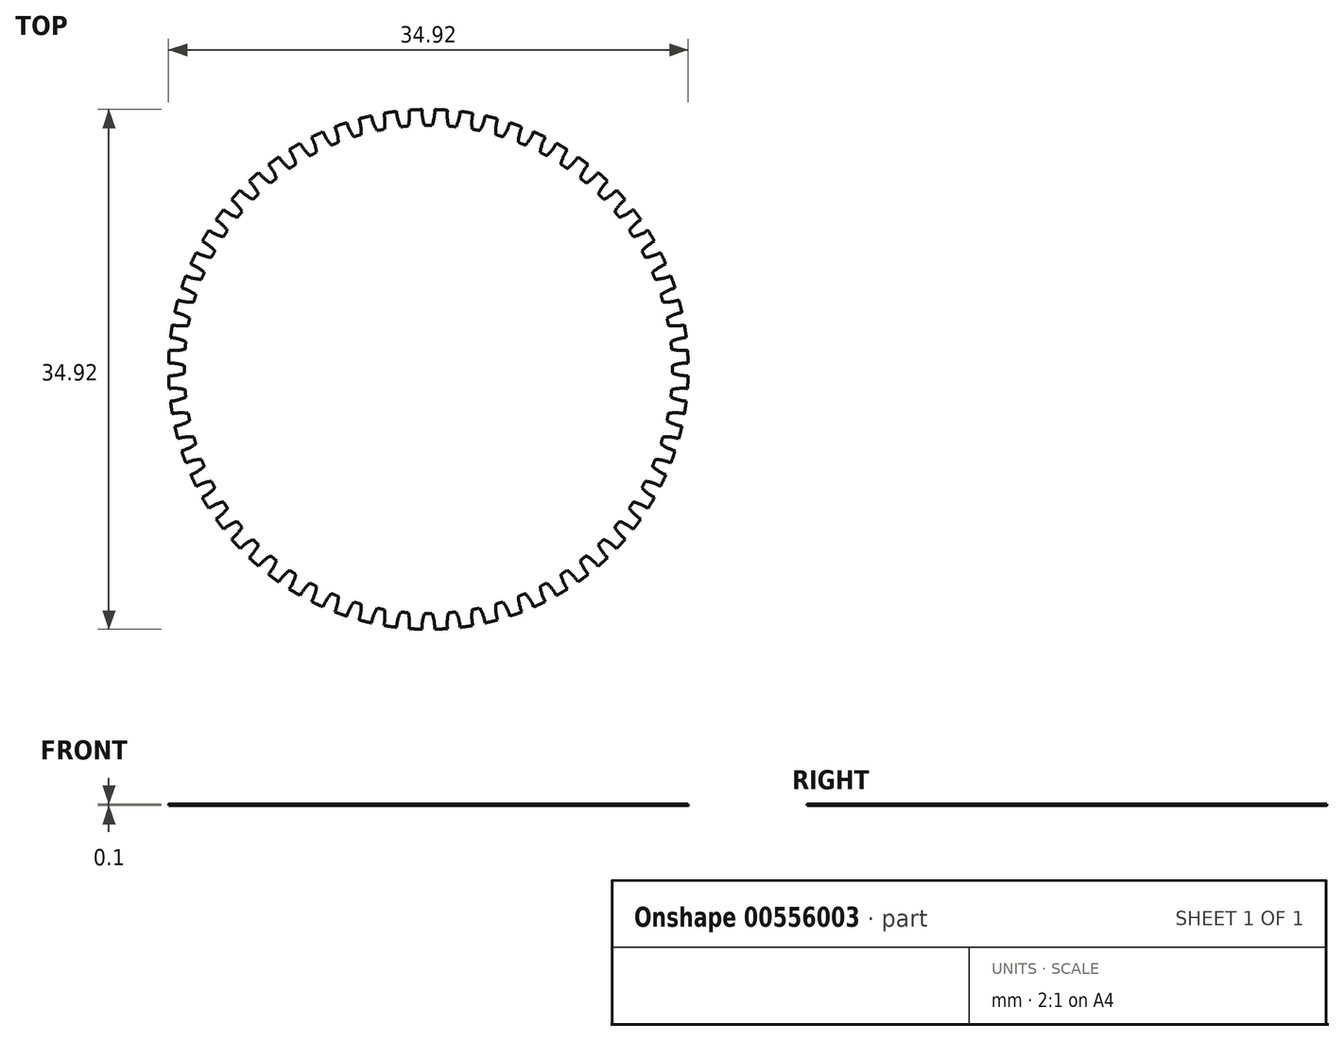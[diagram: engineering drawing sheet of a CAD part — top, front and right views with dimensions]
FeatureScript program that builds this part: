
annotation { "Feature Type Name" : "Feature", "Feature Type Description" : "" }
export const myFeature = defineFeature(function(context is Context, id is Id, definition is map)
    precondition{}
    {
        {
            var Q0;
            Q0=qCreatedBy(makeId("Top.planeOp"),FACE);
            var sketch = newSketch(context, id + "F0", { "sketchPlane" : qUnion([Q0])});
            skPoint(sketch, "E0", {"position": v(0.27, 22.75) * mm});
            skPoint(sketch, "E1", {"position": v(0.39, 22.22) * mm});
            skPoint(sketch, "E2", {"position": v(0.4, 21.7) * mm});
            skPoint(sketch, "E3", {"position": v(0.43, 17.46) * mm});
            skPoint(sketch, "E4", {"position": v(0.39, 16.93) * mm});
            skPoint(sketch, "E5", {"position": v(0.25, 16.4) * mm});
            skArc(sketch, "E6", {"start": v(0, 16.4) * mm, "mid": v(0.13, 16.4) * mm, "end": v(0.25, 16.4) * mm});
            skArc(sketch, "E7", {"start": v(0.43, 17.46) * mm, "mid": v(0.64, 17.46) * mm, "end": v(0.86, 17.45) * mm});
            skArc(sketch, "E8", {"start": v(0, 22.75) * mm, "mid": v(0.13, 22.75) * mm, "end": v(0.27, 22.75) * mm});
            skArc(sketch, "E9", {"start": v(0.4, 21.7) * mm, "mid": v(0.6, 21.69) * mm, "end": v(0.81, 21.68) * mm});
            skArc(sketch, "E10", {"start": v(0.4, 21.7) * mm, "mid": v(0.39, 22.23) * mm, "end": v(0.27, 22.75) * mm});
            skArc(sketch, "E11", {"start": v(0.25, 16.4) * mm, "mid": v(0.39, 16.92) * mm, "end": v(0.43, 17.46) * mm});
            skArc(sketch, "E12.MirrorCS", {"start": v(0, 22.75) * mm, "mid": v(-0.13, 22.75) * mm, "end": v(-0.27, 22.75) * mm});
            skArc(sketch, "E13.MirrorCS", {"start": v(0, 16.4) * mm, "mid": v(-0.13, 16.4) * mm, "end": v(-0.25, 16.4) * mm});
            skArc(sketch, "E14.MirrorCS", {"start": v(-0.43, 17.46) * mm, "mid": v(-0.64, 17.46) * mm, "end": v(-0.86, 17.45) * mm});
            skArc(sketch, "E15.MirrorCS", {"start": v(-0.4, 21.7) * mm, "mid": v(-0.6, 21.69) * mm, "end": v(-0.81, 21.68) * mm});
            skArc(sketch, "E16.MirrorCS", {"start": v(-0.4, 21.7) * mm, "mid": v(-0.39, 22.23) * mm, "end": v(-0.27, 22.75) * mm});
            skArc(sketch, "E17.MirrorCS", {"start": v(-0.25, 16.4) * mm, "mid": v(-0.39, 16.92) * mm, "end": v(-0.43, 17.46) * mm});
            skPoint(sketch, "E18.MirrorP", {"position": v(-0.39, 22.22) * mm});
            skPoint(sketch, "E19.MirrorP", {"position": v(-0.43, 17.46) * mm});
            skPoint(sketch, "E20.MirrorP", {"position": v(-0.39, 16.93) * mm});
            skPoint(sketch, "E21.MirrorP", {"position": v(-0.4, 21.7) * mm});
            skPoint(sketch, "E22.MirrorP", {"position": v(-0.27, 22.75) * mm});
            skPoint(sketch, "E23.MirrorP", {"position": v(-0.25, 16.4) * mm});
            skPoint(sketch, "E24.1.0", {"position": v(-1.44, 22.7) * mm});
            skPoint(sketch, "E24.1.1", {"position": v(-1.97, 22.67) * mm});
            skPoint(sketch, "E24.1.2", {"position": v(-1.27, 22.19) * mm});
            skPoint(sketch, "E24.1.3", {"position": v(-2.05, 22.13) * mm});
            skPoint(sketch, "E24.1.4", {"position": v(-1.22, 21.66) * mm});
            skPoint(sketch, "E24.1.5", {"position": v(-2.03, 21.6) * mm});
            skArc(sketch, "E24.1.6", {"start": v(-1.22, 21.66) * mm, "mid": v(-1.01, 21.67) * mm, "end": v(-0.81, 21.68) * mm});
            skArc(sketch, "E24.1.7", {"start": v(-2.03, 21.6) * mm, "mid": v(-2.05, 22.14) * mm, "end": v(-1.97, 22.67) * mm});
            skArc(sketch, "E24.1.8", {"start": v(-1.22, 21.66) * mm, "mid": v(-1.27, 22.2) * mm, "end": v(-1.44, 22.7) * mm});
            skArc(sketch, "E24.1.9", {"start": v(-2.03, 21.6) * mm, "mid": v(-2.23, 21.58) * mm, "end": v(-2.43, 21.56) * mm});
            skArc(sketch, "E24.1.10", {"start": v(-1.7, 22.7) * mm, "mid": v(-1.57, 22.7) * mm, "end": v(-1.44, 22.7) * mm});
            skArc(sketch, "E24.1.11", {"start": v(-1.7, 22.7) * mm, "mid": v(-1.83, 22.68) * mm, "end": v(-1.97, 22.67) * mm});
            skPoint(sketch, "E24.2.0", {"position": v(-3.13, 22.54) * mm});
            skPoint(sketch, "E24.2.1", {"position": v(-3.65, 22.46) * mm});
            skPoint(sketch, "E24.2.2", {"position": v(-2.93, 22.03) * mm});
            skPoint(sketch, "E24.2.3", {"position": v(-3.7, 21.92) * mm});
            skPoint(sketch, "E24.2.4", {"position": v(-2.83, 21.51) * mm});
            skPoint(sketch, "E24.2.5", {"position": v(-3.63, 21.39) * mm});
            skArc(sketch, "E24.2.6", {"start": v(-2.83, 21.51) * mm, "mid": v(-2.63, 21.54) * mm, "end": v(-2.43, 21.56) * mm});
            skArc(sketch, "E24.2.7", {"start": v(-3.63, 21.39) * mm, "mid": v(-3.7, 21.92) * mm, "end": v(-3.65, 22.46) * mm});
            skArc(sketch, "E24.2.8", {"start": v(-2.83, 21.51) * mm, "mid": v(-2.93, 22.04) * mm, "end": v(-3.13, 22.54) * mm});
            skArc(sketch, "E24.2.9", {"start": v(-3.63, 21.39) * mm, "mid": v(-3.83, 21.35) * mm, "end": v(-4.03, 21.32) * mm});
            skArc(sketch, "E24.2.10", {"start": v(-3.4, 22.5) * mm, "mid": v(-3.26, 22.52) * mm, "end": v(-3.13, 22.54) * mm});
            skArc(sketch, "E24.2.11", {"start": v(-3.4, 22.5) * mm, "mid": v(-3.52, 22.48) * mm, "end": v(-3.65, 22.46) * mm});
            skPoint(sketch, "E24.3.0", {"position": v(-4.8, 22.24) * mm});
            skPoint(sketch, "E24.3.1", {"position": v(-5.32, 22.12) * mm});
            skPoint(sketch, "E24.3.2", {"position": v(-4.56, 21.75) * mm});
            skPoint(sketch, "E24.3.3", {"position": v(-5.32, 21.58) * mm});
            skPoint(sketch, "E24.3.4", {"position": v(-4.43, 21.24) * mm});
            skPoint(sketch, "E24.3.5", {"position": v(-5.22, 21.06) * mm});
            skArc(sketch, "E24.3.6", {"start": v(-4.43, 21.24) * mm, "mid": v(-4.23, 21.28) * mm, "end": v(-4.03, 21.32) * mm});
            skArc(sketch, "E24.3.7", {"start": v(-5.22, 21.06) * mm, "mid": v(-5.33, 21.59) * mm, "end": v(-5.32, 22.12) * mm});
            skArc(sketch, "E24.3.8", {"start": v(-4.43, 21.24) * mm, "mid": v(-4.57, 21.76) * mm, "end": v(-4.8, 22.24) * mm});
            skArc(sketch, "E24.3.9", {"start": v(-5.22, 21.06) * mm, "mid": v(-5.42, 21) * mm, "end": v(-5.62, 20.96) * mm});
            skArc(sketch, "E24.3.10", {"start": v(-5.06, 22.18) * mm, "mid": v(-4.93, 22.21) * mm, "end": v(-4.8, 22.24) * mm});
            skArc(sketch, "E24.3.11", {"start": v(-5.06, 22.18) * mm, "mid": v(-5.2, 22.15) * mm, "end": v(-5.32, 22.12) * mm});
            skPoint(sketch, "E24.4.0", {"position": v(-6.45, 21.82) * mm});
            skPoint(sketch, "E24.4.1", {"position": v(-6.96, 21.66) * mm});
            skPoint(sketch, "E24.4.2", {"position": v(-6.18, 21.35) * mm});
            skPoint(sketch, "E24.4.3", {"position": v(-6.92, 21.12) * mm});
            skPoint(sketch, "E24.4.4", {"position": v(-6, 20.85) * mm});
            skPoint(sketch, "E24.4.5", {"position": v(-6.78, 20.6) * mm});
            skArc(sketch, "E24.4.6", {"start": v(-6, 20.85) * mm, "mid": v(-5.81, 20.9) * mm, "end": v(-5.62, 20.96) * mm});
            skArc(sketch, "E24.4.7", {"start": v(-6.78, 20.6) * mm, "mid": v(-6.92, 21.13) * mm, "end": v(-6.96, 21.66) * mm});
            skArc(sketch, "E24.4.8", {"start": v(-6, 20.85) * mm, "mid": v(-6.18, 21.36) * mm, "end": v(-6.45, 21.82) * mm});
            skArc(sketch, "E24.4.9", {"start": v(-6.78, 20.6) * mm, "mid": v(-6.97, 20.54) * mm, "end": v(-7.17, 20.48) * mm});
            skArc(sketch, "E24.4.10", {"start": v(-6.7, 21.74) * mm, "mid": v(-6.58, 21.78) * mm, "end": v(-6.45, 21.82) * mm});
            skArc(sketch, "E24.4.11", {"start": v(-6.7, 21.74) * mm, "mid": v(-6.83, 21.7) * mm, "end": v(-6.96, 21.66) * mm});
            skPoint(sketch, "E24.5.0", {"position": v(-8.06, 21.28) * mm});
            skPoint(sketch, "E24.5.1", {"position": v(-8.56, 21.08) * mm});
            skPoint(sketch, "E24.5.2", {"position": v(-7.76, 20.83) * mm});
            skPoint(sketch, "E24.5.3", {"position": v(-8.48, 20.54) * mm});
            skPoint(sketch, "E24.5.4", {"position": v(-7.55, 20.34) * mm});
            skPoint(sketch, "E24.5.5", {"position": v(-8.3, 20.04) * mm});
            skArc(sketch, "E24.5.6", {"start": v(-7.55, 20.34) * mm, "mid": v(-7.36, 20.41) * mm, "end": v(-7.17, 20.48) * mm});
            skArc(sketch, "E24.5.7", {"start": v(-8.3, 20.04) * mm, "mid": v(-8.48, 20.55) * mm, "end": v(-8.56, 21.08) * mm});
            skArc(sketch, "E24.5.8", {"start": v(-7.55, 20.34) * mm, "mid": v(-7.76, 20.83) * mm, "end": v(-8.06, 21.28) * mm});
            skArc(sketch, "E24.5.9", {"start": v(-8.3, 20.04) * mm, "mid": v(-8.49, 19.97) * mm, "end": v(-8.68, 19.89) * mm});
            skArc(sketch, "E24.5.10", {"start": v(-8.31, 21.18) * mm, "mid": v(-8.19, 21.23) * mm, "end": v(-8.06, 21.28) * mm});
            skArc(sketch, "E24.5.11", {"start": v(-8.31, 21.18) * mm, "mid": v(-8.44, 21.13) * mm, "end": v(-8.56, 21.08) * mm});
            skPoint(sketch, "E24.6.0", {"position": v(-9.63, 20.61) * mm});
            skPoint(sketch, "E24.6.1", {"position": v(-10.11, 20.38) * mm});
            skPoint(sketch, "E24.6.2", {"position": v(-9.3, 20.2) * mm});
            skPoint(sketch, "E24.6.3", {"position": v(-10, 19.85) * mm});
            skPoint(sketch, "E24.6.4", {"position": v(-9.05, 19.72) * mm});
            skPoint(sketch, "E24.6.5", {"position": v(-9.78, 19.37) * mm});
            skArc(sketch, "E24.6.6", {"start": v(-9.05, 19.72) * mm, "mid": v(-8.86, 19.8) * mm, "end": v(-8.68, 19.89) * mm});
            skArc(sketch, "E24.6.7", {"start": v(-9.78, 19.37) * mm, "mid": v(-10, 19.86) * mm, "end": v(-10.11, 20.38) * mm});
            skArc(sketch, "E24.6.8", {"start": v(-9.05, 19.72) * mm, "mid": v(-9.3, 20.2) * mm, "end": v(-9.63, 20.61) * mm});
            skArc(sketch, "E24.6.9", {"start": v(-9.78, 19.37) * mm, "mid": v(-9.96, 19.28) * mm, "end": v(-10.14, 19.18) * mm});
            skArc(sketch, "E24.6.10", {"start": v(-9.87, 20.5) * mm, "mid": v(-9.75, 20.56) * mm, "end": v(-9.63, 20.61) * mm});
            skArc(sketch, "E24.6.11", {"start": v(-9.87, 20.5) * mm, "mid": v(-10, 20.44) * mm, "end": v(-10.11, 20.38) * mm});
            skPoint(sketch, "E24.7.0", {"position": v(-11.15, 19.84) * mm});
            skPoint(sketch, "E24.7.1", {"position": v(-11.6, 19.57) * mm});
            skPoint(sketch, "E24.7.2", {"position": v(-10.77, 19.44) * mm});
            skPoint(sketch, "E24.7.3", {"position": v(-11.45, 19.05) * mm});
            skPoint(sketch, "E24.7.4", {"position": v(-10.5, 18.99) * mm});
            skPoint(sketch, "E24.7.5", {"position": v(-11.2, 18.58) * mm});
            skArc(sketch, "E24.7.6", {"start": v(-10.5, 18.99) * mm, "mid": v(-10.32, 19.09) * mm, "end": v(-10.14, 19.18) * mm});
            skArc(sketch, "E24.7.7", {"start": v(-11.2, 18.58) * mm, "mid": v(-11.45, 19.06) * mm, "end": v(-11.6, 19.57) * mm});
            skArc(sketch, "E24.7.8", {"start": v(-10.5, 18.99) * mm, "mid": v(-10.78, 19.45) * mm, "end": v(-11.15, 19.84) * mm});
            skArc(sketch, "E24.7.9", {"start": v(-11.2, 18.58) * mm, "mid": v(-11.37, 18.48) * mm, "end": v(-11.54, 18.37) * mm});
            skArc(sketch, "E24.7.10", {"start": v(-11.38, 19.7) * mm, "mid": v(-11.26, 19.77) * mm, "end": v(-11.15, 19.84) * mm});
            skArc(sketch, "E24.7.11", {"start": v(-11.38, 19.7) * mm, "mid": v(-11.5, 19.64) * mm, "end": v(-11.6, 19.57) * mm});
            skPoint(sketch, "E24.8.0", {"position": v(-12.6, 18.95) * mm});
            skPoint(sketch, "E24.8.1", {"position": v(-13.04, 18.65) * mm});
            skPoint(sketch, "E24.8.2", {"position": v(-12.2, 18.58) * mm});
            skPoint(sketch, "E24.8.3", {"position": v(-12.84, 18.14) * mm});
            skPoint(sketch, "E24.8.4", {"position": v(-11.88, 18.15) * mm});
            skPoint(sketch, "E24.8.5", {"position": v(-12.55, 17.7) * mm});
            skArc(sketch, "E24.8.6", {"start": v(-11.88, 18.15) * mm, "mid": v(-11.71, 18.26) * mm, "end": v(-11.54, 18.37) * mm});
            skArc(sketch, "E24.8.7", {"start": v(-12.55, 17.7) * mm, "mid": v(-12.84, 18.15) * mm, "end": v(-13.04, 18.65) * mm});
            skArc(sketch, "E24.8.8", {"start": v(-11.88, 18.15) * mm, "mid": v(-12.2, 18.59) * mm, "end": v(-12.6, 18.95) * mm});
            skArc(sketch, "E24.8.9", {"start": v(-12.55, 17.7) * mm, "mid": v(-12.72, 17.58) * mm, "end": v(-12.88, 17.46) * mm});
            skArc(sketch, "E24.8.10", {"start": v(-12.82, 18.8) * mm, "mid": v(-12.7, 18.87) * mm, "end": v(-12.6, 18.95) * mm});
            skArc(sketch, "E24.8.11", {"start": v(-12.82, 18.8) * mm, "mid": v(-12.93, 18.73) * mm, "end": v(-13.04, 18.65) * mm});
            skPoint(sketch, "E24.9.0", {"position": v(-13.98, 17.95) * mm});
            skPoint(sketch, "E24.9.1", {"position": v(-14.4, 17.62) * mm});
            skPoint(sketch, "E24.9.2", {"position": v(-13.55, 17.62) * mm});
            skPoint(sketch, "E24.9.3", {"position": v(-14.16, 17.13) * mm});
            skPoint(sketch, "E24.9.4", {"position": v(-13.2, 17.21) * mm});
            skPoint(sketch, "E24.9.5", {"position": v(-13.84, 16.7) * mm});
            skArc(sketch, "E24.9.6", {"start": v(-13.2, 17.21) * mm, "mid": v(-13.05, 17.34) * mm, "end": v(-12.88, 17.46) * mm});
            skArc(sketch, "E24.9.7", {"start": v(-13.84, 16.7) * mm, "mid": v(-14.16, 17.14) * mm, "end": v(-14.4, 17.62) * mm});
            skArc(sketch, "E24.9.8", {"start": v(-13.2, 17.21) * mm, "mid": v(-13.56, 17.62) * mm, "end": v(-13.98, 17.95) * mm});
            skArc(sketch, "E24.9.9", {"start": v(-13.84, 16.7) * mm, "mid": v(-14, 16.58) * mm, "end": v(-14.15, 16.44) * mm});
            skArc(sketch, "E24.9.10", {"start": v(-14.19, 17.79) * mm, "mid": v(-14.08, 17.87) * mm, "end": v(-13.98, 17.95) * mm});
            skArc(sketch, "E24.9.11", {"start": v(-14.19, 17.79) * mm, "mid": v(-14.3, 17.7) * mm, "end": v(-14.4, 17.62) * mm});
            skPoint(sketch, "E24.10.0", {"position": v(-15.28, 16.86) * mm});
            skPoint(sketch, "E24.10.1", {"position": v(-15.67, 16.5) * mm});
            skPoint(sketch, "E24.10.2", {"position": v(-14.83, 16.55) * mm});
            skPoint(sketch, "E24.10.3", {"position": v(-15.4, 16.02) * mm});
            skPoint(sketch, "E24.10.4", {"position": v(-14.46, 16.18) * mm});
            skPoint(sketch, "E24.10.5", {"position": v(-15.05, 15.63) * mm});
            skArc(sketch, "E24.10.6", {"start": v(-14.46, 16.18) * mm, "mid": v(-14.3, 16.31) * mm, "end": v(-14.15, 16.44) * mm});
            skArc(sketch, "E24.10.7", {"start": v(-15.05, 15.63) * mm, "mid": v(-15.4, 16.03) * mm, "end": v(-15.67, 16.5) * mm});
            skArc(sketch, "E24.10.8", {"start": v(-14.46, 16.18) * mm, "mid": v(-14.83, 16.56) * mm, "end": v(-15.28, 16.86) * mm});
            skArc(sketch, "E24.10.9", {"start": v(-15.05, 15.63) * mm, "mid": v(-15.2, 15.48) * mm, "end": v(-15.34, 15.34) * mm});
            skArc(sketch, "E24.10.10", {"start": v(-15.48, 16.68) * mm, "mid": v(-15.38, 16.77) * mm, "end": v(-15.28, 16.86) * mm});
            skArc(sketch, "E24.10.11", {"start": v(-15.48, 16.68) * mm, "mid": v(-15.57, 16.59) * mm, "end": v(-15.67, 16.5) * mm});
            skPoint(sketch, "E24.11.0", {"position": v(-16.5, 15.67) * mm});
            skPoint(sketch, "E24.11.1", {"position": v(-16.86, 15.28) * mm});
            skPoint(sketch, "E24.11.2", {"position": v(-16.02, 15.4) * mm});
            skPoint(sketch, "E24.11.3", {"position": v(-16.55, 14.83) * mm});
            skPoint(sketch, "E24.11.4", {"position": v(-15.63, 15.05) * mm});
            skPoint(sketch, "E24.11.5", {"position": v(-16.18, 14.46) * mm});
            skArc(sketch, "E24.11.6", {"start": v(-15.63, 15.05) * mm, "mid": v(-15.48, 15.2) * mm, "end": v(-15.34, 15.34) * mm});
            skArc(sketch, "E24.11.7", {"start": v(-16.18, 14.46) * mm, "mid": v(-16.56, 14.83) * mm, "end": v(-16.86, 15.28) * mm});
            skArc(sketch, "E24.11.8", {"start": v(-15.63, 15.05) * mm, "mid": v(-16.03, 15.4) * mm, "end": v(-16.5, 15.67) * mm});
            skArc(sketch, "E24.11.9", {"start": v(-16.18, 14.46) * mm, "mid": v(-16.31, 14.3) * mm, "end": v(-16.44, 14.15) * mm});
            skArc(sketch, "E24.11.10", {"start": v(-16.68, 15.48) * mm, "mid": v(-16.59, 15.57) * mm, "end": v(-16.5, 15.67) * mm});
            skArc(sketch, "E24.11.11", {"start": v(-16.68, 15.48) * mm, "mid": v(-16.77, 15.38) * mm, "end": v(-16.86, 15.28) * mm});
            skPoint(sketch, "E24.12.0", {"position": v(-17.62, 14.4) * mm});
            skPoint(sketch, "E24.12.1", {"position": v(-17.95, 13.98) * mm});
            skPoint(sketch, "E24.12.2", {"position": v(-17.13, 14.16) * mm});
            skPoint(sketch, "E24.12.3", {"position": v(-17.62, 13.55) * mm});
            skPoint(sketch, "E24.12.4", {"position": v(-16.7, 13.84) * mm});
            skPoint(sketch, "E24.12.5", {"position": v(-17.21, 13.2) * mm});
            skArc(sketch, "E24.12.6", {"start": v(-16.7, 13.84) * mm, "mid": v(-16.58, 14) * mm, "end": v(-16.44, 14.15) * mm});
            skArc(sketch, "E24.12.7", {"start": v(-17.21, 13.2) * mm, "mid": v(-17.62, 13.56) * mm, "end": v(-17.95, 13.98) * mm});
            skArc(sketch, "E24.12.8", {"start": v(-16.7, 13.84) * mm, "mid": v(-17.14, 14.16) * mm, "end": v(-17.62, 14.4) * mm});
            skArc(sketch, "E24.12.9", {"start": v(-17.21, 13.2) * mm, "mid": v(-17.34, 13.05) * mm, "end": v(-17.46, 12.88) * mm});
            skArc(sketch, "E24.12.10", {"start": v(-17.79, 14.19) * mm, "mid": v(-17.7, 14.3) * mm, "end": v(-17.62, 14.4) * mm});
            skArc(sketch, "E24.12.11", {"start": v(-17.79, 14.19) * mm, "mid": v(-17.87, 14.08) * mm, "end": v(-17.95, 13.98) * mm});
            skPoint(sketch, "E24.13.0", {"position": v(-18.65, 13.04) * mm});
            skPoint(sketch, "E24.13.1", {"position": v(-18.95, 12.6) * mm});
            skPoint(sketch, "E24.13.2", {"position": v(-18.14, 12.84) * mm});
            skPoint(sketch, "E24.13.3", {"position": v(-18.58, 12.2) * mm});
            skPoint(sketch, "E24.13.4", {"position": v(-17.7, 12.55) * mm});
            skPoint(sketch, "E24.13.5", {"position": v(-18.15, 11.88) * mm});
            skArc(sketch, "E24.13.6", {"start": v(-17.7, 12.55) * mm, "mid": v(-17.58, 12.72) * mm, "end": v(-17.46, 12.88) * mm});
            skArc(sketch, "E24.13.7", {"start": v(-18.15, 11.88) * mm, "mid": v(-18.59, 12.2) * mm, "end": v(-18.95, 12.6) * mm});
            skArc(sketch, "E24.13.8", {"start": v(-17.7, 12.55) * mm, "mid": v(-18.15, 12.84) * mm, "end": v(-18.65, 13.04) * mm});
            skArc(sketch, "E24.13.9", {"start": v(-18.15, 11.88) * mm, "mid": v(-18.26, 11.71) * mm, "end": v(-18.37, 11.54) * mm});
            skArc(sketch, "E24.13.10", {"start": v(-18.8, 12.82) * mm, "mid": v(-18.73, 12.93) * mm, "end": v(-18.65, 13.04) * mm});
            skArc(sketch, "E24.13.11", {"start": v(-18.8, 12.82) * mm, "mid": v(-18.87, 12.7) * mm, "end": v(-18.95, 12.6) * mm});
            skPoint(sketch, "E24.14.0", {"position": v(-19.57, 11.6) * mm});
            skPoint(sketch, "E24.14.1", {"position": v(-19.84, 11.15) * mm});
            skPoint(sketch, "E24.14.2", {"position": v(-19.05, 11.45) * mm});
            skPoint(sketch, "E24.14.3", {"position": v(-19.44, 10.77) * mm});
            skPoint(sketch, "E24.14.4", {"position": v(-18.58, 11.2) * mm});
            skPoint(sketch, "E24.14.5", {"position": v(-18.99, 10.5) * mm});
            skArc(sketch, "E24.14.6", {"start": v(-18.58, 11.2) * mm, "mid": v(-18.48, 11.37) * mm, "end": v(-18.37, 11.54) * mm});
            skArc(sketch, "E24.14.7", {"start": v(-18.99, 10.5) * mm, "mid": v(-19.45, 10.78) * mm, "end": v(-19.84, 11.15) * mm});
            skArc(sketch, "E24.14.8", {"start": v(-18.58, 11.2) * mm, "mid": v(-19.06, 11.45) * mm, "end": v(-19.57, 11.6) * mm});
            skArc(sketch, "E24.14.9", {"start": v(-18.99, 10.5) * mm, "mid": v(-19.09, 10.32) * mm, "end": v(-19.18, 10.14) * mm});
            skArc(sketch, "E24.14.10", {"start": v(-19.7, 11.38) * mm, "mid": v(-19.64, 11.5) * mm, "end": v(-19.57, 11.6) * mm});
            skArc(sketch, "E24.14.11", {"start": v(-19.7, 11.38) * mm, "mid": v(-19.77, 11.26) * mm, "end": v(-19.84, 11.15) * mm});
            skPoint(sketch, "E24.15.0", {"position": v(-20.38, 10.11) * mm});
            skPoint(sketch, "E24.15.1", {"position": v(-20.61, 9.63) * mm});
            skPoint(sketch, "E24.15.2", {"position": v(-19.85, 10) * mm});
            skPoint(sketch, "E24.15.3", {"position": v(-20.2, 9.3) * mm});
            skPoint(sketch, "E24.15.4", {"position": v(-19.37, 9.78) * mm});
            skPoint(sketch, "E24.15.5", {"position": v(-19.72, 9.05) * mm});
            skArc(sketch, "E24.15.6", {"start": v(-19.37, 9.78) * mm, "mid": v(-19.28, 9.96) * mm, "end": v(-19.18, 10.14) * mm});
            skArc(sketch, "E24.15.7", {"start": v(-19.72, 9.05) * mm, "mid": v(-20.2, 9.3) * mm, "end": v(-20.61, 9.63) * mm});
            skArc(sketch, "E24.15.8", {"start": v(-19.37, 9.78) * mm, "mid": v(-19.86, 10) * mm, "end": v(-20.38, 10.11) * mm});
            skArc(sketch, "E24.15.9", {"start": v(-19.72, 9.05) * mm, "mid": v(-19.8, 8.86) * mm, "end": v(-19.89, 8.68) * mm});
            skArc(sketch, "E24.15.10", {"start": v(-20.5, 9.87) * mm, "mid": v(-20.44, 10) * mm, "end": v(-20.38, 10.11) * mm});
            skArc(sketch, "E24.15.11", {"start": v(-20.5, 9.87) * mm, "mid": v(-20.56, 9.75) * mm, "end": v(-20.61, 9.63) * mm});
            skPoint(sketch, "E24.16.0", {"position": v(-21.08, 8.56) * mm});
            skPoint(sketch, "E24.16.1", {"position": v(-21.28, 8.06) * mm});
            skPoint(sketch, "E24.16.2", {"position": v(-20.54, 8.48) * mm});
            skPoint(sketch, "E24.16.3", {"position": v(-20.83, 7.76) * mm});
            skPoint(sketch, "E24.16.4", {"position": v(-20.04, 8.3) * mm});
            skPoint(sketch, "E24.16.5", {"position": v(-20.34, 7.55) * mm});
            skArc(sketch, "E24.16.6", {"start": v(-20.04, 8.3) * mm, "mid": v(-19.97, 8.49) * mm, "end": v(-19.89, 8.68) * mm});
            skArc(sketch, "E24.16.7", {"start": v(-20.34, 7.55) * mm, "mid": v(-20.83, 7.76) * mm, "end": v(-21.28, 8.06) * mm});
            skArc(sketch, "E24.16.8", {"start": v(-20.04, 8.3) * mm, "mid": v(-20.55, 8.48) * mm, "end": v(-21.08, 8.56) * mm});
            skArc(sketch, "E24.16.9", {"start": v(-20.34, 7.55) * mm, "mid": v(-20.41, 7.36) * mm, "end": v(-20.48, 7.17) * mm});
            skArc(sketch, "E24.16.10", {"start": v(-21.18, 8.31) * mm, "mid": v(-21.13, 8.44) * mm, "end": v(-21.08, 8.56) * mm});
            skArc(sketch, "E24.16.11", {"start": v(-21.18, 8.31) * mm, "mid": v(-21.23, 8.19) * mm, "end": v(-21.28, 8.06) * mm});
            skPoint(sketch, "E24.17.0", {"position": v(-21.66, 6.96) * mm});
            skPoint(sketch, "E24.17.1", {"position": v(-21.82, 6.45) * mm});
            skPoint(sketch, "E24.17.2", {"position": v(-21.12, 6.92) * mm});
            skPoint(sketch, "E24.17.3", {"position": v(-21.35, 6.18) * mm});
            skPoint(sketch, "E24.17.4", {"position": v(-20.6, 6.78) * mm});
            skPoint(sketch, "E24.17.5", {"position": v(-20.85, 6) * mm});
            skArc(sketch, "E24.17.6", {"start": v(-20.6, 6.78) * mm, "mid": v(-20.54, 6.97) * mm, "end": v(-20.48, 7.17) * mm});
            skArc(sketch, "E24.17.7", {"start": v(-20.85, 6) * mm, "mid": v(-21.36, 6.18) * mm, "end": v(-21.82, 6.45) * mm});
            skArc(sketch, "E24.17.8", {"start": v(-20.6, 6.78) * mm, "mid": v(-21.13, 6.92) * mm, "end": v(-21.66, 6.96) * mm});
            skArc(sketch, "E24.17.9", {"start": v(-20.85, 6) * mm, "mid": v(-20.9, 5.81) * mm, "end": v(-20.96, 5.62) * mm});
            skArc(sketch, "E24.17.10", {"start": v(-21.74, 6.7) * mm, "mid": v(-21.7, 6.83) * mm, "end": v(-21.66, 6.96) * mm});
            skArc(sketch, "E24.17.11", {"start": v(-21.74, 6.7) * mm, "mid": v(-21.78, 6.58) * mm, "end": v(-21.82, 6.45) * mm});
            skPoint(sketch, "E24.18.0", {"position": v(-22.12, 5.32) * mm});
            skPoint(sketch, "E24.18.1", {"position": v(-22.24, 4.8) * mm});
            skPoint(sketch, "E24.18.2", {"position": v(-21.58, 5.32) * mm});
            skPoint(sketch, "E24.18.3", {"position": v(-21.75, 4.56) * mm});
            skPoint(sketch, "E24.18.4", {"position": v(-21.06, 5.22) * mm});
            skPoint(sketch, "E24.18.5", {"position": v(-21.24, 4.43) * mm});
            skArc(sketch, "E24.18.6", {"start": v(-21.06, 5.22) * mm, "mid": v(-21, 5.42) * mm, "end": v(-20.96, 5.62) * mm});
            skArc(sketch, "E24.18.7", {"start": v(-21.24, 4.43) * mm, "mid": v(-21.76, 4.57) * mm, "end": v(-22.24, 4.8) * mm});
            skArc(sketch, "E24.18.8", {"start": v(-21.06, 5.22) * mm, "mid": v(-21.59, 5.33) * mm, "end": v(-22.12, 5.32) * mm});
            skArc(sketch, "E24.18.9", {"start": v(-21.24, 4.43) * mm, "mid": v(-21.28, 4.23) * mm, "end": v(-21.32, 4.03) * mm});
            skArc(sketch, "E24.18.10", {"start": v(-22.18, 5.06) * mm, "mid": v(-22.15, 5.2) * mm, "end": v(-22.12, 5.32) * mm});
            skArc(sketch, "E24.18.11", {"start": v(-22.18, 5.06) * mm, "mid": v(-22.21, 4.93) * mm, "end": v(-22.24, 4.8) * mm});
            skPoint(sketch, "E24.19.0", {"position": v(-22.46, 3.65) * mm});
            skPoint(sketch, "E24.19.1", {"position": v(-22.54, 3.13) * mm});
            skPoint(sketch, "E24.19.2", {"position": v(-21.92, 3.7) * mm});
            skPoint(sketch, "E24.19.3", {"position": v(-22.03, 2.93) * mm});
            skPoint(sketch, "E24.19.4", {"position": v(-21.39, 3.63) * mm});
            skPoint(sketch, "E24.19.5", {"position": v(-21.51, 2.83) * mm});
            skArc(sketch, "E24.19.6", {"start": v(-21.39, 3.63) * mm, "mid": v(-21.35, 3.83) * mm, "end": v(-21.32, 4.03) * mm});
            skArc(sketch, "E24.19.7", {"start": v(-21.51, 2.83) * mm, "mid": v(-22.04, 2.93) * mm, "end": v(-22.54, 3.13) * mm});
            skArc(sketch, "E24.19.8", {"start": v(-21.39, 3.63) * mm, "mid": v(-21.92, 3.7) * mm, "end": v(-22.46, 3.65) * mm});
            skArc(sketch, "E24.19.9", {"start": v(-21.51, 2.83) * mm, "mid": v(-21.54, 2.63) * mm, "end": v(-21.56, 2.43) * mm});
            skArc(sketch, "E24.19.10", {"start": v(-22.5, 3.4) * mm, "mid": v(-22.48, 3.52) * mm, "end": v(-22.46, 3.65) * mm});
            skArc(sketch, "E24.19.11", {"start": v(-22.5, 3.4) * mm, "mid": v(-22.52, 3.26) * mm, "end": v(-22.54, 3.13) * mm});
            skPoint(sketch, "E24.20.0", {"position": v(-22.67, 1.97) * mm});
            skPoint(sketch, "E24.20.1", {"position": v(-22.7, 1.44) * mm});
            skPoint(sketch, "E24.20.2", {"position": v(-22.13, 2.05) * mm});
            skPoint(sketch, "E24.20.3", {"position": v(-22.19, 1.27) * mm});
            skPoint(sketch, "E24.20.4", {"position": v(-21.6, 2.03) * mm});
            skPoint(sketch, "E24.20.5", {"position": v(-21.66, 1.22) * mm});
            skArc(sketch, "E24.20.6", {"start": v(-21.6, 2.03) * mm, "mid": v(-21.58, 2.23) * mm, "end": v(-21.56, 2.43) * mm});
            skArc(sketch, "E24.20.7", {"start": v(-21.66, 1.22) * mm, "mid": v(-22.2, 1.27) * mm, "end": v(-22.7, 1.44) * mm});
            skArc(sketch, "E24.20.8", {"start": v(-21.6, 2.03) * mm, "mid": v(-22.14, 2.05) * mm, "end": v(-22.67, 1.97) * mm});
            skArc(sketch, "E24.20.9", {"start": v(-21.66, 1.22) * mm, "mid": v(-21.67, 1.01) * mm, "end": v(-21.68, 0.81) * mm});
            skArc(sketch, "E24.20.10", {"start": v(-22.7, 1.7) * mm, "mid": v(-22.68, 1.83) * mm, "end": v(-22.67, 1.97) * mm});
            skArc(sketch, "E24.20.11", {"start": v(-22.7, 1.7) * mm, "mid": v(-22.7, 1.57) * mm, "end": v(-22.7, 1.44) * mm});
            skPoint(sketch, "E24.21.0", {"position": v(-22.75, 0.27) * mm});
            skPoint(sketch, "E24.21.1", {"position": v(-22.75, -0.27) * mm});
            skPoint(sketch, "E24.21.2", {"position": v(-22.22, 0.39) * mm});
            skPoint(sketch, "E24.21.3", {"position": v(-22.22, -0.39) * mm});
            skPoint(sketch, "E24.21.4", {"position": v(-21.7, 0.4) * mm});
            skPoint(sketch, "E24.21.5", {"position": v(-21.7, -0.4) * mm});
            skArc(sketch, "E24.21.6", {"start": v(-21.7, 0.4) * mm, "mid": v(-21.69, 0.6) * mm, "end": v(-21.68, 0.81) * mm});
            skArc(sketch, "E24.21.7", {"start": v(-21.7, -0.4) * mm, "mid": v(-22.23, -0.39) * mm, "end": v(-22.75, -0.27) * mm});
            skArc(sketch, "E24.21.8", {"start": v(-21.7, 0.4) * mm, "mid": v(-22.23, 0.39) * mm, "end": v(-22.75, 0.27) * mm});
            skArc(sketch, "E24.21.9", {"start": v(-21.7, -0.4) * mm, "mid": v(-21.69, -0.6) * mm, "end": v(-21.68, -0.81) * mm});
            skArc(sketch, "E24.21.10", {"start": v(-22.75, 0) * mm, "mid": v(-22.75, 0.13) * mm, "end": v(-22.75, 0.27) * mm});
            skArc(sketch, "E24.21.11", {"start": v(-22.75, 0) * mm, "mid": v(-22.75, -0.13) * mm, "end": v(-22.75, -0.27) * mm});
            skPoint(sketch, "E24.22.0", {"position": v(-22.7, -1.44) * mm});
            skPoint(sketch, "E24.22.1", {"position": v(-22.67, -1.97) * mm});
            skPoint(sketch, "E24.22.2", {"position": v(-22.19, -1.27) * mm});
            skPoint(sketch, "E24.22.3", {"position": v(-22.13, -2.05) * mm});
            skPoint(sketch, "E24.22.4", {"position": v(-21.66, -1.22) * mm});
            skPoint(sketch, "E24.22.5", {"position": v(-21.6, -2.03) * mm});
            skArc(sketch, "E24.22.6", {"start": v(-21.66, -1.22) * mm, "mid": v(-21.67, -1.01) * mm, "end": v(-21.68, -0.81) * mm});
            skArc(sketch, "E24.22.7", {"start": v(-21.6, -2.03) * mm, "mid": v(-22.14, -2.05) * mm, "end": v(-22.67, -1.97) * mm});
            skArc(sketch, "E24.22.8", {"start": v(-21.66, -1.22) * mm, "mid": v(-22.2, -1.27) * mm, "end": v(-22.7, -1.44) * mm});
            skArc(sketch, "E24.22.9", {"start": v(-21.6, -2.03) * mm, "mid": v(-21.58, -2.23) * mm, "end": v(-21.56, -2.43) * mm});
            skArc(sketch, "E24.22.10", {"start": v(-22.7, -1.7) * mm, "mid": v(-22.7, -1.57) * mm, "end": v(-22.7, -1.44) * mm});
            skArc(sketch, "E24.22.11", {"start": v(-22.7, -1.7) * mm, "mid": v(-22.68, -1.83) * mm, "end": v(-22.67, -1.97) * mm});
            skPoint(sketch, "E24.23.0", {"position": v(-22.54, -3.13) * mm});
            skPoint(sketch, "E24.23.1", {"position": v(-22.46, -3.65) * mm});
            skPoint(sketch, "E24.23.2", {"position": v(-22.03, -2.93) * mm});
            skPoint(sketch, "E24.23.3", {"position": v(-21.92, -3.7) * mm});
            skPoint(sketch, "E24.23.4", {"position": v(-21.51, -2.83) * mm});
            skPoint(sketch, "E24.23.5", {"position": v(-21.39, -3.63) * mm});
            skArc(sketch, "E24.23.6", {"start": v(-21.51, -2.83) * mm, "mid": v(-21.54, -2.63) * mm, "end": v(-21.56, -2.43) * mm});
            skArc(sketch, "E24.23.7", {"start": v(-21.39, -3.63) * mm, "mid": v(-21.92, -3.7) * mm, "end": v(-22.46, -3.65) * mm});
            skArc(sketch, "E24.23.8", {"start": v(-21.51, -2.83) * mm, "mid": v(-22.04, -2.93) * mm, "end": v(-22.54, -3.13) * mm});
            skArc(sketch, "E24.23.9", {"start": v(-21.39, -3.63) * mm, "mid": v(-21.35, -3.83) * mm, "end": v(-21.32, -4.03) * mm});
            skArc(sketch, "E24.23.10", {"start": v(-22.5, -3.4) * mm, "mid": v(-22.52, -3.26) * mm, "end": v(-22.54, -3.13) * mm});
            skArc(sketch, "E24.23.11", {"start": v(-22.5, -3.4) * mm, "mid": v(-22.48, -3.52) * mm, "end": v(-22.46, -3.65) * mm});
            skPoint(sketch, "E24.24.0", {"position": v(-22.24, -4.8) * mm});
            skPoint(sketch, "E24.24.1", {"position": v(-22.12, -5.32) * mm});
            skPoint(sketch, "E24.24.2", {"position": v(-21.75, -4.56) * mm});
            skPoint(sketch, "E24.24.3", {"position": v(-21.58, -5.32) * mm});
            skPoint(sketch, "E24.24.4", {"position": v(-21.24, -4.43) * mm});
            skPoint(sketch, "E24.24.5", {"position": v(-21.06, -5.22) * mm});
            skArc(sketch, "E24.24.6", {"start": v(-21.24, -4.43) * mm, "mid": v(-21.28, -4.23) * mm, "end": v(-21.32, -4.03) * mm});
            skArc(sketch, "E24.24.7", {"start": v(-21.06, -5.22) * mm, "mid": v(-21.59, -5.33) * mm, "end": v(-22.12, -5.32) * mm});
            skArc(sketch, "E24.24.8", {"start": v(-21.24, -4.43) * mm, "mid": v(-21.76, -4.57) * mm, "end": v(-22.24, -4.8) * mm});
            skArc(sketch, "E24.24.9", {"start": v(-21.06, -5.22) * mm, "mid": v(-21, -5.42) * mm, "end": v(-20.96, -5.62) * mm});
            skArc(sketch, "E24.24.10", {"start": v(-22.18, -5.06) * mm, "mid": v(-22.21, -4.93) * mm, "end": v(-22.24, -4.8) * mm});
            skArc(sketch, "E24.24.11", {"start": v(-22.18, -5.06) * mm, "mid": v(-22.15, -5.2) * mm, "end": v(-22.12, -5.32) * mm});
            skPoint(sketch, "E24.25.0", {"position": v(-21.82, -6.45) * mm});
            skPoint(sketch, "E24.25.1", {"position": v(-21.66, -6.96) * mm});
            skPoint(sketch, "E24.25.2", {"position": v(-21.35, -6.18) * mm});
            skPoint(sketch, "E24.25.3", {"position": v(-21.12, -6.92) * mm});
            skPoint(sketch, "E24.25.4", {"position": v(-20.85, -6) * mm});
            skPoint(sketch, "E24.25.5", {"position": v(-20.6, -6.78) * mm});
            skArc(sketch, "E24.25.6", {"start": v(-20.85, -6) * mm, "mid": v(-20.9, -5.81) * mm, "end": v(-20.96, -5.62) * mm});
            skArc(sketch, "E24.25.7", {"start": v(-20.6, -6.78) * mm, "mid": v(-21.13, -6.92) * mm, "end": v(-21.66, -6.96) * mm});
            skArc(sketch, "E24.25.8", {"start": v(-20.85, -6) * mm, "mid": v(-21.36, -6.18) * mm, "end": v(-21.82, -6.45) * mm});
            skArc(sketch, "E24.25.9", {"start": v(-20.6, -6.78) * mm, "mid": v(-20.54, -6.97) * mm, "end": v(-20.48, -7.17) * mm});
            skArc(sketch, "E24.25.10", {"start": v(-21.74, -6.7) * mm, "mid": v(-21.78, -6.58) * mm, "end": v(-21.82, -6.45) * mm});
            skArc(sketch, "E24.25.11", {"start": v(-21.74, -6.7) * mm, "mid": v(-21.7, -6.83) * mm, "end": v(-21.66, -6.96) * mm});
            skPoint(sketch, "E24.26.0", {"position": v(-21.28, -8.06) * mm});
            skPoint(sketch, "E24.26.1", {"position": v(-21.08, -8.56) * mm});
            skPoint(sketch, "E24.26.2", {"position": v(-20.83, -7.76) * mm});
            skPoint(sketch, "E24.26.3", {"position": v(-20.54, -8.48) * mm});
            skPoint(sketch, "E24.26.4", {"position": v(-20.34, -7.55) * mm});
            skPoint(sketch, "E24.26.5", {"position": v(-20.04, -8.3) * mm});
            skArc(sketch, "E24.26.6", {"start": v(-20.34, -7.55) * mm, "mid": v(-20.41, -7.36) * mm, "end": v(-20.48, -7.17) * mm});
            skArc(sketch, "E24.26.7", {"start": v(-20.04, -8.3) * mm, "mid": v(-20.55, -8.48) * mm, "end": v(-21.08, -8.56) * mm});
            skArc(sketch, "E24.26.8", {"start": v(-20.34, -7.55) * mm, "mid": v(-20.83, -7.76) * mm, "end": v(-21.28, -8.06) * mm});
            skArc(sketch, "E24.26.9", {"start": v(-20.04, -8.3) * mm, "mid": v(-19.97, -8.49) * mm, "end": v(-19.89, -8.68) * mm});
            skArc(sketch, "E24.26.10", {"start": v(-21.18, -8.31) * mm, "mid": v(-21.23, -8.19) * mm, "end": v(-21.28, -8.06) * mm});
            skArc(sketch, "E24.26.11", {"start": v(-21.18, -8.31) * mm, "mid": v(-21.13, -8.44) * mm, "end": v(-21.08, -8.56) * mm});
            skPoint(sketch, "E24.27.0", {"position": v(-20.61, -9.63) * mm});
            skPoint(sketch, "E24.27.1", {"position": v(-20.38, -10.11) * mm});
            skPoint(sketch, "E24.27.2", {"position": v(-20.2, -9.3) * mm});
            skPoint(sketch, "E24.27.3", {"position": v(-19.85, -10) * mm});
            skPoint(sketch, "E24.27.4", {"position": v(-19.72, -9.05) * mm});
            skPoint(sketch, "E24.27.5", {"position": v(-19.37, -9.78) * mm});
            skArc(sketch, "E24.27.6", {"start": v(-19.72, -9.05) * mm, "mid": v(-19.8, -8.86) * mm, "end": v(-19.89, -8.68) * mm});
            skArc(sketch, "E24.27.7", {"start": v(-19.37, -9.78) * mm, "mid": v(-19.86, -10) * mm, "end": v(-20.38, -10.11) * mm});
            skArc(sketch, "E24.27.8", {"start": v(-19.72, -9.05) * mm, "mid": v(-20.2, -9.3) * mm, "end": v(-20.61, -9.63) * mm});
            skArc(sketch, "E24.27.9", {"start": v(-19.37, -9.78) * mm, "mid": v(-19.28, -9.96) * mm, "end": v(-19.18, -10.14) * mm});
            skArc(sketch, "E24.27.10", {"start": v(-20.5, -9.87) * mm, "mid": v(-20.56, -9.75) * mm, "end": v(-20.61, -9.63) * mm});
            skArc(sketch, "E24.27.11", {"start": v(-20.5, -9.87) * mm, "mid": v(-20.44, -10) * mm, "end": v(-20.38, -10.11) * mm});
            skPoint(sketch, "E24.28.0", {"position": v(-19.84, -11.15) * mm});
            skPoint(sketch, "E24.28.1", {"position": v(-19.57, -11.6) * mm});
            skPoint(sketch, "E24.28.2", {"position": v(-19.44, -10.77) * mm});
            skPoint(sketch, "E24.28.3", {"position": v(-19.05, -11.45) * mm});
            skPoint(sketch, "E24.28.4", {"position": v(-18.99, -10.5) * mm});
            skPoint(sketch, "E24.28.5", {"position": v(-18.58, -11.2) * mm});
            skArc(sketch, "E24.28.6", {"start": v(-18.99, -10.5) * mm, "mid": v(-19.09, -10.32) * mm, "end": v(-19.18, -10.14) * mm});
            skArc(sketch, "E24.28.7", {"start": v(-18.58, -11.2) * mm, "mid": v(-19.06, -11.45) * mm, "end": v(-19.57, -11.6) * mm});
            skArc(sketch, "E24.28.8", {"start": v(-18.99, -10.5) * mm, "mid": v(-19.45, -10.78) * mm, "end": v(-19.84, -11.15) * mm});
            skArc(sketch, "E24.28.9", {"start": v(-18.58, -11.2) * mm, "mid": v(-18.48, -11.37) * mm, "end": v(-18.37, -11.54) * mm});
            skArc(sketch, "E24.28.10", {"start": v(-19.7, -11.38) * mm, "mid": v(-19.77, -11.26) * mm, "end": v(-19.84, -11.15) * mm});
            skArc(sketch, "E24.28.11", {"start": v(-19.7, -11.38) * mm, "mid": v(-19.64, -11.5) * mm, "end": v(-19.57, -11.6) * mm});
            skPoint(sketch, "E24.29.0", {"position": v(-18.95, -12.6) * mm});
            skPoint(sketch, "E24.29.1", {"position": v(-18.65, -13.04) * mm});
            skPoint(sketch, "E24.29.2", {"position": v(-18.58, -12.2) * mm});
            skPoint(sketch, "E24.29.3", {"position": v(-18.14, -12.84) * mm});
            skPoint(sketch, "E24.29.4", {"position": v(-18.15, -11.88) * mm});
            skPoint(sketch, "E24.29.5", {"position": v(-17.7, -12.55) * mm});
            skArc(sketch, "E24.29.6", {"start": v(-18.15, -11.88) * mm, "mid": v(-18.26, -11.71) * mm, "end": v(-18.37, -11.54) * mm});
            skArc(sketch, "E24.29.7", {"start": v(-17.7, -12.55) * mm, "mid": v(-18.15, -12.84) * mm, "end": v(-18.65, -13.04) * mm});
            skArc(sketch, "E24.29.8", {"start": v(-18.15, -11.88) * mm, "mid": v(-18.59, -12.2) * mm, "end": v(-18.95, -12.6) * mm});
            skArc(sketch, "E24.29.9", {"start": v(-17.7, -12.55) * mm, "mid": v(-17.58, -12.72) * mm, "end": v(-17.46, -12.88) * mm});
            skArc(sketch, "E24.29.10", {"start": v(-18.8, -12.82) * mm, "mid": v(-18.87, -12.7) * mm, "end": v(-18.95, -12.6) * mm});
            skArc(sketch, "E24.29.11", {"start": v(-18.8, -12.82) * mm, "mid": v(-18.73, -12.93) * mm, "end": v(-18.65, -13.04) * mm});
            skPoint(sketch, "E24.30.0", {"position": v(-17.95, -13.98) * mm});
            skPoint(sketch, "E24.30.1", {"position": v(-17.62, -14.4) * mm});
            skPoint(sketch, "E24.30.2", {"position": v(-17.62, -13.55) * mm});
            skPoint(sketch, "E24.30.3", {"position": v(-17.13, -14.16) * mm});
            skPoint(sketch, "E24.30.4", {"position": v(-17.21, -13.2) * mm});
            skPoint(sketch, "E24.30.5", {"position": v(-16.7, -13.84) * mm});
            skArc(sketch, "E24.30.6", {"start": v(-17.21, -13.2) * mm, "mid": v(-17.34, -13.05) * mm, "end": v(-17.46, -12.88) * mm});
            skArc(sketch, "E24.30.7", {"start": v(-16.7, -13.84) * mm, "mid": v(-17.14, -14.16) * mm, "end": v(-17.62, -14.4) * mm});
            skArc(sketch, "E24.30.8", {"start": v(-17.21, -13.2) * mm, "mid": v(-17.62, -13.56) * mm, "end": v(-17.95, -13.98) * mm});
            skArc(sketch, "E24.30.9", {"start": v(-16.7, -13.84) * mm, "mid": v(-16.58, -14) * mm, "end": v(-16.44, -14.15) * mm});
            skArc(sketch, "E24.30.10", {"start": v(-17.79, -14.19) * mm, "mid": v(-17.87, -14.08) * mm, "end": v(-17.95, -13.98) * mm});
            skArc(sketch, "E24.30.11", {"start": v(-17.79, -14.19) * mm, "mid": v(-17.7, -14.3) * mm, "end": v(-17.62, -14.4) * mm});
            skPoint(sketch, "E24.31.0", {"position": v(-16.86, -15.28) * mm});
            skPoint(sketch, "E24.31.1", {"position": v(-16.5, -15.67) * mm});
            skPoint(sketch, "E24.31.2", {"position": v(-16.55, -14.83) * mm});
            skPoint(sketch, "E24.31.3", {"position": v(-16.02, -15.4) * mm});
            skPoint(sketch, "E24.31.4", {"position": v(-16.18, -14.46) * mm});
            skPoint(sketch, "E24.31.5", {"position": v(-15.63, -15.05) * mm});
            skArc(sketch, "E24.31.6", {"start": v(-16.18, -14.46) * mm, "mid": v(-16.31, -14.3) * mm, "end": v(-16.44, -14.15) * mm});
            skArc(sketch, "E24.31.7", {"start": v(-15.63, -15.05) * mm, "mid": v(-16.03, -15.4) * mm, "end": v(-16.5, -15.67) * mm});
            skArc(sketch, "E24.31.8", {"start": v(-16.18, -14.46) * mm, "mid": v(-16.56, -14.83) * mm, "end": v(-16.86, -15.28) * mm});
            skArc(sketch, "E24.31.9", {"start": v(-15.63, -15.05) * mm, "mid": v(-15.48, -15.2) * mm, "end": v(-15.34, -15.34) * mm});
            skArc(sketch, "E24.31.10", {"start": v(-16.68, -15.48) * mm, "mid": v(-16.77, -15.38) * mm, "end": v(-16.86, -15.28) * mm});
            skArc(sketch, "E24.31.11", {"start": v(-16.68, -15.48) * mm, "mid": v(-16.59, -15.57) * mm, "end": v(-16.5, -15.67) * mm});
            skPoint(sketch, "E24.32.0", {"position": v(-15.67, -16.5) * mm});
            skPoint(sketch, "E24.32.1", {"position": v(-15.28, -16.86) * mm});
            skPoint(sketch, "E24.32.2", {"position": v(-15.4, -16.02) * mm});
            skPoint(sketch, "E24.32.3", {"position": v(-14.83, -16.55) * mm});
            skPoint(sketch, "E24.32.4", {"position": v(-15.05, -15.63) * mm});
            skPoint(sketch, "E24.32.5", {"position": v(-14.46, -16.18) * mm});
            skArc(sketch, "E24.32.6", {"start": v(-15.05, -15.63) * mm, "mid": v(-15.2, -15.48) * mm, "end": v(-15.34, -15.34) * mm});
            skArc(sketch, "E24.32.7", {"start": v(-14.46, -16.18) * mm, "mid": v(-14.83, -16.56) * mm, "end": v(-15.28, -16.86) * mm});
            skArc(sketch, "E24.32.8", {"start": v(-15.05, -15.63) * mm, "mid": v(-15.4, -16.03) * mm, "end": v(-15.67, -16.5) * mm});
            skArc(sketch, "E24.32.9", {"start": v(-14.46, -16.18) * mm, "mid": v(-14.3, -16.31) * mm, "end": v(-14.15, -16.44) * mm});
            skArc(sketch, "E24.32.10", {"start": v(-15.48, -16.68) * mm, "mid": v(-15.57, -16.59) * mm, "end": v(-15.67, -16.5) * mm});
            skArc(sketch, "E24.32.11", {"start": v(-15.48, -16.68) * mm, "mid": v(-15.38, -16.77) * mm, "end": v(-15.28, -16.86) * mm});
            skPoint(sketch, "E24.33.0", {"position": v(-14.4, -17.62) * mm});
            skPoint(sketch, "E24.33.1", {"position": v(-13.98, -17.95) * mm});
            skPoint(sketch, "E24.33.2", {"position": v(-14.16, -17.13) * mm});
            skPoint(sketch, "E24.33.3", {"position": v(-13.55, -17.62) * mm});
            skPoint(sketch, "E24.33.4", {"position": v(-13.84, -16.7) * mm});
            skPoint(sketch, "E24.33.5", {"position": v(-13.2, -17.21) * mm});
            skArc(sketch, "E24.33.6", {"start": v(-13.84, -16.7) * mm, "mid": v(-14, -16.58) * mm, "end": v(-14.15, -16.44) * mm});
            skArc(sketch, "E24.33.7", {"start": v(-13.2, -17.21) * mm, "mid": v(-13.56, -17.62) * mm, "end": v(-13.98, -17.95) * mm});
            skArc(sketch, "E24.33.8", {"start": v(-13.84, -16.7) * mm, "mid": v(-14.16, -17.14) * mm, "end": v(-14.4, -17.62) * mm});
            skArc(sketch, "E24.33.9", {"start": v(-13.2, -17.21) * mm, "mid": v(-13.05, -17.34) * mm, "end": v(-12.88, -17.46) * mm});
            skArc(sketch, "E24.33.10", {"start": v(-14.19, -17.79) * mm, "mid": v(-14.3, -17.7) * mm, "end": v(-14.4, -17.62) * mm});
            skArc(sketch, "E24.33.11", {"start": v(-14.19, -17.79) * mm, "mid": v(-14.08, -17.87) * mm, "end": v(-13.98, -17.95) * mm});
            skPoint(sketch, "E24.34.0", {"position": v(-13.04, -18.65) * mm});
            skPoint(sketch, "E24.34.1", {"position": v(-12.6, -18.95) * mm});
            skPoint(sketch, "E24.34.2", {"position": v(-12.84, -18.14) * mm});
            skPoint(sketch, "E24.34.3", {"position": v(-12.2, -18.58) * mm});
            skPoint(sketch, "E24.34.4", {"position": v(-12.55, -17.7) * mm});
            skPoint(sketch, "E24.34.5", {"position": v(-11.88, -18.15) * mm});
            skArc(sketch, "E24.34.6", {"start": v(-12.55, -17.7) * mm, "mid": v(-12.72, -17.58) * mm, "end": v(-12.88, -17.46) * mm});
            skArc(sketch, "E24.34.7", {"start": v(-11.88, -18.15) * mm, "mid": v(-12.2, -18.59) * mm, "end": v(-12.6, -18.95) * mm});
            skArc(sketch, "E24.34.8", {"start": v(-12.55, -17.7) * mm, "mid": v(-12.84, -18.15) * mm, "end": v(-13.04, -18.65) * mm});
            skArc(sketch, "E24.34.9", {"start": v(-11.88, -18.15) * mm, "mid": v(-11.71, -18.26) * mm, "end": v(-11.54, -18.37) * mm});
            skArc(sketch, "E24.34.10", {"start": v(-12.82, -18.8) * mm, "mid": v(-12.93, -18.73) * mm, "end": v(-13.04, -18.65) * mm});
            skArc(sketch, "E24.34.11", {"start": v(-12.82, -18.8) * mm, "mid": v(-12.7, -18.87) * mm, "end": v(-12.6, -18.95) * mm});
            skPoint(sketch, "E24.35.0", {"position": v(-11.6, -19.57) * mm});
            skPoint(sketch, "E24.35.1", {"position": v(-11.15, -19.84) * mm});
            skPoint(sketch, "E24.35.2", {"position": v(-11.45, -19.05) * mm});
            skPoint(sketch, "E24.35.3", {"position": v(-10.77, -19.44) * mm});
            skPoint(sketch, "E24.35.4", {"position": v(-11.2, -18.58) * mm});
            skPoint(sketch, "E24.35.5", {"position": v(-10.5, -18.99) * mm});
            skArc(sketch, "E24.35.6", {"start": v(-11.2, -18.58) * mm, "mid": v(-11.37, -18.48) * mm, "end": v(-11.54, -18.37) * mm});
            skArc(sketch, "E24.35.7", {"start": v(-10.5, -18.99) * mm, "mid": v(-10.78, -19.45) * mm, "end": v(-11.15, -19.84) * mm});
            skArc(sketch, "E24.35.8", {"start": v(-11.2, -18.58) * mm, "mid": v(-11.45, -19.06) * mm, "end": v(-11.6, -19.57) * mm});
            skArc(sketch, "E24.35.9", {"start": v(-10.5, -18.99) * mm, "mid": v(-10.32, -19.09) * mm, "end": v(-10.14, -19.18) * mm});
            skArc(sketch, "E24.35.10", {"start": v(-11.38, -19.7) * mm, "mid": v(-11.5, -19.64) * mm, "end": v(-11.6, -19.57) * mm});
            skArc(sketch, "E24.35.11", {"start": v(-11.38, -19.7) * mm, "mid": v(-11.26, -19.77) * mm, "end": v(-11.15, -19.84) * mm});
            skPoint(sketch, "E24.36.0", {"position": v(-10.11, -20.38) * mm});
            skPoint(sketch, "E24.36.1", {"position": v(-9.63, -20.61) * mm});
            skPoint(sketch, "E24.36.2", {"position": v(-10, -19.85) * mm});
            skPoint(sketch, "E24.36.3", {"position": v(-9.3, -20.2) * mm});
            skPoint(sketch, "E24.36.4", {"position": v(-9.78, -19.37) * mm});
            skPoint(sketch, "E24.36.5", {"position": v(-9.05, -19.72) * mm});
            skArc(sketch, "E24.36.6", {"start": v(-9.78, -19.37) * mm, "mid": v(-9.96, -19.28) * mm, "end": v(-10.14, -19.18) * mm});
            skArc(sketch, "E24.36.7", {"start": v(-9.05, -19.72) * mm, "mid": v(-9.3, -20.2) * mm, "end": v(-9.63, -20.61) * mm});
            skArc(sketch, "E24.36.8", {"start": v(-9.78, -19.37) * mm, "mid": v(-10, -19.86) * mm, "end": v(-10.11, -20.38) * mm});
            skArc(sketch, "E24.36.9", {"start": v(-9.05, -19.72) * mm, "mid": v(-8.86, -19.8) * mm, "end": v(-8.68, -19.89) * mm});
            skArc(sketch, "E24.36.10", {"start": v(-9.87, -20.5) * mm, "mid": v(-10, -20.44) * mm, "end": v(-10.11, -20.38) * mm});
            skArc(sketch, "E24.36.11", {"start": v(-9.87, -20.5) * mm, "mid": v(-9.75, -20.56) * mm, "end": v(-9.63, -20.61) * mm});
            skPoint(sketch, "E24.37.0", {"position": v(-8.56, -21.08) * mm});
            skPoint(sketch, "E24.37.1", {"position": v(-8.06, -21.28) * mm});
            skPoint(sketch, "E24.37.2", {"position": v(-8.48, -20.54) * mm});
            skPoint(sketch, "E24.37.3", {"position": v(-7.76, -20.83) * mm});
            skPoint(sketch, "E24.37.4", {"position": v(-8.3, -20.04) * mm});
            skPoint(sketch, "E24.37.5", {"position": v(-7.55, -20.34) * mm});
            skArc(sketch, "E24.37.6", {"start": v(-8.3, -20.04) * mm, "mid": v(-8.49, -19.97) * mm, "end": v(-8.68, -19.89) * mm});
            skArc(sketch, "E24.37.7", {"start": v(-7.55, -20.34) * mm, "mid": v(-7.76, -20.83) * mm, "end": v(-8.06, -21.28) * mm});
            skArc(sketch, "E24.37.8", {"start": v(-8.3, -20.04) * mm, "mid": v(-8.48, -20.55) * mm, "end": v(-8.56, -21.08) * mm});
            skArc(sketch, "E24.37.9", {"start": v(-7.55, -20.34) * mm, "mid": v(-7.36, -20.41) * mm, "end": v(-7.17, -20.48) * mm});
            skArc(sketch, "E24.37.10", {"start": v(-8.31, -21.18) * mm, "mid": v(-8.44, -21.13) * mm, "end": v(-8.56, -21.08) * mm});
            skArc(sketch, "E24.37.11", {"start": v(-8.31, -21.18) * mm, "mid": v(-8.19, -21.23) * mm, "end": v(-8.06, -21.28) * mm});
            skPoint(sketch, "E24.38.0", {"position": v(-6.96, -21.66) * mm});
            skPoint(sketch, "E24.38.1", {"position": v(-6.45, -21.82) * mm});
            skPoint(sketch, "E24.38.2", {"position": v(-6.92, -21.12) * mm});
            skPoint(sketch, "E24.38.3", {"position": v(-6.18, -21.35) * mm});
            skPoint(sketch, "E24.38.4", {"position": v(-6.78, -20.6) * mm});
            skPoint(sketch, "E24.38.5", {"position": v(-6, -20.85) * mm});
            skArc(sketch, "E24.38.6", {"start": v(-6.78, -20.6) * mm, "mid": v(-6.97, -20.54) * mm, "end": v(-7.17, -20.48) * mm});
            skArc(sketch, "E24.38.7", {"start": v(-6, -20.85) * mm, "mid": v(-6.18, -21.36) * mm, "end": v(-6.45, -21.82) * mm});
            skArc(sketch, "E24.38.8", {"start": v(-6.78, -20.6) * mm, "mid": v(-6.92, -21.13) * mm, "end": v(-6.96, -21.66) * mm});
            skArc(sketch, "E24.38.9", {"start": v(-6, -20.85) * mm, "mid": v(-5.81, -20.9) * mm, "end": v(-5.62, -20.96) * mm});
            skArc(sketch, "E24.38.10", {"start": v(-6.7, -21.74) * mm, "mid": v(-6.83, -21.7) * mm, "end": v(-6.96, -21.66) * mm});
            skArc(sketch, "E24.38.11", {"start": v(-6.7, -21.74) * mm, "mid": v(-6.58, -21.78) * mm, "end": v(-6.45, -21.82) * mm});
            skPoint(sketch, "E24.39.0", {"position": v(-5.32, -22.12) * mm});
            skPoint(sketch, "E24.39.1", {"position": v(-4.8, -22.24) * mm});
            skPoint(sketch, "E24.39.2", {"position": v(-5.32, -21.58) * mm});
            skPoint(sketch, "E24.39.3", {"position": v(-4.56, -21.75) * mm});
            skPoint(sketch, "E24.39.4", {"position": v(-5.22, -21.06) * mm});
            skPoint(sketch, "E24.39.5", {"position": v(-4.43, -21.24) * mm});
            skArc(sketch, "E24.39.6", {"start": v(-5.22, -21.06) * mm, "mid": v(-5.42, -21) * mm, "end": v(-5.62, -20.96) * mm});
            skArc(sketch, "E24.39.7", {"start": v(-4.43, -21.24) * mm, "mid": v(-4.57, -21.76) * mm, "end": v(-4.8, -22.24) * mm});
            skArc(sketch, "E24.39.8", {"start": v(-5.22, -21.06) * mm, "mid": v(-5.33, -21.59) * mm, "end": v(-5.32, -22.12) * mm});
            skArc(sketch, "E24.39.9", {"start": v(-4.43, -21.24) * mm, "mid": v(-4.23, -21.28) * mm, "end": v(-4.03, -21.32) * mm});
            skArc(sketch, "E24.39.10", {"start": v(-5.06, -22.18) * mm, "mid": v(-5.2, -22.15) * mm, "end": v(-5.32, -22.12) * mm});
            skArc(sketch, "E24.39.11", {"start": v(-5.06, -22.18) * mm, "mid": v(-4.93, -22.21) * mm, "end": v(-4.8, -22.24) * mm});
            skPoint(sketch, "E24.40.0", {"position": v(-3.65, -22.46) * mm});
            skPoint(sketch, "E24.40.1", {"position": v(-3.13, -22.54) * mm});
            skPoint(sketch, "E24.40.2", {"position": v(-3.7, -21.92) * mm});
            skPoint(sketch, "E24.40.3", {"position": v(-2.93, -22.03) * mm});
            skPoint(sketch, "E24.40.4", {"position": v(-3.63, -21.39) * mm});
            skPoint(sketch, "E24.40.5", {"position": v(-2.83, -21.51) * mm});
            skArc(sketch, "E24.40.6", {"start": v(-3.63, -21.39) * mm, "mid": v(-3.83, -21.35) * mm, "end": v(-4.03, -21.32) * mm});
            skArc(sketch, "E24.40.7", {"start": v(-2.83, -21.51) * mm, "mid": v(-2.93, -22.04) * mm, "end": v(-3.13, -22.54) * mm});
            skArc(sketch, "E24.40.8", {"start": v(-3.63, -21.39) * mm, "mid": v(-3.7, -21.92) * mm, "end": v(-3.65, -22.46) * mm});
            skArc(sketch, "E24.40.9", {"start": v(-2.83, -21.51) * mm, "mid": v(-2.63, -21.54) * mm, "end": v(-2.43, -21.56) * mm});
            skArc(sketch, "E24.40.10", {"start": v(-3.4, -22.5) * mm, "mid": v(-3.52, -22.48) * mm, "end": v(-3.65, -22.46) * mm});
            skArc(sketch, "E24.40.11", {"start": v(-3.4, -22.5) * mm, "mid": v(-3.26, -22.52) * mm, "end": v(-3.13, -22.54) * mm});
            skPoint(sketch, "E24.41.0", {"position": v(-1.97, -22.67) * mm});
            skPoint(sketch, "E24.41.1", {"position": v(-1.44, -22.7) * mm});
            skPoint(sketch, "E24.41.2", {"position": v(-2.05, -22.13) * mm});
            skPoint(sketch, "E24.41.3", {"position": v(-1.27, -22.19) * mm});
            skPoint(sketch, "E24.41.4", {"position": v(-2.03, -21.6) * mm});
            skPoint(sketch, "E24.41.5", {"position": v(-1.22, -21.66) * mm});
            skArc(sketch, "E24.41.6", {"start": v(-2.03, -21.6) * mm, "mid": v(-2.23, -21.58) * mm, "end": v(-2.43, -21.56) * mm});
            skArc(sketch, "E24.41.7", {"start": v(-1.22, -21.66) * mm, "mid": v(-1.27, -22.2) * mm, "end": v(-1.44, -22.7) * mm});
            skArc(sketch, "E24.41.8", {"start": v(-2.03, -21.6) * mm, "mid": v(-2.05, -22.14) * mm, "end": v(-1.97, -22.67) * mm});
            skArc(sketch, "E24.41.9", {"start": v(-1.22, -21.66) * mm, "mid": v(-1.01, -21.67) * mm, "end": v(-0.81, -21.68) * mm});
            skArc(sketch, "E24.41.10", {"start": v(-1.7, -22.7) * mm, "mid": v(-1.83, -22.68) * mm, "end": v(-1.97, -22.67) * mm});
            skArc(sketch, "E24.41.11", {"start": v(-1.7, -22.7) * mm, "mid": v(-1.57, -22.7) * mm, "end": v(-1.44, -22.7) * mm});
            skPoint(sketch, "E24.42.0", {"position": v(-0.27, -22.75) * mm});
            skPoint(sketch, "E24.42.1", {"position": v(0.27, -22.75) * mm});
            skPoint(sketch, "E24.42.2", {"position": v(-0.39, -22.22) * mm});
            skPoint(sketch, "E24.42.3", {"position": v(0.39, -22.22) * mm});
            skPoint(sketch, "E24.42.4", {"position": v(-0.4, -21.7) * mm});
            skPoint(sketch, "E24.42.5", {"position": v(0.4, -21.7) * mm});
            skArc(sketch, "E24.42.6", {"start": v(-0.4, -21.7) * mm, "mid": v(-0.6, -21.69) * mm, "end": v(-0.81, -21.68) * mm});
            skArc(sketch, "E24.42.7", {"start": v(0.4, -21.7) * mm, "mid": v(0.39, -22.23) * mm, "end": v(0.27, -22.75) * mm});
            skArc(sketch, "E24.42.8", {"start": v(-0.4, -21.7) * mm, "mid": v(-0.39, -22.23) * mm, "end": v(-0.27, -22.75) * mm});
            skArc(sketch, "E24.42.9", {"start": v(0.4, -21.7) * mm, "mid": v(0.6, -21.69) * mm, "end": v(0.81, -21.68) * mm});
            skArc(sketch, "E24.42.10", {"start": v(0, -22.75) * mm, "mid": v(-0.13, -22.75) * mm, "end": v(-0.27, -22.75) * mm});
            skArc(sketch, "E24.42.11", {"start": v(0, -22.75) * mm, "mid": v(0.13, -22.75) * mm, "end": v(0.27, -22.75) * mm});
            skPoint(sketch, "E24.43.0", {"position": v(1.44, -22.7) * mm});
            skPoint(sketch, "E24.43.1", {"position": v(1.97, -22.67) * mm});
            skPoint(sketch, "E24.43.2", {"position": v(1.27, -22.19) * mm});
            skPoint(sketch, "E24.43.3", {"position": v(2.05, -22.13) * mm});
            skPoint(sketch, "E24.43.4", {"position": v(1.22, -21.66) * mm});
            skPoint(sketch, "E24.43.5", {"position": v(2.03, -21.6) * mm});
            skArc(sketch, "E24.43.6", {"start": v(1.22, -21.66) * mm, "mid": v(1.01, -21.67) * mm, "end": v(0.81, -21.68) * mm});
            skArc(sketch, "E24.43.7", {"start": v(2.03, -21.6) * mm, "mid": v(2.05, -22.14) * mm, "end": v(1.97, -22.67) * mm});
            skArc(sketch, "E24.43.8", {"start": v(1.22, -21.66) * mm, "mid": v(1.27, -22.2) * mm, "end": v(1.44, -22.7) * mm});
            skArc(sketch, "E24.43.9", {"start": v(2.03, -21.6) * mm, "mid": v(2.23, -21.58) * mm, "end": v(2.43, -21.56) * mm});
            skArc(sketch, "E24.43.10", {"start": v(1.7, -22.7) * mm, "mid": v(1.57, -22.7) * mm, "end": v(1.44, -22.7) * mm});
            skArc(sketch, "E24.43.11", {"start": v(1.7, -22.7) * mm, "mid": v(1.83, -22.68) * mm, "end": v(1.97, -22.67) * mm});
            skPoint(sketch, "E24.44.0", {"position": v(3.13, -22.54) * mm});
            skPoint(sketch, "E24.44.1", {"position": v(3.65, -22.46) * mm});
            skPoint(sketch, "E24.44.2", {"position": v(2.93, -22.03) * mm});
            skPoint(sketch, "E24.44.3", {"position": v(3.7, -21.92) * mm});
            skPoint(sketch, "E24.44.4", {"position": v(2.83, -21.51) * mm});
            skPoint(sketch, "E24.44.5", {"position": v(3.63, -21.39) * mm});
            skArc(sketch, "E24.44.6", {"start": v(2.83, -21.51) * mm, "mid": v(2.63, -21.54) * mm, "end": v(2.43, -21.56) * mm});
            skArc(sketch, "E24.44.7", {"start": v(3.63, -21.39) * mm, "mid": v(3.7, -21.92) * mm, "end": v(3.65, -22.46) * mm});
            skArc(sketch, "E24.44.8", {"start": v(2.83, -21.51) * mm, "mid": v(2.93, -22.04) * mm, "end": v(3.13, -22.54) * mm});
            skArc(sketch, "E24.44.9", {"start": v(3.63, -21.39) * mm, "mid": v(3.83, -21.35) * mm, "end": v(4.03, -21.32) * mm});
            skArc(sketch, "E24.44.10", {"start": v(3.4, -22.5) * mm, "mid": v(3.26, -22.52) * mm, "end": v(3.13, -22.54) * mm});
            skArc(sketch, "E24.44.11", {"start": v(3.4, -22.5) * mm, "mid": v(3.52, -22.48) * mm, "end": v(3.65, -22.46) * mm});
            skPoint(sketch, "E24.45.0", {"position": v(4.8, -22.24) * mm});
            skPoint(sketch, "E24.45.1", {"position": v(5.32, -22.12) * mm});
            skPoint(sketch, "E24.45.2", {"position": v(4.56, -21.75) * mm});
            skPoint(sketch, "E24.45.3", {"position": v(5.32, -21.58) * mm});
            skPoint(sketch, "E24.45.4", {"position": v(4.43, -21.24) * mm});
            skPoint(sketch, "E24.45.5", {"position": v(5.22, -21.06) * mm});
            skArc(sketch, "E24.45.6", {"start": v(4.43, -21.24) * mm, "mid": v(4.23, -21.28) * mm, "end": v(4.03, -21.32) * mm});
            skArc(sketch, "E24.45.7", {"start": v(5.22, -21.06) * mm, "mid": v(5.33, -21.59) * mm, "end": v(5.32, -22.12) * mm});
            skArc(sketch, "E24.45.8", {"start": v(4.43, -21.24) * mm, "mid": v(4.57, -21.76) * mm, "end": v(4.8, -22.24) * mm});
            skArc(sketch, "E24.45.9", {"start": v(5.22, -21.06) * mm, "mid": v(5.42, -21) * mm, "end": v(5.62, -20.96) * mm});
            skArc(sketch, "E24.45.10", {"start": v(5.06, -22.18) * mm, "mid": v(4.93, -22.21) * mm, "end": v(4.8, -22.24) * mm});
            skArc(sketch, "E24.45.11", {"start": v(5.06, -22.18) * mm, "mid": v(5.2, -22.15) * mm, "end": v(5.32, -22.12) * mm});
            skPoint(sketch, "E24.46.0", {"position": v(6.45, -21.82) * mm});
            skPoint(sketch, "E24.46.1", {"position": v(6.96, -21.66) * mm});
            skPoint(sketch, "E24.46.2", {"position": v(6.18, -21.35) * mm});
            skPoint(sketch, "E24.46.3", {"position": v(6.92, -21.12) * mm});
            skPoint(sketch, "E24.46.4", {"position": v(6, -20.85) * mm});
            skPoint(sketch, "E24.46.5", {"position": v(6.78, -20.6) * mm});
            skArc(sketch, "E24.46.6", {"start": v(6, -20.85) * mm, "mid": v(5.81, -20.9) * mm, "end": v(5.62, -20.96) * mm});
            skArc(sketch, "E24.46.7", {"start": v(6.78, -20.6) * mm, "mid": v(6.92, -21.13) * mm, "end": v(6.96, -21.66) * mm});
            skArc(sketch, "E24.46.8", {"start": v(6, -20.85) * mm, "mid": v(6.18, -21.36) * mm, "end": v(6.45, -21.82) * mm});
            skArc(sketch, "E24.46.9", {"start": v(6.78, -20.6) * mm, "mid": v(6.97, -20.54) * mm, "end": v(7.17, -20.48) * mm});
            skArc(sketch, "E24.46.10", {"start": v(6.7, -21.74) * mm, "mid": v(6.58, -21.78) * mm, "end": v(6.45, -21.82) * mm});
            skArc(sketch, "E24.46.11", {"start": v(6.7, -21.74) * mm, "mid": v(6.83, -21.7) * mm, "end": v(6.96, -21.66) * mm});
            skPoint(sketch, "E24.47.0", {"position": v(8.06, -21.28) * mm});
            skPoint(sketch, "E24.47.1", {"position": v(8.56, -21.08) * mm});
            skPoint(sketch, "E24.47.2", {"position": v(7.76, -20.83) * mm});
            skPoint(sketch, "E24.47.3", {"position": v(8.48, -20.54) * mm});
            skPoint(sketch, "E24.47.4", {"position": v(7.55, -20.34) * mm});
            skPoint(sketch, "E24.47.5", {"position": v(8.3, -20.04) * mm});
            skArc(sketch, "E24.47.6", {"start": v(7.55, -20.34) * mm, "mid": v(7.36, -20.41) * mm, "end": v(7.17, -20.48) * mm});
            skArc(sketch, "E24.47.7", {"start": v(8.3, -20.04) * mm, "mid": v(8.48, -20.55) * mm, "end": v(8.56, -21.08) * mm});
            skArc(sketch, "E24.47.8", {"start": v(7.55, -20.34) * mm, "mid": v(7.76, -20.83) * mm, "end": v(8.06, -21.28) * mm});
            skArc(sketch, "E24.47.9", {"start": v(8.3, -20.04) * mm, "mid": v(8.49, -19.97) * mm, "end": v(8.68, -19.89) * mm});
            skArc(sketch, "E24.47.10", {"start": v(8.31, -21.18) * mm, "mid": v(8.19, -21.23) * mm, "end": v(8.06, -21.28) * mm});
            skArc(sketch, "E24.47.11", {"start": v(8.31, -21.18) * mm, "mid": v(8.44, -21.13) * mm, "end": v(8.56, -21.08) * mm});
            skPoint(sketch, "E24.48.0", {"position": v(9.63, -20.61) * mm});
            skPoint(sketch, "E24.48.1", {"position": v(10.11, -20.38) * mm});
            skPoint(sketch, "E24.48.2", {"position": v(9.3, -20.2) * mm});
            skPoint(sketch, "E24.48.3", {"position": v(10, -19.85) * mm});
            skPoint(sketch, "E24.48.4", {"position": v(9.05, -19.72) * mm});
            skPoint(sketch, "E24.48.5", {"position": v(9.78, -19.37) * mm});
            skArc(sketch, "E24.48.6", {"start": v(9.05, -19.72) * mm, "mid": v(8.86, -19.8) * mm, "end": v(8.68, -19.89) * mm});
            skArc(sketch, "E24.48.7", {"start": v(9.78, -19.37) * mm, "mid": v(10, -19.86) * mm, "end": v(10.11, -20.38) * mm});
            skArc(sketch, "E24.48.8", {"start": v(9.05, -19.72) * mm, "mid": v(9.3, -20.2) * mm, "end": v(9.63, -20.61) * mm});
            skArc(sketch, "E24.48.9", {"start": v(9.78, -19.37) * mm, "mid": v(9.96, -19.28) * mm, "end": v(10.14, -19.18) * mm});
            skArc(sketch, "E24.48.10", {"start": v(9.87, -20.5) * mm, "mid": v(9.75, -20.56) * mm, "end": v(9.63, -20.61) * mm});
            skArc(sketch, "E24.48.11", {"start": v(9.87, -20.5) * mm, "mid": v(10, -20.44) * mm, "end": v(10.11, -20.38) * mm});
            skPoint(sketch, "E24.49.0", {"position": v(11.15, -19.84) * mm});
            skPoint(sketch, "E24.49.1", {"position": v(11.6, -19.57) * mm});
            skPoint(sketch, "E24.49.2", {"position": v(10.77, -19.44) * mm});
            skPoint(sketch, "E24.49.3", {"position": v(11.45, -19.05) * mm});
            skPoint(sketch, "E24.49.4", {"position": v(10.5, -18.99) * mm});
            skPoint(sketch, "E24.49.5", {"position": v(11.2, -18.58) * mm});
            skArc(sketch, "E24.49.6", {"start": v(10.5, -18.99) * mm, "mid": v(10.32, -19.09) * mm, "end": v(10.14, -19.18) * mm});
            skArc(sketch, "E24.49.7", {"start": v(11.2, -18.58) * mm, "mid": v(11.45, -19.06) * mm, "end": v(11.6, -19.57) * mm});
            skArc(sketch, "E24.49.8", {"start": v(10.5, -18.99) * mm, "mid": v(10.78, -19.45) * mm, "end": v(11.15, -19.84) * mm});
            skArc(sketch, "E24.49.9", {"start": v(11.2, -18.58) * mm, "mid": v(11.37, -18.48) * mm, "end": v(11.54, -18.37) * mm});
            skArc(sketch, "E24.49.10", {"start": v(11.38, -19.7) * mm, "mid": v(11.26, -19.77) * mm, "end": v(11.15, -19.84) * mm});
            skArc(sketch, "E24.49.11", {"start": v(11.38, -19.7) * mm, "mid": v(11.5, -19.64) * mm, "end": v(11.6, -19.57) * mm});
            skPoint(sketch, "E24.50.0", {"position": v(12.6, -18.95) * mm});
            skPoint(sketch, "E24.50.1", {"position": v(13.04, -18.65) * mm});
            skPoint(sketch, "E24.50.2", {"position": v(12.2, -18.58) * mm});
            skPoint(sketch, "E24.50.3", {"position": v(12.84, -18.14) * mm});
            skPoint(sketch, "E24.50.4", {"position": v(11.88, -18.15) * mm});
            skPoint(sketch, "E24.50.5", {"position": v(12.55, -17.7) * mm});
            skArc(sketch, "E24.50.6", {"start": v(11.88, -18.15) * mm, "mid": v(11.71, -18.26) * mm, "end": v(11.54, -18.37) * mm});
            skArc(sketch, "E24.50.7", {"start": v(12.55, -17.7) * mm, "mid": v(12.84, -18.15) * mm, "end": v(13.04, -18.65) * mm});
            skArc(sketch, "E24.50.8", {"start": v(11.88, -18.15) * mm, "mid": v(12.2, -18.59) * mm, "end": v(12.6, -18.95) * mm});
            skArc(sketch, "E24.50.9", {"start": v(12.55, -17.7) * mm, "mid": v(12.72, -17.58) * mm, "end": v(12.88, -17.46) * mm});
            skArc(sketch, "E24.50.10", {"start": v(12.82, -18.8) * mm, "mid": v(12.7, -18.87) * mm, "end": v(12.6, -18.95) * mm});
            skArc(sketch, "E24.50.11", {"start": v(12.82, -18.8) * mm, "mid": v(12.93, -18.73) * mm, "end": v(13.04, -18.65) * mm});
            skPoint(sketch, "E24.51.0", {"position": v(13.98, -17.95) * mm});
            skPoint(sketch, "E24.51.1", {"position": v(14.4, -17.62) * mm});
            skPoint(sketch, "E24.51.2", {"position": v(13.55, -17.62) * mm});
            skPoint(sketch, "E24.51.3", {"position": v(14.16, -17.13) * mm});
            skPoint(sketch, "E24.51.4", {"position": v(13.2, -17.21) * mm});
            skPoint(sketch, "E24.51.5", {"position": v(13.84, -16.7) * mm});
            skArc(sketch, "E24.51.6", {"start": v(13.2, -17.21) * mm, "mid": v(13.05, -17.34) * mm, "end": v(12.88, -17.46) * mm});
            skArc(sketch, "E24.51.7", {"start": v(13.84, -16.7) * mm, "mid": v(14.16, -17.14) * mm, "end": v(14.4, -17.62) * mm});
            skArc(sketch, "E24.51.8", {"start": v(13.2, -17.21) * mm, "mid": v(13.56, -17.62) * mm, "end": v(13.98, -17.95) * mm});
            skArc(sketch, "E24.51.9", {"start": v(13.84, -16.7) * mm, "mid": v(14, -16.58) * mm, "end": v(14.15, -16.44) * mm});
            skArc(sketch, "E24.51.10", {"start": v(14.19, -17.79) * mm, "mid": v(14.08, -17.87) * mm, "end": v(13.98, -17.95) * mm});
            skArc(sketch, "E24.51.11", {"start": v(14.19, -17.79) * mm, "mid": v(14.3, -17.7) * mm, "end": v(14.4, -17.62) * mm});
            skPoint(sketch, "E24.52.0", {"position": v(15.28, -16.86) * mm});
            skPoint(sketch, "E24.52.1", {"position": v(15.67, -16.5) * mm});
            skPoint(sketch, "E24.52.2", {"position": v(14.83, -16.55) * mm});
            skPoint(sketch, "E24.52.3", {"position": v(15.4, -16.02) * mm});
            skPoint(sketch, "E24.52.4", {"position": v(14.46, -16.18) * mm});
            skPoint(sketch, "E24.52.5", {"position": v(15.05, -15.63) * mm});
            skArc(sketch, "E24.52.6", {"start": v(14.46, -16.18) * mm, "mid": v(14.3, -16.31) * mm, "end": v(14.15, -16.44) * mm});
            skArc(sketch, "E24.52.7", {"start": v(15.05, -15.63) * mm, "mid": v(15.4, -16.03) * mm, "end": v(15.67, -16.5) * mm});
            skArc(sketch, "E24.52.8", {"start": v(14.46, -16.18) * mm, "mid": v(14.83, -16.56) * mm, "end": v(15.28, -16.86) * mm});
            skArc(sketch, "E24.52.9", {"start": v(15.05, -15.63) * mm, "mid": v(15.2, -15.48) * mm, "end": v(15.34, -15.34) * mm});
            skArc(sketch, "E24.52.10", {"start": v(15.48, -16.68) * mm, "mid": v(15.38, -16.77) * mm, "end": v(15.28, -16.86) * mm});
            skArc(sketch, "E24.52.11", {"start": v(15.48, -16.68) * mm, "mid": v(15.57, -16.59) * mm, "end": v(15.67, -16.5) * mm});
            skPoint(sketch, "E24.53.0", {"position": v(16.5, -15.67) * mm});
            skPoint(sketch, "E24.53.1", {"position": v(16.86, -15.28) * mm});
            skPoint(sketch, "E24.53.2", {"position": v(16.02, -15.4) * mm});
            skPoint(sketch, "E24.53.3", {"position": v(16.55, -14.83) * mm});
            skPoint(sketch, "E24.53.4", {"position": v(15.63, -15.05) * mm});
            skPoint(sketch, "E24.53.5", {"position": v(16.18, -14.46) * mm});
            skArc(sketch, "E24.53.6", {"start": v(15.63, -15.05) * mm, "mid": v(15.48, -15.2) * mm, "end": v(15.34, -15.34) * mm});
            skArc(sketch, "E24.53.7", {"start": v(16.18, -14.46) * mm, "mid": v(16.56, -14.83) * mm, "end": v(16.86, -15.28) * mm});
            skArc(sketch, "E24.53.8", {"start": v(15.63, -15.05) * mm, "mid": v(16.03, -15.4) * mm, "end": v(16.5, -15.67) * mm});
            skArc(sketch, "E24.53.9", {"start": v(16.18, -14.46) * mm, "mid": v(16.31, -14.3) * mm, "end": v(16.44, -14.15) * mm});
            skArc(sketch, "E24.53.10", {"start": v(16.68, -15.48) * mm, "mid": v(16.59, -15.57) * mm, "end": v(16.5, -15.67) * mm});
            skArc(sketch, "E24.53.11", {"start": v(16.68, -15.48) * mm, "mid": v(16.77, -15.38) * mm, "end": v(16.86, -15.28) * mm});
            skPoint(sketch, "E24.54.0", {"position": v(17.62, -14.4) * mm});
            skPoint(sketch, "E24.54.1", {"position": v(17.95, -13.98) * mm});
            skPoint(sketch, "E24.54.2", {"position": v(17.13, -14.16) * mm});
            skPoint(sketch, "E24.54.3", {"position": v(17.62, -13.55) * mm});
            skPoint(sketch, "E24.54.4", {"position": v(16.7, -13.84) * mm});
            skPoint(sketch, "E24.54.5", {"position": v(17.21, -13.2) * mm});
            skArc(sketch, "E24.54.6", {"start": v(16.7, -13.84) * mm, "mid": v(16.58, -14) * mm, "end": v(16.44, -14.15) * mm});
            skArc(sketch, "E24.54.7", {"start": v(17.21, -13.2) * mm, "mid": v(17.62, -13.56) * mm, "end": v(17.95, -13.98) * mm});
            skArc(sketch, "E24.54.8", {"start": v(16.7, -13.84) * mm, "mid": v(17.14, -14.16) * mm, "end": v(17.62, -14.4) * mm});
            skArc(sketch, "E24.54.9", {"start": v(17.21, -13.2) * mm, "mid": v(17.34, -13.05) * mm, "end": v(17.46, -12.88) * mm});
            skArc(sketch, "E24.54.10", {"start": v(17.79, -14.19) * mm, "mid": v(17.7, -14.3) * mm, "end": v(17.62, -14.4) * mm});
            skArc(sketch, "E24.54.11", {"start": v(17.79, -14.19) * mm, "mid": v(17.87, -14.08) * mm, "end": v(17.95, -13.98) * mm});
            skPoint(sketch, "E24.55.0", {"position": v(18.65, -13.04) * mm});
            skPoint(sketch, "E24.55.1", {"position": v(18.95, -12.6) * mm});
            skPoint(sketch, "E24.55.2", {"position": v(18.14, -12.84) * mm});
            skPoint(sketch, "E24.55.3", {"position": v(18.58, -12.2) * mm});
            skPoint(sketch, "E24.55.4", {"position": v(17.7, -12.55) * mm});
            skPoint(sketch, "E24.55.5", {"position": v(18.15, -11.88) * mm});
            skArc(sketch, "E24.55.6", {"start": v(17.7, -12.55) * mm, "mid": v(17.58, -12.72) * mm, "end": v(17.46, -12.88) * mm});
            skArc(sketch, "E24.55.7", {"start": v(18.15, -11.88) * mm, "mid": v(18.59, -12.2) * mm, "end": v(18.95, -12.6) * mm});
            skArc(sketch, "E24.55.8", {"start": v(17.7, -12.55) * mm, "mid": v(18.15, -12.84) * mm, "end": v(18.65, -13.04) * mm});
            skArc(sketch, "E24.55.9", {"start": v(18.15, -11.88) * mm, "mid": v(18.26, -11.71) * mm, "end": v(18.37, -11.54) * mm});
            skArc(sketch, "E24.55.10", {"start": v(18.8, -12.82) * mm, "mid": v(18.73, -12.93) * mm, "end": v(18.65, -13.04) * mm});
            skArc(sketch, "E24.55.11", {"start": v(18.8, -12.82) * mm, "mid": v(18.87, -12.7) * mm, "end": v(18.95, -12.6) * mm});
            skPoint(sketch, "E24.56.0", {"position": v(19.57, -11.6) * mm});
            skPoint(sketch, "E24.56.1", {"position": v(19.84, -11.15) * mm});
            skPoint(sketch, "E24.56.2", {"position": v(19.05, -11.45) * mm});
            skPoint(sketch, "E24.56.3", {"position": v(19.44, -10.77) * mm});
            skPoint(sketch, "E24.56.4", {"position": v(18.58, -11.2) * mm});
            skPoint(sketch, "E24.56.5", {"position": v(18.99, -10.5) * mm});
            skArc(sketch, "E24.56.6", {"start": v(18.58, -11.2) * mm, "mid": v(18.48, -11.37) * mm, "end": v(18.37, -11.54) * mm});
            skArc(sketch, "E24.56.7", {"start": v(18.99, -10.5) * mm, "mid": v(19.45, -10.78) * mm, "end": v(19.84, -11.15) * mm});
            skArc(sketch, "E24.56.8", {"start": v(18.58, -11.2) * mm, "mid": v(19.06, -11.45) * mm, "end": v(19.57, -11.6) * mm});
            skArc(sketch, "E24.56.9", {"start": v(18.99, -10.5) * mm, "mid": v(19.09, -10.32) * mm, "end": v(19.18, -10.14) * mm});
            skArc(sketch, "E24.56.10", {"start": v(19.7, -11.38) * mm, "mid": v(19.64, -11.5) * mm, "end": v(19.57, -11.6) * mm});
            skArc(sketch, "E24.56.11", {"start": v(19.7, -11.38) * mm, "mid": v(19.77, -11.26) * mm, "end": v(19.84, -11.15) * mm});
            skPoint(sketch, "E24.57.0", {"position": v(20.38, -10.11) * mm});
            skPoint(sketch, "E24.57.1", {"position": v(20.61, -9.63) * mm});
            skPoint(sketch, "E24.57.2", {"position": v(19.85, -10) * mm});
            skPoint(sketch, "E24.57.3", {"position": v(20.2, -9.3) * mm});
            skPoint(sketch, "E24.57.4", {"position": v(19.37, -9.78) * mm});
            skPoint(sketch, "E24.57.5", {"position": v(19.72, -9.05) * mm});
            skArc(sketch, "E24.57.6", {"start": v(19.37, -9.78) * mm, "mid": v(19.28, -9.96) * mm, "end": v(19.18, -10.14) * mm});
            skArc(sketch, "E24.57.7", {"start": v(19.72, -9.05) * mm, "mid": v(20.2, -9.3) * mm, "end": v(20.61, -9.63) * mm});
            skArc(sketch, "E24.57.8", {"start": v(19.37, -9.78) * mm, "mid": v(19.86, -10) * mm, "end": v(20.38, -10.11) * mm});
            skArc(sketch, "E24.57.9", {"start": v(19.72, -9.05) * mm, "mid": v(19.8, -8.86) * mm, "end": v(19.89, -8.68) * mm});
            skArc(sketch, "E24.57.10", {"start": v(20.5, -9.87) * mm, "mid": v(20.44, -10) * mm, "end": v(20.38, -10.11) * mm});
            skArc(sketch, "E24.57.11", {"start": v(20.5, -9.87) * mm, "mid": v(20.56, -9.75) * mm, "end": v(20.61, -9.63) * mm});
            skPoint(sketch, "E24.58.0", {"position": v(21.08, -8.56) * mm});
            skPoint(sketch, "E24.58.1", {"position": v(21.28, -8.06) * mm});
            skPoint(sketch, "E24.58.2", {"position": v(20.54, -8.48) * mm});
            skPoint(sketch, "E24.58.3", {"position": v(20.83, -7.76) * mm});
            skPoint(sketch, "E24.58.4", {"position": v(20.04, -8.3) * mm});
            skPoint(sketch, "E24.58.5", {"position": v(20.34, -7.55) * mm});
            skArc(sketch, "E24.58.6", {"start": v(20.04, -8.3) * mm, "mid": v(19.97, -8.49) * mm, "end": v(19.89, -8.68) * mm});
            skArc(sketch, "E24.58.7", {"start": v(20.34, -7.55) * mm, "mid": v(20.83, -7.76) * mm, "end": v(21.28, -8.06) * mm});
            skArc(sketch, "E24.58.8", {"start": v(20.04, -8.3) * mm, "mid": v(20.55, -8.48) * mm, "end": v(21.08, -8.56) * mm});
            skArc(sketch, "E24.58.9", {"start": v(20.34, -7.55) * mm, "mid": v(20.41, -7.36) * mm, "end": v(20.48, -7.17) * mm});
            skArc(sketch, "E24.58.10", {"start": v(21.18, -8.31) * mm, "mid": v(21.13, -8.44) * mm, "end": v(21.08, -8.56) * mm});
            skArc(sketch, "E24.58.11", {"start": v(21.18, -8.31) * mm, "mid": v(21.23, -8.19) * mm, "end": v(21.28, -8.06) * mm});
            skPoint(sketch, "E24.59.0", {"position": v(21.66, -6.96) * mm});
            skPoint(sketch, "E24.59.1", {"position": v(21.82, -6.45) * mm});
            skPoint(sketch, "E24.59.2", {"position": v(21.12, -6.92) * mm});
            skPoint(sketch, "E24.59.3", {"position": v(21.35, -6.18) * mm});
            skPoint(sketch, "E24.59.4", {"position": v(20.6, -6.78) * mm});
            skPoint(sketch, "E24.59.5", {"position": v(20.85, -6) * mm});
            skArc(sketch, "E24.59.6", {"start": v(20.6, -6.78) * mm, "mid": v(20.54, -6.97) * mm, "end": v(20.48, -7.17) * mm});
            skArc(sketch, "E24.59.7", {"start": v(20.85, -6) * mm, "mid": v(21.36, -6.18) * mm, "end": v(21.82, -6.45) * mm});
            skArc(sketch, "E24.59.8", {"start": v(20.6, -6.78) * mm, "mid": v(21.13, -6.92) * mm, "end": v(21.66, -6.96) * mm});
            skArc(sketch, "E24.59.9", {"start": v(20.85, -6) * mm, "mid": v(20.9, -5.81) * mm, "end": v(20.96, -5.62) * mm});
            skArc(sketch, "E24.59.10", {"start": v(21.74, -6.7) * mm, "mid": v(21.7, -6.83) * mm, "end": v(21.66, -6.96) * mm});
            skArc(sketch, "E24.59.11", {"start": v(21.74, -6.7) * mm, "mid": v(21.78, -6.58) * mm, "end": v(21.82, -6.45) * mm});
            skPoint(sketch, "E24.60.0", {"position": v(22.12, -5.32) * mm});
            skPoint(sketch, "E24.60.1", {"position": v(22.24, -4.8) * mm});
            skPoint(sketch, "E24.60.2", {"position": v(21.58, -5.32) * mm});
            skPoint(sketch, "E24.60.3", {"position": v(21.75, -4.56) * mm});
            skPoint(sketch, "E24.60.4", {"position": v(21.06, -5.22) * mm});
            skPoint(sketch, "E24.60.5", {"position": v(21.24, -4.43) * mm});
            skArc(sketch, "E24.60.6", {"start": v(21.06, -5.22) * mm, "mid": v(21, -5.42) * mm, "end": v(20.96, -5.62) * mm});
            skArc(sketch, "E24.60.7", {"start": v(21.24, -4.43) * mm, "mid": v(21.76, -4.57) * mm, "end": v(22.24, -4.8) * mm});
            skArc(sketch, "E24.60.8", {"start": v(21.06, -5.22) * mm, "mid": v(21.59, -5.33) * mm, "end": v(22.12, -5.32) * mm});
            skArc(sketch, "E24.60.9", {"start": v(21.24, -4.43) * mm, "mid": v(21.28, -4.23) * mm, "end": v(21.32, -4.03) * mm});
            skArc(sketch, "E24.60.10", {"start": v(22.18, -5.06) * mm, "mid": v(22.15, -5.2) * mm, "end": v(22.12, -5.32) * mm});
            skArc(sketch, "E24.60.11", {"start": v(22.18, -5.06) * mm, "mid": v(22.21, -4.93) * mm, "end": v(22.24, -4.8) * mm});
            skPoint(sketch, "E24.61.0", {"position": v(22.46, -3.65) * mm});
            skPoint(sketch, "E24.61.1", {"position": v(22.54, -3.13) * mm});
            skPoint(sketch, "E24.61.2", {"position": v(21.92, -3.7) * mm});
            skPoint(sketch, "E24.61.3", {"position": v(22.03, -2.93) * mm});
            skPoint(sketch, "E24.61.4", {"position": v(21.39, -3.63) * mm});
            skPoint(sketch, "E24.61.5", {"position": v(21.51, -2.83) * mm});
            skArc(sketch, "E24.61.6", {"start": v(21.39, -3.63) * mm, "mid": v(21.35, -3.83) * mm, "end": v(21.32, -4.03) * mm});
            skArc(sketch, "E24.61.7", {"start": v(21.51, -2.83) * mm, "mid": v(22.04, -2.93) * mm, "end": v(22.54, -3.13) * mm});
            skArc(sketch, "E24.61.8", {"start": v(21.39, -3.63) * mm, "mid": v(21.92, -3.7) * mm, "end": v(22.46, -3.65) * mm});
            skArc(sketch, "E24.61.9", {"start": v(21.51, -2.83) * mm, "mid": v(21.54, -2.63) * mm, "end": v(21.56, -2.43) * mm});
            skArc(sketch, "E24.61.10", {"start": v(22.5, -3.4) * mm, "mid": v(22.48, -3.52) * mm, "end": v(22.46, -3.65) * mm});
            skArc(sketch, "E24.61.11", {"start": v(22.5, -3.4) * mm, "mid": v(22.52, -3.26) * mm, "end": v(22.54, -3.13) * mm});
            skPoint(sketch, "E24.62.0", {"position": v(22.67, -1.97) * mm});
            skPoint(sketch, "E24.62.1", {"position": v(22.7, -1.44) * mm});
            skPoint(sketch, "E24.62.2", {"position": v(22.13, -2.05) * mm});
            skPoint(sketch, "E24.62.3", {"position": v(22.19, -1.27) * mm});
            skPoint(sketch, "E24.62.4", {"position": v(21.6, -2.03) * mm});
            skPoint(sketch, "E24.62.5", {"position": v(21.66, -1.22) * mm});
            skArc(sketch, "E24.62.6", {"start": v(21.6, -2.03) * mm, "mid": v(21.58, -2.23) * mm, "end": v(21.56, -2.43) * mm});
            skArc(sketch, "E24.62.7", {"start": v(21.66, -1.22) * mm, "mid": v(22.2, -1.27) * mm, "end": v(22.7, -1.44) * mm});
            skArc(sketch, "E24.62.8", {"start": v(21.6, -2.03) * mm, "mid": v(22.14, -2.05) * mm, "end": v(22.67, -1.97) * mm});
            skArc(sketch, "E24.62.9", {"start": v(21.66, -1.22) * mm, "mid": v(21.67, -1.01) * mm, "end": v(21.68, -0.81) * mm});
            skArc(sketch, "E24.62.10", {"start": v(22.7, -1.7) * mm, "mid": v(22.68, -1.83) * mm, "end": v(22.67, -1.97) * mm});
            skArc(sketch, "E24.62.11", {"start": v(22.7, -1.7) * mm, "mid": v(22.7, -1.57) * mm, "end": v(22.7, -1.44) * mm});
            skPoint(sketch, "E24.63.0", {"position": v(22.75, -0.27) * mm});
            skPoint(sketch, "E24.63.1", {"position": v(22.75, 0.27) * mm});
            skPoint(sketch, "E24.63.2", {"position": v(22.22, -0.39) * mm});
            skPoint(sketch, "E24.63.3", {"position": v(22.22, 0.39) * mm});
            skPoint(sketch, "E24.63.4", {"position": v(21.7, -0.4) * mm});
            skPoint(sketch, "E24.63.5", {"position": v(21.7, 0.4) * mm});
            skArc(sketch, "E24.63.6", {"start": v(21.7, -0.4) * mm, "mid": v(21.69, -0.6) * mm, "end": v(21.68, -0.81) * mm});
            skArc(sketch, "E24.63.7", {"start": v(21.7, 0.4) * mm, "mid": v(22.23, 0.39) * mm, "end": v(22.75, 0.27) * mm});
            skArc(sketch, "E24.63.8", {"start": v(21.7, -0.4) * mm, "mid": v(22.23, -0.39) * mm, "end": v(22.75, -0.27) * mm});
            skArc(sketch, "E24.63.9", {"start": v(21.7, 0.4) * mm, "mid": v(21.69, 0.6) * mm, "end": v(21.68, 0.81) * mm});
            skArc(sketch, "E24.63.10", {"start": v(22.75, 0) * mm, "mid": v(22.75, -0.13) * mm, "end": v(22.75, -0.27) * mm});
            skArc(sketch, "E24.63.11", {"start": v(22.75, 0) * mm, "mid": v(22.75, 0.13) * mm, "end": v(22.75, 0.27) * mm});
            skPoint(sketch, "E24.64.0", {"position": v(22.7, 1.44) * mm});
            skPoint(sketch, "E24.64.1", {"position": v(22.67, 1.97) * mm});
            skPoint(sketch, "E24.64.2", {"position": v(22.19, 1.27) * mm});
            skPoint(sketch, "E24.64.3", {"position": v(22.13, 2.05) * mm});
            skPoint(sketch, "E24.64.4", {"position": v(21.66, 1.22) * mm});
            skPoint(sketch, "E24.64.5", {"position": v(21.6, 2.03) * mm});
            skArc(sketch, "E24.64.6", {"start": v(21.66, 1.22) * mm, "mid": v(21.67, 1.01) * mm, "end": v(21.68, 0.81) * mm});
            skArc(sketch, "E24.64.7", {"start": v(21.6, 2.03) * mm, "mid": v(22.14, 2.05) * mm, "end": v(22.67, 1.97) * mm});
            skArc(sketch, "E24.64.8", {"start": v(21.66, 1.22) * mm, "mid": v(22.2, 1.27) * mm, "end": v(22.7, 1.44) * mm});
            skArc(sketch, "E24.64.9", {"start": v(21.6, 2.03) * mm, "mid": v(21.58, 2.23) * mm, "end": v(21.56, 2.43) * mm});
            skArc(sketch, "E24.64.10", {"start": v(22.7, 1.7) * mm, "mid": v(22.7, 1.57) * mm, "end": v(22.7, 1.44) * mm});
            skArc(sketch, "E24.64.11", {"start": v(22.7, 1.7) * mm, "mid": v(22.68, 1.83) * mm, "end": v(22.67, 1.97) * mm});
            skPoint(sketch, "E24.65.0", {"position": v(22.54, 3.13) * mm});
            skPoint(sketch, "E24.65.1", {"position": v(22.46, 3.65) * mm});
            skPoint(sketch, "E24.65.2", {"position": v(22.03, 2.93) * mm});
            skPoint(sketch, "E24.65.3", {"position": v(21.92, 3.7) * mm});
            skPoint(sketch, "E24.65.4", {"position": v(21.51, 2.83) * mm});
            skPoint(sketch, "E24.65.5", {"position": v(21.39, 3.63) * mm});
            skArc(sketch, "E24.65.6", {"start": v(21.51, 2.83) * mm, "mid": v(21.54, 2.63) * mm, "end": v(21.56, 2.43) * mm});
            skArc(sketch, "E24.65.7", {"start": v(21.39, 3.63) * mm, "mid": v(21.92, 3.7) * mm, "end": v(22.46, 3.65) * mm});
            skArc(sketch, "E24.65.8", {"start": v(21.51, 2.83) * mm, "mid": v(22.04, 2.93) * mm, "end": v(22.54, 3.13) * mm});
            skArc(sketch, "E24.65.9", {"start": v(21.39, 3.63) * mm, "mid": v(21.35, 3.83) * mm, "end": v(21.32, 4.03) * mm});
            skArc(sketch, "E24.65.10", {"start": v(22.5, 3.4) * mm, "mid": v(22.52, 3.26) * mm, "end": v(22.54, 3.13) * mm});
            skArc(sketch, "E24.65.11", {"start": v(22.5, 3.4) * mm, "mid": v(22.48, 3.52) * mm, "end": v(22.46, 3.65) * mm});
            skPoint(sketch, "E24.66.0", {"position": v(22.24, 4.8) * mm});
            skPoint(sketch, "E24.66.1", {"position": v(22.12, 5.32) * mm});
            skPoint(sketch, "E24.66.2", {"position": v(21.75, 4.56) * mm});
            skPoint(sketch, "E24.66.3", {"position": v(21.58, 5.32) * mm});
            skPoint(sketch, "E24.66.4", {"position": v(21.24, 4.43) * mm});
            skPoint(sketch, "E24.66.5", {"position": v(21.06, 5.22) * mm});
            skArc(sketch, "E24.66.6", {"start": v(21.24, 4.43) * mm, "mid": v(21.28, 4.23) * mm, "end": v(21.32, 4.03) * mm});
            skArc(sketch, "E24.66.7", {"start": v(21.06, 5.22) * mm, "mid": v(21.59, 5.33) * mm, "end": v(22.12, 5.32) * mm});
            skArc(sketch, "E24.66.8", {"start": v(21.24, 4.43) * mm, "mid": v(21.76, 4.57) * mm, "end": v(22.24, 4.8) * mm});
            skArc(sketch, "E24.66.9", {"start": v(21.06, 5.22) * mm, "mid": v(21, 5.42) * mm, "end": v(20.96, 5.62) * mm});
            skArc(sketch, "E24.66.10", {"start": v(22.18, 5.06) * mm, "mid": v(22.21, 4.93) * mm, "end": v(22.24, 4.8) * mm});
            skArc(sketch, "E24.66.11", {"start": v(22.18, 5.06) * mm, "mid": v(22.15, 5.2) * mm, "end": v(22.12, 5.32) * mm});
            skPoint(sketch, "E24.67.0", {"position": v(21.82, 6.45) * mm});
            skPoint(sketch, "E24.67.1", {"position": v(21.66, 6.96) * mm});
            skPoint(sketch, "E24.67.2", {"position": v(21.35, 6.18) * mm});
            skPoint(sketch, "E24.67.3", {"position": v(21.12, 6.92) * mm});
            skPoint(sketch, "E24.67.4", {"position": v(20.85, 6) * mm});
            skPoint(sketch, "E24.67.5", {"position": v(20.6, 6.78) * mm});
            skArc(sketch, "E24.67.6", {"start": v(20.85, 6) * mm, "mid": v(20.9, 5.81) * mm, "end": v(20.96, 5.62) * mm});
            skArc(sketch, "E24.67.7", {"start": v(20.6, 6.78) * mm, "mid": v(21.13, 6.92) * mm, "end": v(21.66, 6.96) * mm});
            skArc(sketch, "E24.67.8", {"start": v(20.85, 6) * mm, "mid": v(21.36, 6.18) * mm, "end": v(21.82, 6.45) * mm});
            skArc(sketch, "E24.67.9", {"start": v(20.6, 6.78) * mm, "mid": v(20.54, 6.97) * mm, "end": v(20.48, 7.17) * mm});
            skArc(sketch, "E24.67.10", {"start": v(21.74, 6.7) * mm, "mid": v(21.78, 6.58) * mm, "end": v(21.82, 6.45) * mm});
            skArc(sketch, "E24.67.11", {"start": v(21.74, 6.7) * mm, "mid": v(21.7, 6.83) * mm, "end": v(21.66, 6.96) * mm});
            skPoint(sketch, "E24.68.0", {"position": v(21.28, 8.06) * mm});
            skPoint(sketch, "E24.68.1", {"position": v(21.08, 8.56) * mm});
            skPoint(sketch, "E24.68.2", {"position": v(20.83, 7.76) * mm});
            skPoint(sketch, "E24.68.3", {"position": v(20.54, 8.48) * mm});
            skPoint(sketch, "E24.68.4", {"position": v(20.34, 7.55) * mm});
            skPoint(sketch, "E24.68.5", {"position": v(20.04, 8.3) * mm});
            skArc(sketch, "E24.68.6", {"start": v(20.34, 7.55) * mm, "mid": v(20.41, 7.36) * mm, "end": v(20.48, 7.17) * mm});
            skArc(sketch, "E24.68.7", {"start": v(20.04, 8.3) * mm, "mid": v(20.55, 8.48) * mm, "end": v(21.08, 8.56) * mm});
            skArc(sketch, "E24.68.8", {"start": v(20.34, 7.55) * mm, "mid": v(20.83, 7.76) * mm, "end": v(21.28, 8.06) * mm});
            skArc(sketch, "E24.68.9", {"start": v(20.04, 8.3) * mm, "mid": v(19.97, 8.49) * mm, "end": v(19.89, 8.68) * mm});
            skArc(sketch, "E24.68.10", {"start": v(21.18, 8.31) * mm, "mid": v(21.23, 8.19) * mm, "end": v(21.28, 8.06) * mm});
            skArc(sketch, "E24.68.11", {"start": v(21.18, 8.31) * mm, "mid": v(21.13, 8.44) * mm, "end": v(21.08, 8.56) * mm});
            skPoint(sketch, "E24.69.0", {"position": v(20.61, 9.63) * mm});
            skPoint(sketch, "E24.69.1", {"position": v(20.38, 10.11) * mm});
            skPoint(sketch, "E24.69.2", {"position": v(20.2, 9.3) * mm});
            skPoint(sketch, "E24.69.3", {"position": v(19.85, 10) * mm});
            skPoint(sketch, "E24.69.4", {"position": v(19.72, 9.05) * mm});
            skPoint(sketch, "E24.69.5", {"position": v(19.37, 9.78) * mm});
            skArc(sketch, "E24.69.6", {"start": v(19.72, 9.05) * mm, "mid": v(19.8, 8.86) * mm, "end": v(19.89, 8.68) * mm});
            skArc(sketch, "E24.69.7", {"start": v(19.37, 9.78) * mm, "mid": v(19.86, 10) * mm, "end": v(20.38, 10.11) * mm});
            skArc(sketch, "E24.69.8", {"start": v(19.72, 9.05) * mm, "mid": v(20.2, 9.3) * mm, "end": v(20.61, 9.63) * mm});
            skArc(sketch, "E24.69.9", {"start": v(19.37, 9.78) * mm, "mid": v(19.28, 9.96) * mm, "end": v(19.18, 10.14) * mm});
            skArc(sketch, "E24.69.10", {"start": v(20.5, 9.87) * mm, "mid": v(20.56, 9.75) * mm, "end": v(20.61, 9.63) * mm});
            skArc(sketch, "E24.69.11", {"start": v(20.5, 9.87) * mm, "mid": v(20.44, 10) * mm, "end": v(20.38, 10.11) * mm});
            skPoint(sketch, "E24.70.0", {"position": v(19.84, 11.15) * mm});
            skPoint(sketch, "E24.70.1", {"position": v(19.57, 11.6) * mm});
            skPoint(sketch, "E24.70.2", {"position": v(19.44, 10.77) * mm});
            skPoint(sketch, "E24.70.3", {"position": v(19.05, 11.45) * mm});
            skPoint(sketch, "E24.70.4", {"position": v(18.99, 10.5) * mm});
            skPoint(sketch, "E24.70.5", {"position": v(18.58, 11.2) * mm});
            skArc(sketch, "E24.70.6", {"start": v(18.99, 10.5) * mm, "mid": v(19.09, 10.32) * mm, "end": v(19.18, 10.14) * mm});
            skArc(sketch, "E24.70.7", {"start": v(18.58, 11.2) * mm, "mid": v(19.06, 11.45) * mm, "end": v(19.57, 11.6) * mm});
            skArc(sketch, "E24.70.8", {"start": v(18.99, 10.5) * mm, "mid": v(19.45, 10.78) * mm, "end": v(19.84, 11.15) * mm});
            skArc(sketch, "E24.70.9", {"start": v(18.58, 11.2) * mm, "mid": v(18.48, 11.37) * mm, "end": v(18.37, 11.54) * mm});
            skArc(sketch, "E24.70.10", {"start": v(19.7, 11.38) * mm, "mid": v(19.77, 11.26) * mm, "end": v(19.84, 11.15) * mm});
            skArc(sketch, "E24.70.11", {"start": v(19.7, 11.38) * mm, "mid": v(19.64, 11.5) * mm, "end": v(19.57, 11.6) * mm});
            skPoint(sketch, "E24.71.0", {"position": v(18.95, 12.6) * mm});
            skPoint(sketch, "E24.71.1", {"position": v(18.65, 13.04) * mm});
            skPoint(sketch, "E24.71.2", {"position": v(18.58, 12.2) * mm});
            skPoint(sketch, "E24.71.3", {"position": v(18.14, 12.84) * mm});
            skPoint(sketch, "E24.71.4", {"position": v(18.15, 11.88) * mm});
            skPoint(sketch, "E24.71.5", {"position": v(17.7, 12.55) * mm});
            skArc(sketch, "E24.71.6", {"start": v(18.15, 11.88) * mm, "mid": v(18.26, 11.71) * mm, "end": v(18.37, 11.54) * mm});
            skArc(sketch, "E24.71.7", {"start": v(17.7, 12.55) * mm, "mid": v(18.15, 12.84) * mm, "end": v(18.65, 13.04) * mm});
            skArc(sketch, "E24.71.8", {"start": v(18.15, 11.88) * mm, "mid": v(18.59, 12.2) * mm, "end": v(18.95, 12.6) * mm});
            skArc(sketch, "E24.71.9", {"start": v(17.7, 12.55) * mm, "mid": v(17.58, 12.72) * mm, "end": v(17.46, 12.88) * mm});
            skArc(sketch, "E24.71.10", {"start": v(18.8, 12.82) * mm, "mid": v(18.87, 12.7) * mm, "end": v(18.95, 12.6) * mm});
            skArc(sketch, "E24.71.11", {"start": v(18.8, 12.82) * mm, "mid": v(18.73, 12.93) * mm, "end": v(18.65, 13.04) * mm});
            skPoint(sketch, "E24.72.0", {"position": v(17.95, 13.98) * mm});
            skPoint(sketch, "E24.72.1", {"position": v(17.62, 14.4) * mm});
            skPoint(sketch, "E24.72.2", {"position": v(17.62, 13.55) * mm});
            skPoint(sketch, "E24.72.3", {"position": v(17.13, 14.16) * mm});
            skPoint(sketch, "E24.72.4", {"position": v(17.21, 13.2) * mm});
            skPoint(sketch, "E24.72.5", {"position": v(16.7, 13.84) * mm});
            skArc(sketch, "E24.72.6", {"start": v(17.21, 13.2) * mm, "mid": v(17.34, 13.05) * mm, "end": v(17.46, 12.88) * mm});
            skArc(sketch, "E24.72.7", {"start": v(16.7, 13.84) * mm, "mid": v(17.14, 14.16) * mm, "end": v(17.62, 14.4) * mm});
            skArc(sketch, "E24.72.8", {"start": v(17.21, 13.2) * mm, "mid": v(17.62, 13.56) * mm, "end": v(17.95, 13.98) * mm});
            skArc(sketch, "E24.72.9", {"start": v(16.7, 13.84) * mm, "mid": v(16.58, 14) * mm, "end": v(16.44, 14.15) * mm});
            skArc(sketch, "E24.72.10", {"start": v(17.79, 14.19) * mm, "mid": v(17.87, 14.08) * mm, "end": v(17.95, 13.98) * mm});
            skArc(sketch, "E24.72.11", {"start": v(17.79, 14.19) * mm, "mid": v(17.7, 14.3) * mm, "end": v(17.62, 14.4) * mm});
            skPoint(sketch, "E24.73.0", {"position": v(16.86, 15.28) * mm});
            skPoint(sketch, "E24.73.1", {"position": v(16.5, 15.67) * mm});
            skPoint(sketch, "E24.73.2", {"position": v(16.55, 14.83) * mm});
            skPoint(sketch, "E24.73.3", {"position": v(16.02, 15.4) * mm});
            skPoint(sketch, "E24.73.4", {"position": v(16.18, 14.46) * mm});
            skPoint(sketch, "E24.73.5", {"position": v(15.63, 15.05) * mm});
            skArc(sketch, "E24.73.6", {"start": v(16.18, 14.46) * mm, "mid": v(16.31, 14.3) * mm, "end": v(16.44, 14.15) * mm});
            skArc(sketch, "E24.73.7", {"start": v(15.63, 15.05) * mm, "mid": v(16.03, 15.4) * mm, "end": v(16.5, 15.67) * mm});
            skArc(sketch, "E24.73.8", {"start": v(16.18, 14.46) * mm, "mid": v(16.56, 14.83) * mm, "end": v(16.86, 15.28) * mm});
            skArc(sketch, "E24.73.9", {"start": v(15.63, 15.05) * mm, "mid": v(15.48, 15.2) * mm, "end": v(15.34, 15.34) * mm});
            skArc(sketch, "E24.73.10", {"start": v(16.68, 15.48) * mm, "mid": v(16.77, 15.38) * mm, "end": v(16.86, 15.28) * mm});
            skArc(sketch, "E24.73.11", {"start": v(16.68, 15.48) * mm, "mid": v(16.59, 15.57) * mm, "end": v(16.5, 15.67) * mm});
            skPoint(sketch, "E24.74.0", {"position": v(15.67, 16.5) * mm});
            skPoint(sketch, "E24.74.1", {"position": v(15.28, 16.86) * mm});
            skPoint(sketch, "E24.74.2", {"position": v(15.4, 16.02) * mm});
            skPoint(sketch, "E24.74.3", {"position": v(14.83, 16.55) * mm});
            skPoint(sketch, "E24.74.4", {"position": v(15.05, 15.63) * mm});
            skPoint(sketch, "E24.74.5", {"position": v(14.46, 16.18) * mm});
            skArc(sketch, "E24.74.6", {"start": v(15.05, 15.63) * mm, "mid": v(15.2, 15.48) * mm, "end": v(15.34, 15.34) * mm});
            skArc(sketch, "E24.74.7", {"start": v(14.46, 16.18) * mm, "mid": v(14.83, 16.56) * mm, "end": v(15.28, 16.86) * mm});
            skArc(sketch, "E24.74.8", {"start": v(15.05, 15.63) * mm, "mid": v(15.4, 16.03) * mm, "end": v(15.67, 16.5) * mm});
            skArc(sketch, "E24.74.9", {"start": v(14.46, 16.18) * mm, "mid": v(14.3, 16.31) * mm, "end": v(14.15, 16.44) * mm});
            skArc(sketch, "E24.74.10", {"start": v(15.48, 16.68) * mm, "mid": v(15.57, 16.59) * mm, "end": v(15.67, 16.5) * mm});
            skArc(sketch, "E24.74.11", {"start": v(15.48, 16.68) * mm, "mid": v(15.38, 16.77) * mm, "end": v(15.28, 16.86) * mm});
            skPoint(sketch, "E24.75.0", {"position": v(14.4, 17.62) * mm});
            skPoint(sketch, "E24.75.1", {"position": v(13.98, 17.95) * mm});
            skPoint(sketch, "E24.75.2", {"position": v(14.16, 17.13) * mm});
            skPoint(sketch, "E24.75.3", {"position": v(13.55, 17.62) * mm});
            skPoint(sketch, "E24.75.4", {"position": v(13.84, 16.7) * mm});
            skPoint(sketch, "E24.75.5", {"position": v(13.2, 17.21) * mm});
            skArc(sketch, "E24.75.6", {"start": v(13.84, 16.7) * mm, "mid": v(14, 16.58) * mm, "end": v(14.15, 16.44) * mm});
            skArc(sketch, "E24.75.7", {"start": v(13.2, 17.21) * mm, "mid": v(13.56, 17.62) * mm, "end": v(13.98, 17.95) * mm});
            skArc(sketch, "E24.75.8", {"start": v(13.84, 16.7) * mm, "mid": v(14.16, 17.14) * mm, "end": v(14.4, 17.62) * mm});
            skArc(sketch, "E24.75.9", {"start": v(13.2, 17.21) * mm, "mid": v(13.05, 17.34) * mm, "end": v(12.88, 17.46) * mm});
            skArc(sketch, "E24.75.10", {"start": v(14.19, 17.79) * mm, "mid": v(14.3, 17.7) * mm, "end": v(14.4, 17.62) * mm});
            skArc(sketch, "E24.75.11", {"start": v(14.19, 17.79) * mm, "mid": v(14.08, 17.87) * mm, "end": v(13.98, 17.95) * mm});
            skPoint(sketch, "E24.76.0", {"position": v(13.04, 18.65) * mm});
            skPoint(sketch, "E24.76.1", {"position": v(12.6, 18.95) * mm});
            skPoint(sketch, "E24.76.2", {"position": v(12.84, 18.14) * mm});
            skPoint(sketch, "E24.76.3", {"position": v(12.2, 18.58) * mm});
            skPoint(sketch, "E24.76.4", {"position": v(12.55, 17.7) * mm});
            skPoint(sketch, "E24.76.5", {"position": v(11.88, 18.15) * mm});
            skArc(sketch, "E24.76.6", {"start": v(12.55, 17.7) * mm, "mid": v(12.72, 17.58) * mm, "end": v(12.88, 17.46) * mm});
            skArc(sketch, "E24.76.7", {"start": v(11.88, 18.15) * mm, "mid": v(12.2, 18.59) * mm, "end": v(12.6, 18.95) * mm});
            skArc(sketch, "E24.76.8", {"start": v(12.55, 17.7) * mm, "mid": v(12.84, 18.15) * mm, "end": v(13.04, 18.65) * mm});
            skArc(sketch, "E24.76.9", {"start": v(11.88, 18.15) * mm, "mid": v(11.71, 18.26) * mm, "end": v(11.54, 18.37) * mm});
            skArc(sketch, "E24.76.10", {"start": v(12.82, 18.8) * mm, "mid": v(12.93, 18.73) * mm, "end": v(13.04, 18.65) * mm});
            skArc(sketch, "E24.76.11", {"start": v(12.82, 18.8) * mm, "mid": v(12.7, 18.87) * mm, "end": v(12.6, 18.95) * mm});
            skPoint(sketch, "E24.77.0", {"position": v(11.6, 19.57) * mm});
            skPoint(sketch, "E24.77.1", {"position": v(11.15, 19.84) * mm});
            skPoint(sketch, "E24.77.2", {"position": v(11.45, 19.05) * mm});
            skPoint(sketch, "E24.77.3", {"position": v(10.77, 19.44) * mm});
            skPoint(sketch, "E24.77.4", {"position": v(11.2, 18.58) * mm});
            skPoint(sketch, "E24.77.5", {"position": v(10.5, 18.99) * mm});
            skArc(sketch, "E24.77.6", {"start": v(11.2, 18.58) * mm, "mid": v(11.37, 18.48) * mm, "end": v(11.54, 18.37) * mm});
            skArc(sketch, "E24.77.7", {"start": v(10.5, 18.99) * mm, "mid": v(10.78, 19.45) * mm, "end": v(11.15, 19.84) * mm});
            skArc(sketch, "E24.77.8", {"start": v(11.2, 18.58) * mm, "mid": v(11.45, 19.06) * mm, "end": v(11.6, 19.57) * mm});
            skArc(sketch, "E24.77.9", {"start": v(10.5, 18.99) * mm, "mid": v(10.32, 19.09) * mm, "end": v(10.14, 19.18) * mm});
            skArc(sketch, "E24.77.10", {"start": v(11.38, 19.7) * mm, "mid": v(11.5, 19.64) * mm, "end": v(11.6, 19.57) * mm});
            skArc(sketch, "E24.77.11", {"start": v(11.38, 19.7) * mm, "mid": v(11.26, 19.77) * mm, "end": v(11.15, 19.84) * mm});
            skPoint(sketch, "E24.78.0", {"position": v(10.11, 20.38) * mm});
            skPoint(sketch, "E24.78.1", {"position": v(9.63, 20.61) * mm});
            skPoint(sketch, "E24.78.2", {"position": v(10, 19.85) * mm});
            skPoint(sketch, "E24.78.3", {"position": v(9.3, 20.2) * mm});
            skPoint(sketch, "E24.78.4", {"position": v(9.78, 19.37) * mm});
            skPoint(sketch, "E24.78.5", {"position": v(9.05, 19.72) * mm});
            skArc(sketch, "E24.78.6", {"start": v(9.78, 19.37) * mm, "mid": v(9.96, 19.28) * mm, "end": v(10.14, 19.18) * mm});
            skArc(sketch, "E24.78.7", {"start": v(9.05, 19.72) * mm, "mid": v(9.3, 20.2) * mm, "end": v(9.63, 20.61) * mm});
            skArc(sketch, "E24.78.8", {"start": v(9.78, 19.37) * mm, "mid": v(10, 19.86) * mm, "end": v(10.11, 20.38) * mm});
            skArc(sketch, "E24.78.9", {"start": v(9.05, 19.72) * mm, "mid": v(8.86, 19.8) * mm, "end": v(8.68, 19.89) * mm});
            skArc(sketch, "E24.78.10", {"start": v(9.87, 20.5) * mm, "mid": v(10, 20.44) * mm, "end": v(10.11, 20.38) * mm});
            skArc(sketch, "E24.78.11", {"start": v(9.87, 20.5) * mm, "mid": v(9.75, 20.56) * mm, "end": v(9.63, 20.61) * mm});
            skPoint(sketch, "E24.79.0", {"position": v(8.56, 21.08) * mm});
            skPoint(sketch, "E24.79.1", {"position": v(8.06, 21.28) * mm});
            skPoint(sketch, "E24.79.2", {"position": v(8.48, 20.54) * mm});
            skPoint(sketch, "E24.79.3", {"position": v(7.76, 20.83) * mm});
            skPoint(sketch, "E24.79.4", {"position": v(8.3, 20.04) * mm});
            skPoint(sketch, "E24.79.5", {"position": v(7.55, 20.34) * mm});
            skArc(sketch, "E24.79.6", {"start": v(8.3, 20.04) * mm, "mid": v(8.49, 19.97) * mm, "end": v(8.68, 19.89) * mm});
            skArc(sketch, "E24.79.7", {"start": v(7.55, 20.34) * mm, "mid": v(7.76, 20.83) * mm, "end": v(8.06, 21.28) * mm});
            skArc(sketch, "E24.79.8", {"start": v(8.3, 20.04) * mm, "mid": v(8.48, 20.55) * mm, "end": v(8.56, 21.08) * mm});
            skArc(sketch, "E24.79.9", {"start": v(7.55, 20.34) * mm, "mid": v(7.36, 20.41) * mm, "end": v(7.17, 20.48) * mm});
            skArc(sketch, "E24.79.10", {"start": v(8.31, 21.18) * mm, "mid": v(8.44, 21.13) * mm, "end": v(8.56, 21.08) * mm});
            skArc(sketch, "E24.79.11", {"start": v(8.31, 21.18) * mm, "mid": v(8.19, 21.23) * mm, "end": v(8.06, 21.28) * mm});
            skPoint(sketch, "E24.80.0", {"position": v(6.96, 21.66) * mm});
            skPoint(sketch, "E24.80.1", {"position": v(6.45, 21.82) * mm});
            skPoint(sketch, "E24.80.2", {"position": v(6.92, 21.12) * mm});
            skPoint(sketch, "E24.80.3", {"position": v(6.18, 21.35) * mm});
            skPoint(sketch, "E24.80.4", {"position": v(6.78, 20.6) * mm});
            skPoint(sketch, "E24.80.5", {"position": v(6, 20.85) * mm});
            skArc(sketch, "E24.80.6", {"start": v(6.78, 20.6) * mm, "mid": v(6.97, 20.54) * mm, "end": v(7.17, 20.48) * mm});
            skArc(sketch, "E24.80.7", {"start": v(6, 20.85) * mm, "mid": v(6.18, 21.36) * mm, "end": v(6.45, 21.82) * mm});
            skArc(sketch, "E24.80.8", {"start": v(6.78, 20.6) * mm, "mid": v(6.92, 21.13) * mm, "end": v(6.96, 21.66) * mm});
            skArc(sketch, "E24.80.9", {"start": v(6, 20.85) * mm, "mid": v(5.81, 20.9) * mm, "end": v(5.62, 20.96) * mm});
            skArc(sketch, "E24.80.10", {"start": v(6.7, 21.74) * mm, "mid": v(6.83, 21.7) * mm, "end": v(6.96, 21.66) * mm});
            skArc(sketch, "E24.80.11", {"start": v(6.7, 21.74) * mm, "mid": v(6.58, 21.78) * mm, "end": v(6.45, 21.82) * mm});
            skPoint(sketch, "E24.81.0", {"position": v(5.32, 22.12) * mm});
            skPoint(sketch, "E24.81.1", {"position": v(4.8, 22.24) * mm});
            skPoint(sketch, "E24.81.2", {"position": v(5.32, 21.58) * mm});
            skPoint(sketch, "E24.81.3", {"position": v(4.56, 21.75) * mm});
            skPoint(sketch, "E24.81.4", {"position": v(5.22, 21.06) * mm});
            skPoint(sketch, "E24.81.5", {"position": v(4.43, 21.24) * mm});
            skArc(sketch, "E24.81.6", {"start": v(5.22, 21.06) * mm, "mid": v(5.42, 21) * mm, "end": v(5.62, 20.96) * mm});
            skArc(sketch, "E24.81.7", {"start": v(4.43, 21.24) * mm, "mid": v(4.57, 21.76) * mm, "end": v(4.8, 22.24) * mm});
            skArc(sketch, "E24.81.8", {"start": v(5.22, 21.06) * mm, "mid": v(5.33, 21.59) * mm, "end": v(5.32, 22.12) * mm});
            skArc(sketch, "E24.81.9", {"start": v(4.43, 21.24) * mm, "mid": v(4.23, 21.28) * mm, "end": v(4.03, 21.32) * mm});
            skArc(sketch, "E24.81.10", {"start": v(5.06, 22.18) * mm, "mid": v(5.2, 22.15) * mm, "end": v(5.32, 22.12) * mm});
            skArc(sketch, "E24.81.11", {"start": v(5.06, 22.18) * mm, "mid": v(4.93, 22.21) * mm, "end": v(4.8, 22.24) * mm});
            skPoint(sketch, "E24.82.0", {"position": v(3.65, 22.46) * mm});
            skPoint(sketch, "E24.82.1", {"position": v(3.13, 22.54) * mm});
            skPoint(sketch, "E24.82.2", {"position": v(3.7, 21.92) * mm});
            skPoint(sketch, "E24.82.3", {"position": v(2.93, 22.03) * mm});
            skPoint(sketch, "E24.82.4", {"position": v(3.63, 21.39) * mm});
            skPoint(sketch, "E24.82.5", {"position": v(2.83, 21.51) * mm});
            skArc(sketch, "E24.82.6", {"start": v(3.63, 21.39) * mm, "mid": v(3.83, 21.35) * mm, "end": v(4.03, 21.32) * mm});
            skArc(sketch, "E24.82.7", {"start": v(2.83, 21.51) * mm, "mid": v(2.93, 22.04) * mm, "end": v(3.13, 22.54) * mm});
            skArc(sketch, "E24.82.8", {"start": v(3.63, 21.39) * mm, "mid": v(3.7, 21.92) * mm, "end": v(3.65, 22.46) * mm});
            skArc(sketch, "E24.82.9", {"start": v(2.83, 21.51) * mm, "mid": v(2.63, 21.54) * mm, "end": v(2.43, 21.56) * mm});
            skArc(sketch, "E24.82.10", {"start": v(3.4, 22.5) * mm, "mid": v(3.52, 22.48) * mm, "end": v(3.65, 22.46) * mm});
            skArc(sketch, "E24.82.11", {"start": v(3.4, 22.5) * mm, "mid": v(3.26, 22.52) * mm, "end": v(3.13, 22.54) * mm});
            skPoint(sketch, "E24.83.0", {"position": v(1.97, 22.67) * mm});
            skPoint(sketch, "E24.83.1", {"position": v(1.44, 22.7) * mm});
            skPoint(sketch, "E24.83.2", {"position": v(2.05, 22.13) * mm});
            skPoint(sketch, "E24.83.3", {"position": v(1.27, 22.19) * mm});
            skPoint(sketch, "E24.83.4", {"position": v(2.03, 21.6) * mm});
            skPoint(sketch, "E24.83.5", {"position": v(1.22, 21.66) * mm});
            skArc(sketch, "E24.83.6", {"start": v(2.03, 21.6) * mm, "mid": v(2.23, 21.58) * mm, "end": v(2.43, 21.56) * mm});
            skArc(sketch, "E24.83.7", {"start": v(1.22, 21.66) * mm, "mid": v(1.27, 22.2) * mm, "end": v(1.44, 22.7) * mm});
            skArc(sketch, "E24.83.8", {"start": v(2.03, 21.6) * mm, "mid": v(2.05, 22.14) * mm, "end": v(1.97, 22.67) * mm});
            skArc(sketch, "E24.83.9", {"start": v(1.22, 21.66) * mm, "mid": v(1.01, 21.67) * mm, "end": v(0.81, 21.68) * mm});
            skArc(sketch, "E24.83.10", {"start": v(1.7, 22.7) * mm, "mid": v(1.83, 22.68) * mm, "end": v(1.97, 22.67) * mm});
            skArc(sketch, "E24.83.11", {"start": v(1.7, 22.7) * mm, "mid": v(1.57, 22.7) * mm, "end": v(1.44, 22.7) * mm});
            skPoint(sketch, "E25.1.0", {"position": v(-1.28, 17.42) * mm});
            skPoint(sketch, "E25.1.1", {"position": v(-2.14, 17.33) * mm});
            skPoint(sketch, "E25.1.2", {"position": v(-1.86, 16.3) * mm});
            skPoint(sketch, "E25.1.3", {"position": v(-1.27, 16.89) * mm});
            skPoint(sketch, "E25.1.4", {"position": v(-2.05, 16.8) * mm});
            skArc(sketch, "E25.1.5", {"start": v(-2.14, 17.33) * mm, "mid": v(-2.35, 17.3) * mm, "end": v(-2.56, 17.28) * mm});
            skArc(sketch, "E25.1.6", {"start": v(-1.86, 16.3) * mm, "mid": v(-2.05, 16.8) * mm, "end": v(-2.14, 17.33) * mm});
            skPoint(sketch, "E25.1.7", {"position": v(-1.36, 16.35) * mm});
            skArc(sketch, "E25.1.8", {"start": v(-1.36, 16.35) * mm, "mid": v(-1.27, 16.88) * mm, "end": v(-1.28, 17.42) * mm});
            skArc(sketch, "E25.1.9", {"start": v(-1.28, 17.42) * mm, "mid": v(-1.07, 17.43) * mm, "end": v(-0.86, 17.45) * mm});
            skArc(sketch, "E25.1.10", {"start": v(-1.6, 16.33) * mm, "mid": v(-1.48, 16.34) * mm, "end": v(-1.36, 16.35) * mm});
            skArc(sketch, "E25.1.11", {"start": v(-1.6, 16.33) * mm, "mid": v(-1.73, 16.31) * mm, "end": v(-1.86, 16.3) * mm});
            skPoint(sketch, "E25.2.0", {"position": v(-2.99, 17.2) * mm});
            skPoint(sketch, "E25.2.1", {"position": v(-3.83, 17.04) * mm});
            skPoint(sketch, "E25.2.2", {"position": v(-3.45, 16.04) * mm});
            skPoint(sketch, "E25.2.3", {"position": v(-2.92, 16.68) * mm});
            skPoint(sketch, "E25.2.4", {"position": v(-3.68, 16.53) * mm});
            skArc(sketch, "E25.2.5", {"start": v(-3.83, 17.04) * mm, "mid": v(-4.04, 17) * mm, "end": v(-4.25, 16.95) * mm});
            skArc(sketch, "E25.2.6", {"start": v(-3.45, 16.04) * mm, "mid": v(-3.68, 16.52) * mm, "end": v(-3.83, 17.04) * mm});
            skPoint(sketch, "E25.2.7", {"position": v(-2.95, 16.14) * mm});
            skArc(sketch, "E25.2.8", {"start": v(-2.95, 16.14) * mm, "mid": v(-2.92, 16.67) * mm, "end": v(-2.99, 17.2) * mm});
            skArc(sketch, "E25.2.9", {"start": v(-2.99, 17.2) * mm, "mid": v(-2.78, 17.25) * mm, "end": v(-2.56, 17.28) * mm});
            skArc(sketch, "E25.2.10", {"start": v(-3.2, 16.09) * mm, "mid": v(-3.08, 16.11) * mm, "end": v(-2.95, 16.14) * mm});
            skArc(sketch, "E25.2.11", {"start": v(-3.2, 16.09) * mm, "mid": v(-3.32, 16.06) * mm, "end": v(-3.45, 16.04) * mm});
            skPoint(sketch, "E25.3.0", {"position": v(-4.66, 16.83) * mm});
            skPoint(sketch, "E25.3.1", {"position": v(-5.48, 16.58) * mm});
            skPoint(sketch, "E25.3.2", {"position": v(-5, 15.62) * mm});
            skPoint(sketch, "E25.3.3", {"position": v(-4.54, 16.31) * mm});
            skPoint(sketch, "E25.3.4", {"position": v(-5.29, 16.09) * mm});
            skArc(sketch, "E25.3.5", {"start": v(-5.48, 16.58) * mm, "mid": v(-5.68, 16.52) * mm, "end": v(-5.89, 16.45) * mm});
            skArc(sketch, "E25.3.6", {"start": v(-5, 15.62) * mm, "mid": v(-5.28, 16.08) * mm, "end": v(-5.48, 16.58) * mm});
            skPoint(sketch, "E25.3.7", {"position": v(-4.52, 15.77) * mm});
            skArc(sketch, "E25.3.8", {"start": v(-4.52, 15.77) * mm, "mid": v(-4.54, 16.3) * mm, "end": v(-4.66, 16.83) * mm});
            skArc(sketch, "E25.3.9", {"start": v(-4.66, 16.83) * mm, "mid": v(-4.45, 16.9) * mm, "end": v(-4.25, 16.95) * mm});
            skArc(sketch, "E25.3.10", {"start": v(-4.76, 15.7) * mm, "mid": v(-4.64, 15.73) * mm, "end": v(-4.52, 15.77) * mm});
            skArc(sketch, "E25.3.11", {"start": v(-4.76, 15.7) * mm, "mid": v(-4.88, 15.66) * mm, "end": v(-5, 15.62) * mm});
            skPoint(sketch, "E25.4.0", {"position": v(-6.28, 16.3) * mm});
            skPoint(sketch, "E25.4.1", {"position": v(-7.08, 15.96) * mm});
            skPoint(sketch, "E25.4.2", {"position": v(-6.5, 15.06) * mm});
            skPoint(sketch, "E25.4.3", {"position": v(-6.12, 15.79) * mm});
            skPoint(sketch, "E25.4.4", {"position": v(-6.84, 15.5) * mm});
            skArc(sketch, "E25.4.5", {"start": v(-7.08, 15.96) * mm, "mid": v(-7.27, 15.88) * mm, "end": v(-7.47, 15.8) * mm});
            skArc(sketch, "E25.4.6", {"start": v(-6.5, 15.06) * mm, "mid": v(-6.83, 15.48) * mm, "end": v(-7.08, 15.96) * mm});
            skPoint(sketch, "E25.4.7", {"position": v(-6.04, 15.25) * mm});
            skArc(sketch, "E25.4.8", {"start": v(-6.04, 15.25) * mm, "mid": v(-6.12, 15.78) * mm, "end": v(-6.28, 16.3) * mm});
            skArc(sketch, "E25.4.9", {"start": v(-6.28, 16.3) * mm, "mid": v(-6.09, 16.37) * mm, "end": v(-5.89, 16.45) * mm});
            skArc(sketch, "E25.4.10", {"start": v(-6.28, 15.16) * mm, "mid": v(-6.16, 15.2) * mm, "end": v(-6.04, 15.25) * mm});
            skArc(sketch, "E25.4.11", {"start": v(-6.28, 15.16) * mm, "mid": v(-6.4, 15.1) * mm, "end": v(-6.5, 15.06) * mm});
            skPoint(sketch, "E25.5.0", {"position": v(-7.85, 15.6) * mm});
            skPoint(sketch, "E25.5.1", {"position": v(-8.6, 15.2) * mm});
            skPoint(sketch, "E25.5.2", {"position": v(-7.95, 14.35) * mm});
            skPoint(sketch, "E25.5.3", {"position": v(-7.64, 15.11) * mm});
            skPoint(sketch, "E25.5.4", {"position": v(-8.32, 14.75) * mm});
            skArc(sketch, "E25.5.5", {"start": v(-8.6, 15.2) * mm, "mid": v(-8.8, 15.1) * mm, "end": v(-8.98, 14.99) * mm});
            skArc(sketch, "E25.5.6", {"start": v(-7.95, 14.35) * mm, "mid": v(-8.32, 14.74) * mm, "end": v(-8.6, 15.2) * mm});
            skPoint(sketch, "E25.5.7", {"position": v(-7.51, 14.58) * mm});
            skArc(sketch, "E25.5.8", {"start": v(-7.51, 14.58) * mm, "mid": v(-7.63, 15.1) * mm, "end": v(-7.85, 15.6) * mm});
            skArc(sketch, "E25.5.9", {"start": v(-7.85, 15.6) * mm, "mid": v(-7.66, 15.7) * mm, "end": v(-7.47, 15.8) * mm});
            skArc(sketch, "E25.5.10", {"start": v(-7.73, 14.47) * mm, "mid": v(-7.62, 14.53) * mm, "end": v(-7.51, 14.58) * mm});
            skArc(sketch, "E25.5.11", {"start": v(-7.73, 14.47) * mm, "mid": v(-7.84, 14.4) * mm, "end": v(-7.95, 14.35) * mm});
            skPoint(sketch, "E25.6.0", {"position": v(-9.34, 14.75) * mm});
            skPoint(sketch, "E25.6.1", {"position": v(-10.06, 14.28) * mm});
            skPoint(sketch, "E25.6.2", {"position": v(-9.32, 13.5) * mm});
            skPoint(sketch, "E25.6.3", {"position": v(-9.08, 14.3) * mm});
            skPoint(sketch, "E25.6.4", {"position": v(-9.73, 13.86) * mm});
            skArc(sketch, "E25.6.5", {"start": v(-10.06, 14.28) * mm, "mid": v(-10.23, 14.16) * mm, "end": v(-10.4, 14.03) * mm});
            skArc(sketch, "E25.6.6", {"start": v(-9.32, 13.5) * mm, "mid": v(-9.72, 13.85) * mm, "end": v(-10.06, 14.28) * mm});
            skPoint(sketch, "E25.6.7", {"position": v(-8.9, 13.78) * mm});
            skArc(sketch, "E25.6.8", {"start": v(-8.9, 13.78) * mm, "mid": v(-9.08, 14.29) * mm, "end": v(-9.34, 14.75) * mm});
            skArc(sketch, "E25.6.9", {"start": v(-9.34, 14.75) * mm, "mid": v(-9.16, 14.87) * mm, "end": v(-8.98, 14.99) * mm});
            skArc(sketch, "E25.6.10", {"start": v(-9.11, 13.64) * mm, "mid": v(-9, 13.7) * mm, "end": v(-8.9, 13.78) * mm});
            skArc(sketch, "E25.6.11", {"start": v(-9.11, 13.64) * mm, "mid": v(-9.22, 13.57) * mm, "end": v(-9.32, 13.5) * mm});
            skPoint(sketch, "E25.7.0", {"position": v(-10.74, 13.77) * mm});
            skPoint(sketch, "E25.7.1", {"position": v(-11.4, 13.22) * mm});
            skPoint(sketch, "E25.7.2", {"position": v(-10.6, 12.52) * mm});
            skPoint(sketch, "E25.7.3", {"position": v(-10.44, 13.33) * mm});
            skPoint(sketch, "E25.7.4", {"position": v(-11.04, 12.84) * mm});
            skArc(sketch, "E25.7.5", {"start": v(-11.4, 13.22) * mm, "mid": v(-11.57, 13.09) * mm, "end": v(-11.73, 12.95) * mm});
            skArc(sketch, "E25.7.6", {"start": v(-10.6, 12.52) * mm, "mid": v(-11.04, 12.83) * mm, "end": v(-11.4, 13.22) * mm});
            skPoint(sketch, "E25.7.7", {"position": v(-10.21, 12.84) * mm});
            skArc(sketch, "E25.7.8", {"start": v(-10.21, 12.84) * mm, "mid": v(-10.43, 13.33) * mm, "end": v(-10.74, 13.77) * mm});
            skArc(sketch, "E25.7.9", {"start": v(-10.74, 13.77) * mm, "mid": v(-10.58, 13.9) * mm, "end": v(-10.4, 14.03) * mm});
            skArc(sketch, "E25.7.10", {"start": v(-10.4, 12.68) * mm, "mid": v(-10.3, 12.76) * mm, "end": v(-10.21, 12.84) * mm});
            skArc(sketch, "E25.7.11", {"start": v(-10.4, 12.68) * mm, "mid": v(-10.5, 12.6) * mm, "end": v(-10.6, 12.52) * mm});
            skPoint(sketch, "E25.8.0", {"position": v(-12.04, 12.65) * mm});
            skPoint(sketch, "E25.8.1", {"position": v(-12.65, 12.04) * mm});
            skPoint(sketch, "E25.8.2", {"position": v(-11.78, 11.42) * mm});
            skPoint(sketch, "E25.8.3", {"position": v(-11.7, 12.25) * mm});
            skPoint(sketch, "E25.8.4", {"position": v(-12.25, 11.7) * mm});
            skArc(sketch, "E25.8.5", {"start": v(-12.65, 12.04) * mm, "mid": v(-12.8, 11.89) * mm, "end": v(-12.95, 11.73) * mm});
            skArc(sketch, "E25.8.6", {"start": v(-11.78, 11.42) * mm, "mid": v(-12.24, 11.7) * mm, "end": v(-12.65, 12.04) * mm});
            skPoint(sketch, "E25.8.7", {"position": v(-11.42, 11.78) * mm});
            skArc(sketch, "E25.8.8", {"start": v(-11.42, 11.78) * mm, "mid": v(-11.7, 12.24) * mm, "end": v(-12.04, 12.65) * mm});
            skArc(sketch, "E25.8.9", {"start": v(-12.04, 12.65) * mm, "mid": v(-11.89, 12.8) * mm, "end": v(-11.73, 12.95) * mm});
            skArc(sketch, "E25.8.10", {"start": v(-11.6, 11.6) * mm, "mid": v(-11.51, 11.69) * mm, "end": v(-11.42, 11.78) * mm});
            skArc(sketch, "E25.8.11", {"start": v(-11.6, 11.6) * mm, "mid": v(-11.69, 11.51) * mm, "end": v(-11.78, 11.42) * mm});
            skPoint(sketch, "E25.9.0", {"position": v(-13.22, 11.4) * mm});
            skPoint(sketch, "E25.9.1", {"position": v(-13.77, 10.74) * mm});
            skPoint(sketch, "E25.9.2", {"position": v(-12.84, 10.21) * mm});
            skPoint(sketch, "E25.9.3", {"position": v(-12.84, 11.04) * mm});
            skPoint(sketch, "E25.9.4", {"position": v(-13.33, 10.44) * mm});
            skArc(sketch, "E25.9.5", {"start": v(-13.77, 10.74) * mm, "mid": v(-13.9, 10.58) * mm, "end": v(-14.03, 10.4) * mm});
            skArc(sketch, "E25.9.6", {"start": v(-12.84, 10.21) * mm, "mid": v(-13.33, 10.43) * mm, "end": v(-13.77, 10.74) * mm});
            skPoint(sketch, "E25.9.7", {"position": v(-12.52, 10.6) * mm});
            skArc(sketch, "E25.9.8", {"start": v(-12.52, 10.6) * mm, "mid": v(-12.83, 11.04) * mm, "end": v(-13.22, 11.4) * mm});
            skArc(sketch, "E25.9.9", {"start": v(-13.22, 11.4) * mm, "mid": v(-13.09, 11.57) * mm, "end": v(-12.95, 11.73) * mm});
            skArc(sketch, "E25.9.10", {"start": v(-12.68, 10.4) * mm, "mid": v(-12.6, 10.5) * mm, "end": v(-12.52, 10.6) * mm});
            skArc(sketch, "E25.9.11", {"start": v(-12.68, 10.4) * mm, "mid": v(-12.76, 10.3) * mm, "end": v(-12.84, 10.21) * mm});
            skPoint(sketch, "E25.10.0", {"position": v(-14.28, 10.06) * mm});
            skPoint(sketch, "E25.10.1", {"position": v(-14.75, 9.34) * mm});
            skPoint(sketch, "E25.10.2", {"position": v(-13.78, 8.9) * mm});
            skPoint(sketch, "E25.10.3", {"position": v(-13.86, 9.73) * mm});
            skPoint(sketch, "E25.10.4", {"position": v(-14.3, 9.08) * mm});
            skArc(sketch, "E25.10.5", {"start": v(-14.75, 9.34) * mm, "mid": v(-14.87, 9.16) * mm, "end": v(-14.99, 8.98) * mm});
            skArc(sketch, "E25.10.6", {"start": v(-13.78, 8.9) * mm, "mid": v(-14.29, 9.08) * mm, "end": v(-14.75, 9.34) * mm});
            skPoint(sketch, "E25.10.7", {"position": v(-13.5, 9.32) * mm});
            skArc(sketch, "E25.10.8", {"start": v(-13.5, 9.32) * mm, "mid": v(-13.85, 9.72) * mm, "end": v(-14.28, 10.06) * mm});
            skArc(sketch, "E25.10.9", {"start": v(-14.28, 10.06) * mm, "mid": v(-14.16, 10.23) * mm, "end": v(-14.03, 10.4) * mm});
            skArc(sketch, "E25.10.10", {"start": v(-13.64, 9.11) * mm, "mid": v(-13.57, 9.22) * mm, "end": v(-13.5, 9.32) * mm});
            skArc(sketch, "E25.10.11", {"start": v(-13.64, 9.11) * mm, "mid": v(-13.7, 9) * mm, "end": v(-13.78, 8.9) * mm});
            skPoint(sketch, "E25.11.0", {"position": v(-15.2, 8.6) * mm});
            skPoint(sketch, "E25.11.1", {"position": v(-15.6, 7.85) * mm});
            skPoint(sketch, "E25.11.2", {"position": v(-14.58, 7.51) * mm});
            skPoint(sketch, "E25.11.3", {"position": v(-14.75, 8.32) * mm});
            skPoint(sketch, "E25.11.4", {"position": v(-15.11, 7.64) * mm});
            skArc(sketch, "E25.11.5", {"start": v(-15.6, 7.85) * mm, "mid": v(-15.7, 7.66) * mm, "end": v(-15.8, 7.47) * mm});
            skArc(sketch, "E25.11.6", {"start": v(-14.58, 7.51) * mm, "mid": v(-15.1, 7.63) * mm, "end": v(-15.6, 7.85) * mm});
            skPoint(sketch, "E25.11.7", {"position": v(-14.35, 7.95) * mm});
            skArc(sketch, "E25.11.8", {"start": v(-14.35, 7.95) * mm, "mid": v(-14.74, 8.32) * mm, "end": v(-15.2, 8.6) * mm});
            skArc(sketch, "E25.11.9", {"start": v(-15.2, 8.6) * mm, "mid": v(-15.1, 8.8) * mm, "end": v(-14.99, 8.98) * mm});
            skArc(sketch, "E25.11.10", {"start": v(-14.47, 7.73) * mm, "mid": v(-14.4, 7.84) * mm, "end": v(-14.35, 7.95) * mm});
            skArc(sketch, "E25.11.11", {"start": v(-14.47, 7.73) * mm, "mid": v(-14.53, 7.62) * mm, "end": v(-14.58, 7.51) * mm});
            skPoint(sketch, "E25.12.0", {"position": v(-15.96, 7.08) * mm});
            skPoint(sketch, "E25.12.1", {"position": v(-16.3, 6.28) * mm});
            skPoint(sketch, "E25.12.2", {"position": v(-15.25, 6.04) * mm});
            skPoint(sketch, "E25.12.3", {"position": v(-15.5, 6.84) * mm});
            skPoint(sketch, "E25.12.4", {"position": v(-15.79, 6.12) * mm});
            skArc(sketch, "E25.12.5", {"start": v(-16.3, 6.28) * mm, "mid": v(-16.37, 6.09) * mm, "end": v(-16.45, 5.89) * mm});
            skArc(sketch, "E25.12.6", {"start": v(-15.25, 6.04) * mm, "mid": v(-15.78, 6.12) * mm, "end": v(-16.3, 6.28) * mm});
            skPoint(sketch, "E25.12.7", {"position": v(-15.06, 6.5) * mm});
            skArc(sketch, "E25.12.8", {"start": v(-15.06, 6.5) * mm, "mid": v(-15.48, 6.83) * mm, "end": v(-15.96, 7.08) * mm});
            skArc(sketch, "E25.12.9", {"start": v(-15.96, 7.08) * mm, "mid": v(-15.88, 7.27) * mm, "end": v(-15.8, 7.47) * mm});
            skArc(sketch, "E25.12.10", {"start": v(-15.16, 6.28) * mm, "mid": v(-15.1, 6.4) * mm, "end": v(-15.06, 6.5) * mm});
            skArc(sketch, "E25.12.11", {"start": v(-15.16, 6.28) * mm, "mid": v(-15.2, 6.16) * mm, "end": v(-15.25, 6.04) * mm});
            skPoint(sketch, "E25.13.0", {"position": v(-16.58, 5.48) * mm});
            skPoint(sketch, "E25.13.1", {"position": v(-16.83, 4.66) * mm});
            skPoint(sketch, "E25.13.2", {"position": v(-15.77, 4.52) * mm});
            skPoint(sketch, "E25.13.3", {"position": v(-16.09, 5.29) * mm});
            skPoint(sketch, "E25.13.4", {"position": v(-16.31, 4.54) * mm});
            skArc(sketch, "E25.13.5", {"start": v(-16.83, 4.66) * mm, "mid": v(-16.9, 4.45) * mm, "end": v(-16.95, 4.25) * mm});
            skArc(sketch, "E25.13.6", {"start": v(-15.77, 4.52) * mm, "mid": v(-16.3, 4.54) * mm, "end": v(-16.83, 4.66) * mm});
            skPoint(sketch, "E25.13.7", {"position": v(-15.62, 5) * mm});
            skArc(sketch, "E25.13.8", {"start": v(-15.62, 5) * mm, "mid": v(-16.08, 5.28) * mm, "end": v(-16.58, 5.48) * mm});
            skArc(sketch, "E25.13.9", {"start": v(-16.58, 5.48) * mm, "mid": v(-16.52, 5.68) * mm, "end": v(-16.45, 5.89) * mm});
            skArc(sketch, "E25.13.10", {"start": v(-15.7, 4.76) * mm, "mid": v(-15.66, 4.88) * mm, "end": v(-15.62, 5) * mm});
            skArc(sketch, "E25.13.11", {"start": v(-15.7, 4.76) * mm, "mid": v(-15.73, 4.64) * mm, "end": v(-15.77, 4.52) * mm});
            skPoint(sketch, "E25.14.0", {"position": v(-17.04, 3.83) * mm});
            skPoint(sketch, "E25.14.1", {"position": v(-17.2, 2.99) * mm});
            skPoint(sketch, "E25.14.2", {"position": v(-16.14, 2.95) * mm});
            skPoint(sketch, "E25.14.3", {"position": v(-16.53, 3.68) * mm});
            skPoint(sketch, "E25.14.4", {"position": v(-16.68, 2.92) * mm});
            skArc(sketch, "E25.14.5", {"start": v(-17.2, 2.99) * mm, "mid": v(-17.25, 2.78) * mm, "end": v(-17.28, 2.56) * mm});
            skArc(sketch, "E25.14.6", {"start": v(-16.14, 2.95) * mm, "mid": v(-16.67, 2.92) * mm, "end": v(-17.2, 2.99) * mm});
            skPoint(sketch, "E25.14.7", {"position": v(-16.04, 3.45) * mm});
            skArc(sketch, "E25.14.8", {"start": v(-16.04, 3.45) * mm, "mid": v(-16.52, 3.68) * mm, "end": v(-17.04, 3.83) * mm});
            skArc(sketch, "E25.14.9", {"start": v(-17.04, 3.83) * mm, "mid": v(-17, 4.04) * mm, "end": v(-16.95, 4.25) * mm});
            skArc(sketch, "E25.14.10", {"start": v(-16.09, 3.2) * mm, "mid": v(-16.06, 3.32) * mm, "end": v(-16.04, 3.45) * mm});
            skArc(sketch, "E25.14.11", {"start": v(-16.09, 3.2) * mm, "mid": v(-16.11, 3.08) * mm, "end": v(-16.14, 2.95) * mm});
            skPoint(sketch, "E25.15.0", {"position": v(-17.33, 2.14) * mm});
            skPoint(sketch, "E25.15.1", {"position": v(-17.42, 1.28) * mm});
            skPoint(sketch, "E25.15.2", {"position": v(-16.35, 1.36) * mm});
            skPoint(sketch, "E25.15.3", {"position": v(-16.8, 2.05) * mm});
            skPoint(sketch, "E25.15.4", {"position": v(-16.89, 1.27) * mm});
            skArc(sketch, "E25.15.5", {"start": v(-17.42, 1.28) * mm, "mid": v(-17.43, 1.07) * mm, "end": v(-17.45, 0.86) * mm});
            skArc(sketch, "E25.15.6", {"start": v(-16.35, 1.36) * mm, "mid": v(-16.88, 1.27) * mm, "end": v(-17.42, 1.28) * mm});
            skPoint(sketch, "E25.15.7", {"position": v(-16.3, 1.86) * mm});
            skArc(sketch, "E25.15.8", {"start": v(-16.3, 1.86) * mm, "mid": v(-16.8, 2.05) * mm, "end": v(-17.33, 2.14) * mm});
            skArc(sketch, "E25.15.9", {"start": v(-17.33, 2.14) * mm, "mid": v(-17.3, 2.35) * mm, "end": v(-17.28, 2.56) * mm});
            skArc(sketch, "E25.15.10", {"start": v(-16.33, 1.6) * mm, "mid": v(-16.31, 1.73) * mm, "end": v(-16.3, 1.86) * mm});
            skArc(sketch, "E25.15.11", {"start": v(-16.33, 1.6) * mm, "mid": v(-16.34, 1.48) * mm, "end": v(-16.35, 1.36) * mm});
            skPoint(sketch, "E25.16.0", {"position": v(-17.46, 0.43) * mm});
            skPoint(sketch, "E25.16.1", {"position": v(-17.46, -0.43) * mm});
            skPoint(sketch, "E25.16.2", {"position": v(-16.4, -0.25) * mm});
            skPoint(sketch, "E25.16.3", {"position": v(-16.93, 0.39) * mm});
            skPoint(sketch, "E25.16.4", {"position": v(-16.93, -0.39) * mm});
            skArc(sketch, "E25.16.5", {"start": v(-17.46, -0.43) * mm, "mid": v(-17.46, -0.64) * mm, "end": v(-17.45, -0.86) * mm});
            skArc(sketch, "E25.16.6", {"start": v(-16.4, -0.25) * mm, "mid": v(-16.92, -0.39) * mm, "end": v(-17.46, -0.43) * mm});
            skPoint(sketch, "E25.16.7", {"position": v(-16.4, 0.25) * mm});
            skArc(sketch, "E25.16.8", {"start": v(-16.4, 0.25) * mm, "mid": v(-16.92, 0.39) * mm, "end": v(-17.46, 0.43) * mm});
            skArc(sketch, "E25.16.9", {"start": v(-17.46, 0.43) * mm, "mid": v(-17.46, 0.64) * mm, "end": v(-17.45, 0.86) * mm});
            skArc(sketch, "E25.16.10", {"start": v(-16.4, 0) * mm, "mid": v(-16.4, 0.13) * mm, "end": v(-16.4, 0.25) * mm});
            skArc(sketch, "E25.16.11", {"start": v(-16.4, 0) * mm, "mid": v(-16.4, -0.13) * mm, "end": v(-16.4, -0.25) * mm});
            skPoint(sketch, "E25.17.0", {"position": v(-17.42, -1.28) * mm});
            skPoint(sketch, "E25.17.1", {"position": v(-17.33, -2.14) * mm});
            skPoint(sketch, "E25.17.2", {"position": v(-16.3, -1.86) * mm});
            skPoint(sketch, "E25.17.3", {"position": v(-16.89, -1.27) * mm});
            skPoint(sketch, "E25.17.4", {"position": v(-16.8, -2.05) * mm});
            skArc(sketch, "E25.17.5", {"start": v(-17.33, -2.14) * mm, "mid": v(-17.3, -2.35) * mm, "end": v(-17.28, -2.56) * mm});
            skArc(sketch, "E25.17.6", {"start": v(-16.3, -1.86) * mm, "mid": v(-16.8, -2.05) * mm, "end": v(-17.33, -2.14) * mm});
            skPoint(sketch, "E25.17.7", {"position": v(-16.35, -1.36) * mm});
            skArc(sketch, "E25.17.8", {"start": v(-16.35, -1.36) * mm, "mid": v(-16.88, -1.27) * mm, "end": v(-17.42, -1.28) * mm});
            skArc(sketch, "E25.17.9", {"start": v(-17.42, -1.28) * mm, "mid": v(-17.43, -1.07) * mm, "end": v(-17.45, -0.86) * mm});
            skArc(sketch, "E25.17.10", {"start": v(-16.33, -1.6) * mm, "mid": v(-16.34, -1.48) * mm, "end": v(-16.35, -1.36) * mm});
            skArc(sketch, "E25.17.11", {"start": v(-16.33, -1.6) * mm, "mid": v(-16.31, -1.73) * mm, "end": v(-16.3, -1.86) * mm});
            skPoint(sketch, "E25.18.0", {"position": v(-17.2, -2.99) * mm});
            skPoint(sketch, "E25.18.1", {"position": v(-17.04, -3.83) * mm});
            skPoint(sketch, "E25.18.2", {"position": v(-16.04, -3.45) * mm});
            skPoint(sketch, "E25.18.3", {"position": v(-16.68, -2.92) * mm});
            skPoint(sketch, "E25.18.4", {"position": v(-16.53, -3.68) * mm});
            skArc(sketch, "E25.18.5", {"start": v(-17.04, -3.83) * mm, "mid": v(-17, -4.04) * mm, "end": v(-16.95, -4.25) * mm});
            skArc(sketch, "E25.18.6", {"start": v(-16.04, -3.45) * mm, "mid": v(-16.52, -3.68) * mm, "end": v(-17.04, -3.83) * mm});
            skPoint(sketch, "E25.18.7", {"position": v(-16.14, -2.95) * mm});
            skArc(sketch, "E25.18.8", {"start": v(-16.14, -2.95) * mm, "mid": v(-16.67, -2.92) * mm, "end": v(-17.2, -2.99) * mm});
            skArc(sketch, "E25.18.9", {"start": v(-17.2, -2.99) * mm, "mid": v(-17.25, -2.78) * mm, "end": v(-17.28, -2.56) * mm});
            skArc(sketch, "E25.18.10", {"start": v(-16.09, -3.2) * mm, "mid": v(-16.11, -3.08) * mm, "end": v(-16.14, -2.95) * mm});
            skArc(sketch, "E25.18.11", {"start": v(-16.09, -3.2) * mm, "mid": v(-16.06, -3.32) * mm, "end": v(-16.04, -3.45) * mm});
            skPoint(sketch, "E25.19.0", {"position": v(-16.83, -4.66) * mm});
            skPoint(sketch, "E25.19.1", {"position": v(-16.58, -5.48) * mm});
            skPoint(sketch, "E25.19.2", {"position": v(-15.62, -5) * mm});
            skPoint(sketch, "E25.19.3", {"position": v(-16.31, -4.54) * mm});
            skPoint(sketch, "E25.19.4", {"position": v(-16.09, -5.29) * mm});
            skArc(sketch, "E25.19.5", {"start": v(-16.58, -5.48) * mm, "mid": v(-16.52, -5.68) * mm, "end": v(-16.45, -5.89) * mm});
            skArc(sketch, "E25.19.6", {"start": v(-15.62, -5) * mm, "mid": v(-16.08, -5.28) * mm, "end": v(-16.58, -5.48) * mm});
            skPoint(sketch, "E25.19.7", {"position": v(-15.77, -4.52) * mm});
            skArc(sketch, "E25.19.8", {"start": v(-15.77, -4.52) * mm, "mid": v(-16.3, -4.54) * mm, "end": v(-16.83, -4.66) * mm});
            skArc(sketch, "E25.19.9", {"start": v(-16.83, -4.66) * mm, "mid": v(-16.9, -4.45) * mm, "end": v(-16.95, -4.25) * mm});
            skArc(sketch, "E25.19.10", {"start": v(-15.7, -4.76) * mm, "mid": v(-15.73, -4.64) * mm, "end": v(-15.77, -4.52) * mm});
            skArc(sketch, "E25.19.11", {"start": v(-15.7, -4.76) * mm, "mid": v(-15.66, -4.88) * mm, "end": v(-15.62, -5) * mm});
            skPoint(sketch, "E25.20.0", {"position": v(-16.3, -6.28) * mm});
            skPoint(sketch, "E25.20.1", {"position": v(-15.96, -7.08) * mm});
            skPoint(sketch, "E25.20.2", {"position": v(-15.06, -6.5) * mm});
            skPoint(sketch, "E25.20.3", {"position": v(-15.79, -6.12) * mm});
            skPoint(sketch, "E25.20.4", {"position": v(-15.5, -6.84) * mm});
            skArc(sketch, "E25.20.5", {"start": v(-15.96, -7.08) * mm, "mid": v(-15.88, -7.27) * mm, "end": v(-15.8, -7.47) * mm});
            skArc(sketch, "E25.20.6", {"start": v(-15.06, -6.5) * mm, "mid": v(-15.48, -6.83) * mm, "end": v(-15.96, -7.08) * mm});
            skPoint(sketch, "E25.20.7", {"position": v(-15.25, -6.04) * mm});
            skArc(sketch, "E25.20.8", {"start": v(-15.25, -6.04) * mm, "mid": v(-15.78, -6.12) * mm, "end": v(-16.3, -6.28) * mm});
            skArc(sketch, "E25.20.9", {"start": v(-16.3, -6.28) * mm, "mid": v(-16.37, -6.09) * mm, "end": v(-16.45, -5.89) * mm});
            skArc(sketch, "E25.20.10", {"start": v(-15.16, -6.28) * mm, "mid": v(-15.2, -6.16) * mm, "end": v(-15.25, -6.04) * mm});
            skArc(sketch, "E25.20.11", {"start": v(-15.16, -6.28) * mm, "mid": v(-15.1, -6.4) * mm, "end": v(-15.06, -6.5) * mm});
            skPoint(sketch, "E25.21.0", {"position": v(-15.6, -7.85) * mm});
            skPoint(sketch, "E25.21.1", {"position": v(-15.2, -8.6) * mm});
            skPoint(sketch, "E25.21.2", {"position": v(-14.35, -7.95) * mm});
            skPoint(sketch, "E25.21.3", {"position": v(-15.11, -7.64) * mm});
            skPoint(sketch, "E25.21.4", {"position": v(-14.75, -8.32) * mm});
            skArc(sketch, "E25.21.5", {"start": v(-15.2, -8.6) * mm, "mid": v(-15.1, -8.8) * mm, "end": v(-14.99, -8.98) * mm});
            skArc(sketch, "E25.21.6", {"start": v(-14.35, -7.95) * mm, "mid": v(-14.74, -8.32) * mm, "end": v(-15.2, -8.6) * mm});
            skPoint(sketch, "E25.21.7", {"position": v(-14.58, -7.51) * mm});
            skArc(sketch, "E25.21.8", {"start": v(-14.58, -7.51) * mm, "mid": v(-15.1, -7.63) * mm, "end": v(-15.6, -7.85) * mm});
            skArc(sketch, "E25.21.9", {"start": v(-15.6, -7.85) * mm, "mid": v(-15.7, -7.66) * mm, "end": v(-15.8, -7.47) * mm});
            skArc(sketch, "E25.21.10", {"start": v(-14.47, -7.73) * mm, "mid": v(-14.53, -7.62) * mm, "end": v(-14.58, -7.51) * mm});
            skArc(sketch, "E25.21.11", {"start": v(-14.47, -7.73) * mm, "mid": v(-14.4, -7.84) * mm, "end": v(-14.35, -7.95) * mm});
            skPoint(sketch, "E25.22.0", {"position": v(-14.75, -9.34) * mm});
            skPoint(sketch, "E25.22.1", {"position": v(-14.28, -10.06) * mm});
            skPoint(sketch, "E25.22.2", {"position": v(-13.5, -9.32) * mm});
            skPoint(sketch, "E25.22.3", {"position": v(-14.3, -9.08) * mm});
            skPoint(sketch, "E25.22.4", {"position": v(-13.86, -9.73) * mm});
            skArc(sketch, "E25.22.5", {"start": v(-14.28, -10.06) * mm, "mid": v(-14.16, -10.23) * mm, "end": v(-14.03, -10.4) * mm});
            skArc(sketch, "E25.22.6", {"start": v(-13.5, -9.32) * mm, "mid": v(-13.85, -9.72) * mm, "end": v(-14.28, -10.06) * mm});
            skPoint(sketch, "E25.22.7", {"position": v(-13.78, -8.9) * mm});
            skArc(sketch, "E25.22.8", {"start": v(-13.78, -8.9) * mm, "mid": v(-14.29, -9.08) * mm, "end": v(-14.75, -9.34) * mm});
            skArc(sketch, "E25.22.9", {"start": v(-14.75, -9.34) * mm, "mid": v(-14.87, -9.16) * mm, "end": v(-14.99, -8.98) * mm});
            skArc(sketch, "E25.22.10", {"start": v(-13.64, -9.11) * mm, "mid": v(-13.7, -9) * mm, "end": v(-13.78, -8.9) * mm});
            skArc(sketch, "E25.22.11", {"start": v(-13.64, -9.11) * mm, "mid": v(-13.57, -9.22) * mm, "end": v(-13.5, -9.32) * mm});
            skPoint(sketch, "E25.23.0", {"position": v(-13.77, -10.74) * mm});
            skPoint(sketch, "E25.23.1", {"position": v(-13.22, -11.4) * mm});
            skPoint(sketch, "E25.23.2", {"position": v(-12.52, -10.6) * mm});
            skPoint(sketch, "E25.23.3", {"position": v(-13.33, -10.44) * mm});
            skPoint(sketch, "E25.23.4", {"position": v(-12.84, -11.04) * mm});
            skArc(sketch, "E25.23.5", {"start": v(-13.22, -11.4) * mm, "mid": v(-13.09, -11.57) * mm, "end": v(-12.95, -11.73) * mm});
            skArc(sketch, "E25.23.6", {"start": v(-12.52, -10.6) * mm, "mid": v(-12.83, -11.04) * mm, "end": v(-13.22, -11.4) * mm});
            skPoint(sketch, "E25.23.7", {"position": v(-12.84, -10.21) * mm});
            skArc(sketch, "E25.23.8", {"start": v(-12.84, -10.21) * mm, "mid": v(-13.33, -10.43) * mm, "end": v(-13.77, -10.74) * mm});
            skArc(sketch, "E25.23.9", {"start": v(-13.77, -10.74) * mm, "mid": v(-13.9, -10.58) * mm, "end": v(-14.03, -10.4) * mm});
            skArc(sketch, "E25.23.10", {"start": v(-12.68, -10.4) * mm, "mid": v(-12.76, -10.3) * mm, "end": v(-12.84, -10.21) * mm});
            skArc(sketch, "E25.23.11", {"start": v(-12.68, -10.4) * mm, "mid": v(-12.6, -10.5) * mm, "end": v(-12.52, -10.6) * mm});
            skPoint(sketch, "E25.24.0", {"position": v(-12.65, -12.04) * mm});
            skPoint(sketch, "E25.24.1", {"position": v(-12.04, -12.65) * mm});
            skPoint(sketch, "E25.24.2", {"position": v(-11.42, -11.78) * mm});
            skPoint(sketch, "E25.24.3", {"position": v(-12.25, -11.7) * mm});
            skPoint(sketch, "E25.24.4", {"position": v(-11.7, -12.25) * mm});
            skArc(sketch, "E25.24.5", {"start": v(-12.04, -12.65) * mm, "mid": v(-11.89, -12.8) * mm, "end": v(-11.73, -12.95) * mm});
            skArc(sketch, "E25.24.6", {"start": v(-11.42, -11.78) * mm, "mid": v(-11.7, -12.24) * mm, "end": v(-12.04, -12.65) * mm});
            skPoint(sketch, "E25.24.7", {"position": v(-11.78, -11.42) * mm});
            skArc(sketch, "E25.24.8", {"start": v(-11.78, -11.42) * mm, "mid": v(-12.24, -11.7) * mm, "end": v(-12.65, -12.04) * mm});
            skArc(sketch, "E25.24.9", {"start": v(-12.65, -12.04) * mm, "mid": v(-12.8, -11.89) * mm, "end": v(-12.95, -11.73) * mm});
            skArc(sketch, "E25.24.10", {"start": v(-11.6, -11.6) * mm, "mid": v(-11.69, -11.51) * mm, "end": v(-11.78, -11.42) * mm});
            skArc(sketch, "E25.24.11", {"start": v(-11.6, -11.6) * mm, "mid": v(-11.51, -11.69) * mm, "end": v(-11.42, -11.78) * mm});
            skPoint(sketch, "E25.25.0", {"position": v(-11.4, -13.22) * mm});
            skPoint(sketch, "E25.25.1", {"position": v(-10.74, -13.77) * mm});
            skPoint(sketch, "E25.25.2", {"position": v(-10.21, -12.84) * mm});
            skPoint(sketch, "E25.25.3", {"position": v(-11.04, -12.84) * mm});
            skPoint(sketch, "E25.25.4", {"position": v(-10.44, -13.33) * mm});
            skArc(sketch, "E25.25.5", {"start": v(-10.74, -13.77) * mm, "mid": v(-10.58, -13.9) * mm, "end": v(-10.4, -14.03) * mm});
            skArc(sketch, "E25.25.6", {"start": v(-10.21, -12.84) * mm, "mid": v(-10.43, -13.33) * mm, "end": v(-10.74, -13.77) * mm});
            skPoint(sketch, "E25.25.7", {"position": v(-10.6, -12.52) * mm});
            skArc(sketch, "E25.25.8", {"start": v(-10.6, -12.52) * mm, "mid": v(-11.04, -12.83) * mm, "end": v(-11.4, -13.22) * mm});
            skArc(sketch, "E25.25.9", {"start": v(-11.4, -13.22) * mm, "mid": v(-11.57, -13.09) * mm, "end": v(-11.73, -12.95) * mm});
            skArc(sketch, "E25.25.10", {"start": v(-10.4, -12.68) * mm, "mid": v(-10.5, -12.6) * mm, "end": v(-10.6, -12.52) * mm});
            skArc(sketch, "E25.25.11", {"start": v(-10.4, -12.68) * mm, "mid": v(-10.3, -12.76) * mm, "end": v(-10.21, -12.84) * mm});
            skPoint(sketch, "E25.26.0", {"position": v(-10.06, -14.28) * mm});
            skPoint(sketch, "E25.26.1", {"position": v(-9.34, -14.75) * mm});
            skPoint(sketch, "E25.26.2", {"position": v(-8.9, -13.78) * mm});
            skPoint(sketch, "E25.26.3", {"position": v(-9.73, -13.86) * mm});
            skPoint(sketch, "E25.26.4", {"position": v(-9.08, -14.3) * mm});
            skArc(sketch, "E25.26.5", {"start": v(-9.34, -14.75) * mm, "mid": v(-9.16, -14.87) * mm, "end": v(-8.98, -14.99) * mm});
            skArc(sketch, "E25.26.6", {"start": v(-8.9, -13.78) * mm, "mid": v(-9.08, -14.29) * mm, "end": v(-9.34, -14.75) * mm});
            skPoint(sketch, "E25.26.7", {"position": v(-9.32, -13.5) * mm});
            skArc(sketch, "E25.26.8", {"start": v(-9.32, -13.5) * mm, "mid": v(-9.72, -13.85) * mm, "end": v(-10.06, -14.28) * mm});
            skArc(sketch, "E25.26.9", {"start": v(-10.06, -14.28) * mm, "mid": v(-10.23, -14.16) * mm, "end": v(-10.4, -14.03) * mm});
            skArc(sketch, "E25.26.10", {"start": v(-9.11, -13.64) * mm, "mid": v(-9.22, -13.57) * mm, "end": v(-9.32, -13.5) * mm});
            skArc(sketch, "E25.26.11", {"start": v(-9.11, -13.64) * mm, "mid": v(-9, -13.7) * mm, "end": v(-8.9, -13.78) * mm});
            skPoint(sketch, "E25.27.0", {"position": v(-8.6, -15.2) * mm});
            skPoint(sketch, "E25.27.1", {"position": v(-7.85, -15.6) * mm});
            skPoint(sketch, "E25.27.2", {"position": v(-7.51, -14.58) * mm});
            skPoint(sketch, "E25.27.3", {"position": v(-8.32, -14.75) * mm});
            skPoint(sketch, "E25.27.4", {"position": v(-7.64, -15.11) * mm});
            skArc(sketch, "E25.27.5", {"start": v(-7.85, -15.6) * mm, "mid": v(-7.66, -15.7) * mm, "end": v(-7.47, -15.8) * mm});
            skArc(sketch, "E25.27.6", {"start": v(-7.51, -14.58) * mm, "mid": v(-7.63, -15.1) * mm, "end": v(-7.85, -15.6) * mm});
            skPoint(sketch, "E25.27.7", {"position": v(-7.95, -14.35) * mm});
            skArc(sketch, "E25.27.8", {"start": v(-7.95, -14.35) * mm, "mid": v(-8.32, -14.74) * mm, "end": v(-8.6, -15.2) * mm});
            skArc(sketch, "E25.27.9", {"start": v(-8.6, -15.2) * mm, "mid": v(-8.8, -15.1) * mm, "end": v(-8.98, -14.99) * mm});
            skArc(sketch, "E25.27.10", {"start": v(-7.73, -14.47) * mm, "mid": v(-7.84, -14.4) * mm, "end": v(-7.95, -14.35) * mm});
            skArc(sketch, "E25.27.11", {"start": v(-7.73, -14.47) * mm, "mid": v(-7.62, -14.53) * mm, "end": v(-7.51, -14.58) * mm});
            skPoint(sketch, "E25.28.0", {"position": v(-7.08, -15.96) * mm});
            skPoint(sketch, "E25.28.1", {"position": v(-6.28, -16.3) * mm});
            skPoint(sketch, "E25.28.2", {"position": v(-6.04, -15.25) * mm});
            skPoint(sketch, "E25.28.3", {"position": v(-6.84, -15.5) * mm});
            skPoint(sketch, "E25.28.4", {"position": v(-6.12, -15.79) * mm});
            skArc(sketch, "E25.28.5", {"start": v(-6.28, -16.3) * mm, "mid": v(-6.09, -16.37) * mm, "end": v(-5.89, -16.45) * mm});
            skArc(sketch, "E25.28.6", {"start": v(-6.04, -15.25) * mm, "mid": v(-6.12, -15.78) * mm, "end": v(-6.28, -16.3) * mm});
            skPoint(sketch, "E25.28.7", {"position": v(-6.5, -15.06) * mm});
            skArc(sketch, "E25.28.8", {"start": v(-6.5, -15.06) * mm, "mid": v(-6.83, -15.48) * mm, "end": v(-7.08, -15.96) * mm});
            skArc(sketch, "E25.28.9", {"start": v(-7.08, -15.96) * mm, "mid": v(-7.27, -15.88) * mm, "end": v(-7.47, -15.8) * mm});
            skArc(sketch, "E25.28.10", {"start": v(-6.28, -15.16) * mm, "mid": v(-6.4, -15.1) * mm, "end": v(-6.5, -15.06) * mm});
            skArc(sketch, "E25.28.11", {"start": v(-6.28, -15.16) * mm, "mid": v(-6.16, -15.2) * mm, "end": v(-6.04, -15.25) * mm});
            skPoint(sketch, "E25.29.0", {"position": v(-5.48, -16.58) * mm});
            skPoint(sketch, "E25.29.1", {"position": v(-4.66, -16.83) * mm});
            skPoint(sketch, "E25.29.2", {"position": v(-4.52, -15.77) * mm});
            skPoint(sketch, "E25.29.3", {"position": v(-5.29, -16.09) * mm});
            skPoint(sketch, "E25.29.4", {"position": v(-4.54, -16.31) * mm});
            skArc(sketch, "E25.29.5", {"start": v(-4.66, -16.83) * mm, "mid": v(-4.45, -16.9) * mm, "end": v(-4.25, -16.95) * mm});
            skArc(sketch, "E25.29.6", {"start": v(-4.52, -15.77) * mm, "mid": v(-4.54, -16.3) * mm, "end": v(-4.66, -16.83) * mm});
            skPoint(sketch, "E25.29.7", {"position": v(-5, -15.62) * mm});
            skArc(sketch, "E25.29.8", {"start": v(-5, -15.62) * mm, "mid": v(-5.28, -16.08) * mm, "end": v(-5.48, -16.58) * mm});
            skArc(sketch, "E25.29.9", {"start": v(-5.48, -16.58) * mm, "mid": v(-5.68, -16.52) * mm, "end": v(-5.89, -16.45) * mm});
            skArc(sketch, "E25.29.10", {"start": v(-4.76, -15.7) * mm, "mid": v(-4.88, -15.66) * mm, "end": v(-5, -15.62) * mm});
            skArc(sketch, "E25.29.11", {"start": v(-4.76, -15.7) * mm, "mid": v(-4.64, -15.73) * mm, "end": v(-4.52, -15.77) * mm});
            skPoint(sketch, "E25.30.0", {"position": v(-3.83, -17.04) * mm});
            skPoint(sketch, "E25.30.1", {"position": v(-2.99, -17.2) * mm});
            skPoint(sketch, "E25.30.2", {"position": v(-2.95, -16.14) * mm});
            skPoint(sketch, "E25.30.3", {"position": v(-3.68, -16.53) * mm});
            skPoint(sketch, "E25.30.4", {"position": v(-2.92, -16.68) * mm});
            skArc(sketch, "E25.30.5", {"start": v(-2.99, -17.2) * mm, "mid": v(-2.78, -17.25) * mm, "end": v(-2.56, -17.28) * mm});
            skArc(sketch, "E25.30.6", {"start": v(-2.95, -16.14) * mm, "mid": v(-2.92, -16.67) * mm, "end": v(-2.99, -17.2) * mm});
            skPoint(sketch, "E25.30.7", {"position": v(-3.45, -16.04) * mm});
            skArc(sketch, "E25.30.8", {"start": v(-3.45, -16.04) * mm, "mid": v(-3.68, -16.52) * mm, "end": v(-3.83, -17.04) * mm});
            skArc(sketch, "E25.30.9", {"start": v(-3.83, -17.04) * mm, "mid": v(-4.04, -17) * mm, "end": v(-4.25, -16.95) * mm});
            skArc(sketch, "E25.30.10", {"start": v(-3.2, -16.09) * mm, "mid": v(-3.32, -16.06) * mm, "end": v(-3.45, -16.04) * mm});
            skArc(sketch, "E25.30.11", {"start": v(-3.2, -16.09) * mm, "mid": v(-3.08, -16.11) * mm, "end": v(-2.95, -16.14) * mm});
            skPoint(sketch, "E25.31.0", {"position": v(-2.14, -17.33) * mm});
            skPoint(sketch, "E25.31.1", {"position": v(-1.28, -17.42) * mm});
            skPoint(sketch, "E25.31.2", {"position": v(-1.36, -16.35) * mm});
            skPoint(sketch, "E25.31.3", {"position": v(-2.05, -16.8) * mm});
            skPoint(sketch, "E25.31.4", {"position": v(-1.27, -16.89) * mm});
            skArc(sketch, "E25.31.5", {"start": v(-1.28, -17.42) * mm, "mid": v(-1.07, -17.43) * mm, "end": v(-0.86, -17.45) * mm});
            skArc(sketch, "E25.31.6", {"start": v(-1.36, -16.35) * mm, "mid": v(-1.27, -16.88) * mm, "end": v(-1.28, -17.42) * mm});
            skPoint(sketch, "E25.31.7", {"position": v(-1.86, -16.3) * mm});
            skArc(sketch, "E25.31.8", {"start": v(-1.86, -16.3) * mm, "mid": v(-2.05, -16.8) * mm, "end": v(-2.14, -17.33) * mm});
            skArc(sketch, "E25.31.9", {"start": v(-2.14, -17.33) * mm, "mid": v(-2.35, -17.3) * mm, "end": v(-2.56, -17.28) * mm});
            skArc(sketch, "E25.31.10", {"start": v(-1.6, -16.33) * mm, "mid": v(-1.73, -16.31) * mm, "end": v(-1.86, -16.3) * mm});
            skArc(sketch, "E25.31.11", {"start": v(-1.6, -16.33) * mm, "mid": v(-1.48, -16.34) * mm, "end": v(-1.36, -16.35) * mm});
            skPoint(sketch, "E25.32.0", {"position": v(-0.43, -17.46) * mm});
            skPoint(sketch, "E25.32.1", {"position": v(0.43, -17.46) * mm});
            skPoint(sketch, "E25.32.2", {"position": v(0.25, -16.4) * mm});
            skPoint(sketch, "E25.32.3", {"position": v(-0.39, -16.93) * mm});
            skPoint(sketch, "E25.32.4", {"position": v(0.39, -16.93) * mm});
            skArc(sketch, "E25.32.5", {"start": v(0.43, -17.46) * mm, "mid": v(0.64, -17.46) * mm, "end": v(0.86, -17.45) * mm});
            skArc(sketch, "E25.32.6", {"start": v(0.25, -16.4) * mm, "mid": v(0.39, -16.92) * mm, "end": v(0.43, -17.46) * mm});
            skPoint(sketch, "E25.32.7", {"position": v(-0.25, -16.4) * mm});
            skArc(sketch, "E25.32.8", {"start": v(-0.25, -16.4) * mm, "mid": v(-0.39, -16.92) * mm, "end": v(-0.43, -17.46) * mm});
            skArc(sketch, "E25.32.9", {"start": v(-0.43, -17.46) * mm, "mid": v(-0.64, -17.46) * mm, "end": v(-0.86, -17.45) * mm});
            skArc(sketch, "E25.32.10", {"start": v(0, -16.4) * mm, "mid": v(-0.13, -16.4) * mm, "end": v(-0.25, -16.4) * mm});
            skArc(sketch, "E25.32.11", {"start": v(0, -16.4) * mm, "mid": v(0.13, -16.4) * mm, "end": v(0.25, -16.4) * mm});
            skPoint(sketch, "E25.33.0", {"position": v(1.28, -17.42) * mm});
            skPoint(sketch, "E25.33.1", {"position": v(2.14, -17.33) * mm});
            skPoint(sketch, "E25.33.2", {"position": v(1.86, -16.3) * mm});
            skPoint(sketch, "E25.33.3", {"position": v(1.27, -16.89) * mm});
            skPoint(sketch, "E25.33.4", {"position": v(2.05, -16.8) * mm});
            skArc(sketch, "E25.33.5", {"start": v(2.14, -17.33) * mm, "mid": v(2.35, -17.3) * mm, "end": v(2.56, -17.28) * mm});
            skArc(sketch, "E25.33.6", {"start": v(1.86, -16.3) * mm, "mid": v(2.05, -16.8) * mm, "end": v(2.14, -17.33) * mm});
            skPoint(sketch, "E25.33.7", {"position": v(1.36, -16.35) * mm});
            skArc(sketch, "E25.33.8", {"start": v(1.36, -16.35) * mm, "mid": v(1.27, -16.88) * mm, "end": v(1.28, -17.42) * mm});
            skArc(sketch, "E25.33.9", {"start": v(1.28, -17.42) * mm, "mid": v(1.07, -17.43) * mm, "end": v(0.86, -17.45) * mm});
            skArc(sketch, "E25.33.10", {"start": v(1.6, -16.33) * mm, "mid": v(1.48, -16.34) * mm, "end": v(1.36, -16.35) * mm});
            skArc(sketch, "E25.33.11", {"start": v(1.6, -16.33) * mm, "mid": v(1.73, -16.31) * mm, "end": v(1.86, -16.3) * mm});
            skPoint(sketch, "E25.34.0", {"position": v(2.99, -17.2) * mm});
            skPoint(sketch, "E25.34.1", {"position": v(3.83, -17.04) * mm});
            skPoint(sketch, "E25.34.2", {"position": v(3.45, -16.04) * mm});
            skPoint(sketch, "E25.34.3", {"position": v(2.92, -16.68) * mm});
            skPoint(sketch, "E25.34.4", {"position": v(3.68, -16.53) * mm});
            skArc(sketch, "E25.34.5", {"start": v(3.83, -17.04) * mm, "mid": v(4.04, -17) * mm, "end": v(4.25, -16.95) * mm});
            skArc(sketch, "E25.34.6", {"start": v(3.45, -16.04) * mm, "mid": v(3.68, -16.52) * mm, "end": v(3.83, -17.04) * mm});
            skPoint(sketch, "E25.34.7", {"position": v(2.95, -16.14) * mm});
            skArc(sketch, "E25.34.8", {"start": v(2.95, -16.14) * mm, "mid": v(2.92, -16.67) * mm, "end": v(2.99, -17.2) * mm});
            skArc(sketch, "E25.34.9", {"start": v(2.99, -17.2) * mm, "mid": v(2.78, -17.25) * mm, "end": v(2.56, -17.28) * mm});
            skArc(sketch, "E25.34.10", {"start": v(3.2, -16.09) * mm, "mid": v(3.08, -16.11) * mm, "end": v(2.95, -16.14) * mm});
            skArc(sketch, "E25.34.11", {"start": v(3.2, -16.09) * mm, "mid": v(3.32, -16.06) * mm, "end": v(3.45, -16.04) * mm});
            skPoint(sketch, "E25.35.0", {"position": v(4.66, -16.83) * mm});
            skPoint(sketch, "E25.35.1", {"position": v(5.48, -16.58) * mm});
            skPoint(sketch, "E25.35.2", {"position": v(5, -15.62) * mm});
            skPoint(sketch, "E25.35.3", {"position": v(4.54, -16.31) * mm});
            skPoint(sketch, "E25.35.4", {"position": v(5.29, -16.09) * mm});
            skArc(sketch, "E25.35.5", {"start": v(5.48, -16.58) * mm, "mid": v(5.68, -16.52) * mm, "end": v(5.89, -16.45) * mm});
            skArc(sketch, "E25.35.6", {"start": v(5, -15.62) * mm, "mid": v(5.28, -16.08) * mm, "end": v(5.48, -16.58) * mm});
            skPoint(sketch, "E25.35.7", {"position": v(4.52, -15.77) * mm});
            skArc(sketch, "E25.35.8", {"start": v(4.52, -15.77) * mm, "mid": v(4.54, -16.3) * mm, "end": v(4.66, -16.83) * mm});
            skArc(sketch, "E25.35.9", {"start": v(4.66, -16.83) * mm, "mid": v(4.45, -16.9) * mm, "end": v(4.25, -16.95) * mm});
            skArc(sketch, "E25.35.10", {"start": v(4.76, -15.7) * mm, "mid": v(4.64, -15.73) * mm, "end": v(4.52, -15.77) * mm});
            skArc(sketch, "E25.35.11", {"start": v(4.76, -15.7) * mm, "mid": v(4.88, -15.66) * mm, "end": v(5, -15.62) * mm});
            skPoint(sketch, "E25.36.0", {"position": v(6.28, -16.3) * mm});
            skPoint(sketch, "E25.36.1", {"position": v(7.08, -15.96) * mm});
            skPoint(sketch, "E25.36.2", {"position": v(6.5, -15.06) * mm});
            skPoint(sketch, "E25.36.3", {"position": v(6.12, -15.79) * mm});
            skPoint(sketch, "E25.36.4", {"position": v(6.84, -15.5) * mm});
            skArc(sketch, "E25.36.5", {"start": v(7.08, -15.96) * mm, "mid": v(7.27, -15.88) * mm, "end": v(7.47, -15.8) * mm});
            skArc(sketch, "E25.36.6", {"start": v(6.5, -15.06) * mm, "mid": v(6.83, -15.48) * mm, "end": v(7.08, -15.96) * mm});
            skPoint(sketch, "E25.36.7", {"position": v(6.04, -15.25) * mm});
            skArc(sketch, "E25.36.8", {"start": v(6.04, -15.25) * mm, "mid": v(6.12, -15.78) * mm, "end": v(6.28, -16.3) * mm});
            skArc(sketch, "E25.36.9", {"start": v(6.28, -16.3) * mm, "mid": v(6.09, -16.37) * mm, "end": v(5.89, -16.45) * mm});
            skArc(sketch, "E25.36.10", {"start": v(6.28, -15.16) * mm, "mid": v(6.16, -15.2) * mm, "end": v(6.04, -15.25) * mm});
            skArc(sketch, "E25.36.11", {"start": v(6.28, -15.16) * mm, "mid": v(6.4, -15.1) * mm, "end": v(6.5, -15.06) * mm});
            skPoint(sketch, "E25.37.0", {"position": v(7.85, -15.6) * mm});
            skPoint(sketch, "E25.37.1", {"position": v(8.6, -15.2) * mm});
            skPoint(sketch, "E25.37.2", {"position": v(7.95, -14.35) * mm});
            skPoint(sketch, "E25.37.3", {"position": v(7.64, -15.11) * mm});
            skPoint(sketch, "E25.37.4", {"position": v(8.32, -14.75) * mm});
            skArc(sketch, "E25.37.5", {"start": v(8.6, -15.2) * mm, "mid": v(8.8, -15.1) * mm, "end": v(8.98, -14.99) * mm});
            skArc(sketch, "E25.37.6", {"start": v(7.95, -14.35) * mm, "mid": v(8.32, -14.74) * mm, "end": v(8.6, -15.2) * mm});
            skPoint(sketch, "E25.37.7", {"position": v(7.51, -14.58) * mm});
            skArc(sketch, "E25.37.8", {"start": v(7.51, -14.58) * mm, "mid": v(7.63, -15.1) * mm, "end": v(7.85, -15.6) * mm});
            skArc(sketch, "E25.37.9", {"start": v(7.85, -15.6) * mm, "mid": v(7.66, -15.7) * mm, "end": v(7.47, -15.8) * mm});
            skArc(sketch, "E25.37.10", {"start": v(7.73, -14.47) * mm, "mid": v(7.62, -14.53) * mm, "end": v(7.51, -14.58) * mm});
            skArc(sketch, "E25.37.11", {"start": v(7.73, -14.47) * mm, "mid": v(7.84, -14.4) * mm, "end": v(7.95, -14.35) * mm});
            skPoint(sketch, "E25.38.0", {"position": v(9.34, -14.75) * mm});
            skPoint(sketch, "E25.38.1", {"position": v(10.06, -14.28) * mm});
            skPoint(sketch, "E25.38.2", {"position": v(9.32, -13.5) * mm});
            skPoint(sketch, "E25.38.3", {"position": v(9.08, -14.3) * mm});
            skPoint(sketch, "E25.38.4", {"position": v(9.73, -13.86) * mm});
            skArc(sketch, "E25.38.5", {"start": v(10.06, -14.28) * mm, "mid": v(10.23, -14.16) * mm, "end": v(10.4, -14.03) * mm});
            skArc(sketch, "E25.38.6", {"start": v(9.32, -13.5) * mm, "mid": v(9.72, -13.85) * mm, "end": v(10.06, -14.28) * mm});
            skPoint(sketch, "E25.38.7", {"position": v(8.9, -13.78) * mm});
            skArc(sketch, "E25.38.8", {"start": v(8.9, -13.78) * mm, "mid": v(9.08, -14.29) * mm, "end": v(9.34, -14.75) * mm});
            skArc(sketch, "E25.38.9", {"start": v(9.34, -14.75) * mm, "mid": v(9.16, -14.87) * mm, "end": v(8.98, -14.99) * mm});
            skArc(sketch, "E25.38.10", {"start": v(9.11, -13.64) * mm, "mid": v(9, -13.7) * mm, "end": v(8.9, -13.78) * mm});
            skArc(sketch, "E25.38.11", {"start": v(9.11, -13.64) * mm, "mid": v(9.22, -13.57) * mm, "end": v(9.32, -13.5) * mm});
            skPoint(sketch, "E25.39.0", {"position": v(10.74, -13.77) * mm});
            skPoint(sketch, "E25.39.1", {"position": v(11.4, -13.22) * mm});
            skPoint(sketch, "E25.39.2", {"position": v(10.6, -12.52) * mm});
            skPoint(sketch, "E25.39.3", {"position": v(10.44, -13.33) * mm});
            skPoint(sketch, "E25.39.4", {"position": v(11.04, -12.84) * mm});
            skArc(sketch, "E25.39.5", {"start": v(11.4, -13.22) * mm, "mid": v(11.57, -13.09) * mm, "end": v(11.73, -12.95) * mm});
            skArc(sketch, "E25.39.6", {"start": v(10.6, -12.52) * mm, "mid": v(11.04, -12.83) * mm, "end": v(11.4, -13.22) * mm});
            skPoint(sketch, "E25.39.7", {"position": v(10.21, -12.84) * mm});
            skArc(sketch, "E25.39.8", {"start": v(10.21, -12.84) * mm, "mid": v(10.43, -13.33) * mm, "end": v(10.74, -13.77) * mm});
            skArc(sketch, "E25.39.9", {"start": v(10.74, -13.77) * mm, "mid": v(10.58, -13.9) * mm, "end": v(10.4, -14.03) * mm});
            skArc(sketch, "E25.39.10", {"start": v(10.4, -12.68) * mm, "mid": v(10.3, -12.76) * mm, "end": v(10.21, -12.84) * mm});
            skArc(sketch, "E25.39.11", {"start": v(10.4, -12.68) * mm, "mid": v(10.5, -12.6) * mm, "end": v(10.6, -12.52) * mm});
            skPoint(sketch, "E25.40.0", {"position": v(12.04, -12.65) * mm});
            skPoint(sketch, "E25.40.1", {"position": v(12.65, -12.04) * mm});
            skPoint(sketch, "E25.40.2", {"position": v(11.78, -11.42) * mm});
            skPoint(sketch, "E25.40.3", {"position": v(11.7, -12.25) * mm});
            skPoint(sketch, "E25.40.4", {"position": v(12.25, -11.7) * mm});
            skArc(sketch, "E25.40.5", {"start": v(12.65, -12.04) * mm, "mid": v(12.8, -11.89) * mm, "end": v(12.95, -11.73) * mm});
            skArc(sketch, "E25.40.6", {"start": v(11.78, -11.42) * mm, "mid": v(12.24, -11.7) * mm, "end": v(12.65, -12.04) * mm});
            skPoint(sketch, "E25.40.7", {"position": v(11.42, -11.78) * mm});
            skArc(sketch, "E25.40.8", {"start": v(11.42, -11.78) * mm, "mid": v(11.7, -12.24) * mm, "end": v(12.04, -12.65) * mm});
            skArc(sketch, "E25.40.9", {"start": v(12.04, -12.65) * mm, "mid": v(11.89, -12.8) * mm, "end": v(11.73, -12.95) * mm});
            skArc(sketch, "E25.40.10", {"start": v(11.6, -11.6) * mm, "mid": v(11.51, -11.69) * mm, "end": v(11.42, -11.78) * mm});
            skArc(sketch, "E25.40.11", {"start": v(11.6, -11.6) * mm, "mid": v(11.69, -11.51) * mm, "end": v(11.78, -11.42) * mm});
            skPoint(sketch, "E25.41.0", {"position": v(13.22, -11.4) * mm});
            skPoint(sketch, "E25.41.1", {"position": v(13.77, -10.74) * mm});
            skPoint(sketch, "E25.41.2", {"position": v(12.84, -10.21) * mm});
            skPoint(sketch, "E25.41.3", {"position": v(12.84, -11.04) * mm});
            skPoint(sketch, "E25.41.4", {"position": v(13.33, -10.44) * mm});
            skArc(sketch, "E25.41.5", {"start": v(13.77, -10.74) * mm, "mid": v(13.9, -10.58) * mm, "end": v(14.03, -10.4) * mm});
            skArc(sketch, "E25.41.6", {"start": v(12.84, -10.21) * mm, "mid": v(13.33, -10.43) * mm, "end": v(13.77, -10.74) * mm});
            skPoint(sketch, "E25.41.7", {"position": v(12.52, -10.6) * mm});
            skArc(sketch, "E25.41.8", {"start": v(12.52, -10.6) * mm, "mid": v(12.83, -11.04) * mm, "end": v(13.22, -11.4) * mm});
            skArc(sketch, "E25.41.9", {"start": v(13.22, -11.4) * mm, "mid": v(13.09, -11.57) * mm, "end": v(12.95, -11.73) * mm});
            skArc(sketch, "E25.41.10", {"start": v(12.68, -10.4) * mm, "mid": v(12.6, -10.5) * mm, "end": v(12.52, -10.6) * mm});
            skArc(sketch, "E25.41.11", {"start": v(12.68, -10.4) * mm, "mid": v(12.76, -10.3) * mm, "end": v(12.84, -10.21) * mm});
            skPoint(sketch, "E25.42.0", {"position": v(14.28, -10.06) * mm});
            skPoint(sketch, "E25.42.1", {"position": v(14.75, -9.34) * mm});
            skPoint(sketch, "E25.42.2", {"position": v(13.78, -8.9) * mm});
            skPoint(sketch, "E25.42.3", {"position": v(13.86, -9.73) * mm});
            skPoint(sketch, "E25.42.4", {"position": v(14.3, -9.08) * mm});
            skArc(sketch, "E25.42.5", {"start": v(14.75, -9.34) * mm, "mid": v(14.87, -9.16) * mm, "end": v(14.99, -8.98) * mm});
            skArc(sketch, "E25.42.6", {"start": v(13.78, -8.9) * mm, "mid": v(14.29, -9.08) * mm, "end": v(14.75, -9.34) * mm});
            skPoint(sketch, "E25.42.7", {"position": v(13.5, -9.32) * mm});
            skArc(sketch, "E25.42.8", {"start": v(13.5, -9.32) * mm, "mid": v(13.85, -9.72) * mm, "end": v(14.28, -10.06) * mm});
            skArc(sketch, "E25.42.9", {"start": v(14.28, -10.06) * mm, "mid": v(14.16, -10.23) * mm, "end": v(14.03, -10.4) * mm});
            skArc(sketch, "E25.42.10", {"start": v(13.64, -9.11) * mm, "mid": v(13.57, -9.22) * mm, "end": v(13.5, -9.32) * mm});
            skArc(sketch, "E25.42.11", {"start": v(13.64, -9.11) * mm, "mid": v(13.7, -9) * mm, "end": v(13.78, -8.9) * mm});
            skPoint(sketch, "E25.43.0", {"position": v(15.2, -8.6) * mm});
            skPoint(sketch, "E25.43.1", {"position": v(15.6, -7.85) * mm});
            skPoint(sketch, "E25.43.2", {"position": v(14.58, -7.51) * mm});
            skPoint(sketch, "E25.43.3", {"position": v(14.75, -8.32) * mm});
            skPoint(sketch, "E25.43.4", {"position": v(15.11, -7.64) * mm});
            skArc(sketch, "E25.43.5", {"start": v(15.6, -7.85) * mm, "mid": v(15.7, -7.66) * mm, "end": v(15.8, -7.47) * mm});
            skArc(sketch, "E25.43.6", {"start": v(14.58, -7.51) * mm, "mid": v(15.1, -7.63) * mm, "end": v(15.6, -7.85) * mm});
            skPoint(sketch, "E25.43.7", {"position": v(14.35, -7.95) * mm});
            skArc(sketch, "E25.43.8", {"start": v(14.35, -7.95) * mm, "mid": v(14.74, -8.32) * mm, "end": v(15.2, -8.6) * mm});
            skArc(sketch, "E25.43.9", {"start": v(15.2, -8.6) * mm, "mid": v(15.1, -8.8) * mm, "end": v(14.99, -8.98) * mm});
            skArc(sketch, "E25.43.10", {"start": v(14.47, -7.73) * mm, "mid": v(14.4, -7.84) * mm, "end": v(14.35, -7.95) * mm});
            skArc(sketch, "E25.43.11", {"start": v(14.47, -7.73) * mm, "mid": v(14.53, -7.62) * mm, "end": v(14.58, -7.51) * mm});
            skPoint(sketch, "E25.44.0", {"position": v(15.96, -7.08) * mm});
            skPoint(sketch, "E25.44.1", {"position": v(16.3, -6.28) * mm});
            skPoint(sketch, "E25.44.2", {"position": v(15.25, -6.04) * mm});
            skPoint(sketch, "E25.44.3", {"position": v(15.5, -6.84) * mm});
            skPoint(sketch, "E25.44.4", {"position": v(15.79, -6.12) * mm});
            skArc(sketch, "E25.44.5", {"start": v(16.3, -6.28) * mm, "mid": v(16.37, -6.09) * mm, "end": v(16.45, -5.89) * mm});
            skArc(sketch, "E25.44.6", {"start": v(15.25, -6.04) * mm, "mid": v(15.78, -6.12) * mm, "end": v(16.3, -6.28) * mm});
            skPoint(sketch, "E25.44.7", {"position": v(15.06, -6.5) * mm});
            skArc(sketch, "E25.44.8", {"start": v(15.06, -6.5) * mm, "mid": v(15.48, -6.83) * mm, "end": v(15.96, -7.08) * mm});
            skArc(sketch, "E25.44.9", {"start": v(15.96, -7.08) * mm, "mid": v(15.88, -7.27) * mm, "end": v(15.8, -7.47) * mm});
            skArc(sketch, "E25.44.10", {"start": v(15.16, -6.28) * mm, "mid": v(15.1, -6.4) * mm, "end": v(15.06, -6.5) * mm});
            skArc(sketch, "E25.44.11", {"start": v(15.16, -6.28) * mm, "mid": v(15.2, -6.16) * mm, "end": v(15.25, -6.04) * mm});
            skPoint(sketch, "E25.45.0", {"position": v(16.58, -5.48) * mm});
            skPoint(sketch, "E25.45.1", {"position": v(16.83, -4.66) * mm});
            skPoint(sketch, "E25.45.2", {"position": v(15.77, -4.52) * mm});
            skPoint(sketch, "E25.45.3", {"position": v(16.09, -5.29) * mm});
            skPoint(sketch, "E25.45.4", {"position": v(16.31, -4.54) * mm});
            skArc(sketch, "E25.45.5", {"start": v(16.83, -4.66) * mm, "mid": v(16.9, -4.45) * mm, "end": v(16.95, -4.25) * mm});
            skArc(sketch, "E25.45.6", {"start": v(15.77, -4.52) * mm, "mid": v(16.3, -4.54) * mm, "end": v(16.83, -4.66) * mm});
            skPoint(sketch, "E25.45.7", {"position": v(15.62, -5) * mm});
            skArc(sketch, "E25.45.8", {"start": v(15.62, -5) * mm, "mid": v(16.08, -5.28) * mm, "end": v(16.58, -5.48) * mm});
            skArc(sketch, "E25.45.9", {"start": v(16.58, -5.48) * mm, "mid": v(16.52, -5.68) * mm, "end": v(16.45, -5.89) * mm});
            skArc(sketch, "E25.45.10", {"start": v(15.7, -4.76) * mm, "mid": v(15.66, -4.88) * mm, "end": v(15.62, -5) * mm});
            skArc(sketch, "E25.45.11", {"start": v(15.7, -4.76) * mm, "mid": v(15.73, -4.64) * mm, "end": v(15.77, -4.52) * mm});
            skPoint(sketch, "E25.46.0", {"position": v(17.04, -3.83) * mm});
            skPoint(sketch, "E25.46.1", {"position": v(17.2, -2.99) * mm});
            skPoint(sketch, "E25.46.2", {"position": v(16.14, -2.95) * mm});
            skPoint(sketch, "E25.46.3", {"position": v(16.53, -3.68) * mm});
            skPoint(sketch, "E25.46.4", {"position": v(16.68, -2.92) * mm});
            skArc(sketch, "E25.46.5", {"start": v(17.2, -2.99) * mm, "mid": v(17.25, -2.78) * mm, "end": v(17.28, -2.56) * mm});
            skArc(sketch, "E25.46.6", {"start": v(16.14, -2.95) * mm, "mid": v(16.67, -2.92) * mm, "end": v(17.2, -2.99) * mm});
            skPoint(sketch, "E25.46.7", {"position": v(16.04, -3.45) * mm});
            skArc(sketch, "E25.46.8", {"start": v(16.04, -3.45) * mm, "mid": v(16.52, -3.68) * mm, "end": v(17.04, -3.83) * mm});
            skArc(sketch, "E25.46.9", {"start": v(17.04, -3.83) * mm, "mid": v(17, -4.04) * mm, "end": v(16.95, -4.25) * mm});
            skArc(sketch, "E25.46.10", {"start": v(16.09, -3.2) * mm, "mid": v(16.06, -3.32) * mm, "end": v(16.04, -3.45) * mm});
            skArc(sketch, "E25.46.11", {"start": v(16.09, -3.2) * mm, "mid": v(16.11, -3.08) * mm, "end": v(16.14, -2.95) * mm});
            skPoint(sketch, "E25.47.0", {"position": v(17.33, -2.14) * mm});
            skPoint(sketch, "E25.47.1", {"position": v(17.42, -1.28) * mm});
            skPoint(sketch, "E25.47.2", {"position": v(16.35, -1.36) * mm});
            skPoint(sketch, "E25.47.3", {"position": v(16.8, -2.05) * mm});
            skPoint(sketch, "E25.47.4", {"position": v(16.89, -1.27) * mm});
            skArc(sketch, "E25.47.5", {"start": v(17.42, -1.28) * mm, "mid": v(17.43, -1.07) * mm, "end": v(17.45, -0.86) * mm});
            skArc(sketch, "E25.47.6", {"start": v(16.35, -1.36) * mm, "mid": v(16.88, -1.27) * mm, "end": v(17.42, -1.28) * mm});
            skPoint(sketch, "E25.47.7", {"position": v(16.3, -1.86) * mm});
            skArc(sketch, "E25.47.8", {"start": v(16.3, -1.86) * mm, "mid": v(16.8, -2.05) * mm, "end": v(17.33, -2.14) * mm});
            skArc(sketch, "E25.47.9", {"start": v(17.33, -2.14) * mm, "mid": v(17.3, -2.35) * mm, "end": v(17.28, -2.56) * mm});
            skArc(sketch, "E25.47.10", {"start": v(16.33, -1.6) * mm, "mid": v(16.31, -1.73) * mm, "end": v(16.3, -1.86) * mm});
            skArc(sketch, "E25.47.11", {"start": v(16.33, -1.6) * mm, "mid": v(16.34, -1.48) * mm, "end": v(16.35, -1.36) * mm});
            skPoint(sketch, "E25.48.0", {"position": v(17.46, -0.43) * mm});
            skPoint(sketch, "E25.48.1", {"position": v(17.46, 0.43) * mm});
            skPoint(sketch, "E25.48.2", {"position": v(16.4, 0.25) * mm});
            skPoint(sketch, "E25.48.3", {"position": v(16.93, -0.39) * mm});
            skPoint(sketch, "E25.48.4", {"position": v(16.93, 0.39) * mm});
            skArc(sketch, "E25.48.5", {"start": v(17.46, 0.43) * mm, "mid": v(17.46, 0.64) * mm, "end": v(17.45, 0.86) * mm});
            skArc(sketch, "E25.48.6", {"start": v(16.4, 0.25) * mm, "mid": v(16.92, 0.39) * mm, "end": v(17.46, 0.43) * mm});
            skPoint(sketch, "E25.48.7", {"position": v(16.4, -0.25) * mm});
            skArc(sketch, "E25.48.8", {"start": v(16.4, -0.25) * mm, "mid": v(16.92, -0.39) * mm, "end": v(17.46, -0.43) * mm});
            skArc(sketch, "E25.48.9", {"start": v(17.46, -0.43) * mm, "mid": v(17.46, -0.64) * mm, "end": v(17.45, -0.86) * mm});
            skArc(sketch, "E25.48.10", {"start": v(16.4, 0) * mm, "mid": v(16.4, -0.13) * mm, "end": v(16.4, -0.25) * mm});
            skArc(sketch, "E25.48.11", {"start": v(16.4, 0) * mm, "mid": v(16.4, 0.13) * mm, "end": v(16.4, 0.25) * mm});
            skPoint(sketch, "E25.49.0", {"position": v(17.42, 1.28) * mm});
            skPoint(sketch, "E25.49.1", {"position": v(17.33, 2.14) * mm});
            skPoint(sketch, "E25.49.2", {"position": v(16.3, 1.86) * mm});
            skPoint(sketch, "E25.49.3", {"position": v(16.89, 1.27) * mm});
            skPoint(sketch, "E25.49.4", {"position": v(16.8, 2.05) * mm});
            skArc(sketch, "E25.49.5", {"start": v(17.33, 2.14) * mm, "mid": v(17.3, 2.35) * mm, "end": v(17.28, 2.56) * mm});
            skArc(sketch, "E25.49.6", {"start": v(16.3, 1.86) * mm, "mid": v(16.8, 2.05) * mm, "end": v(17.33, 2.14) * mm});
            skPoint(sketch, "E25.49.7", {"position": v(16.35, 1.36) * mm});
            skArc(sketch, "E25.49.8", {"start": v(16.35, 1.36) * mm, "mid": v(16.88, 1.27) * mm, "end": v(17.42, 1.28) * mm});
            skArc(sketch, "E25.49.9", {"start": v(17.42, 1.28) * mm, "mid": v(17.43, 1.07) * mm, "end": v(17.45, 0.86) * mm});
            skArc(sketch, "E25.49.10", {"start": v(16.33, 1.6) * mm, "mid": v(16.34, 1.48) * mm, "end": v(16.35, 1.36) * mm});
            skArc(sketch, "E25.49.11", {"start": v(16.33, 1.6) * mm, "mid": v(16.31, 1.73) * mm, "end": v(16.3, 1.86) * mm});
            skPoint(sketch, "E25.50.0", {"position": v(17.2, 2.99) * mm});
            skPoint(sketch, "E25.50.1", {"position": v(17.04, 3.83) * mm});
            skPoint(sketch, "E25.50.2", {"position": v(16.04, 3.45) * mm});
            skPoint(sketch, "E25.50.3", {"position": v(16.68, 2.92) * mm});
            skPoint(sketch, "E25.50.4", {"position": v(16.53, 3.68) * mm});
            skArc(sketch, "E25.50.5", {"start": v(17.04, 3.83) * mm, "mid": v(17, 4.04) * mm, "end": v(16.95, 4.25) * mm});
            skArc(sketch, "E25.50.6", {"start": v(16.04, 3.45) * mm, "mid": v(16.52, 3.68) * mm, "end": v(17.04, 3.83) * mm});
            skPoint(sketch, "E25.50.7", {"position": v(16.14, 2.95) * mm});
            skArc(sketch, "E25.50.8", {"start": v(16.14, 2.95) * mm, "mid": v(16.67, 2.92) * mm, "end": v(17.2, 2.99) * mm});
            skArc(sketch, "E25.50.9", {"start": v(17.2, 2.99) * mm, "mid": v(17.25, 2.78) * mm, "end": v(17.28, 2.56) * mm});
            skArc(sketch, "E25.50.10", {"start": v(16.09, 3.2) * mm, "mid": v(16.11, 3.08) * mm, "end": v(16.14, 2.95) * mm});
            skArc(sketch, "E25.50.11", {"start": v(16.09, 3.2) * mm, "mid": v(16.06, 3.32) * mm, "end": v(16.04, 3.45) * mm});
            skPoint(sketch, "E25.51.0", {"position": v(16.83, 4.66) * mm});
            skPoint(sketch, "E25.51.1", {"position": v(16.58, 5.48) * mm});
            skPoint(sketch, "E25.51.2", {"position": v(15.62, 5) * mm});
            skPoint(sketch, "E25.51.3", {"position": v(16.31, 4.54) * mm});
            skPoint(sketch, "E25.51.4", {"position": v(16.09, 5.29) * mm});
            skArc(sketch, "E25.51.5", {"start": v(16.58, 5.48) * mm, "mid": v(16.52, 5.68) * mm, "end": v(16.45, 5.89) * mm});
            skArc(sketch, "E25.51.6", {"start": v(15.62, 5) * mm, "mid": v(16.08, 5.28) * mm, "end": v(16.58, 5.48) * mm});
            skPoint(sketch, "E25.51.7", {"position": v(15.77, 4.52) * mm});
            skArc(sketch, "E25.51.8", {"start": v(15.77, 4.52) * mm, "mid": v(16.3, 4.54) * mm, "end": v(16.83, 4.66) * mm});
            skArc(sketch, "E25.51.9", {"start": v(16.83, 4.66) * mm, "mid": v(16.9, 4.45) * mm, "end": v(16.95, 4.25) * mm});
            skArc(sketch, "E25.51.10", {"start": v(15.7, 4.76) * mm, "mid": v(15.73, 4.64) * mm, "end": v(15.77, 4.52) * mm});
            skArc(sketch, "E25.51.11", {"start": v(15.7, 4.76) * mm, "mid": v(15.66, 4.88) * mm, "end": v(15.62, 5) * mm});
            skPoint(sketch, "E25.52.0", {"position": v(16.3, 6.28) * mm});
            skPoint(sketch, "E25.52.1", {"position": v(15.96, 7.08) * mm});
            skPoint(sketch, "E25.52.2", {"position": v(15.06, 6.5) * mm});
            skPoint(sketch, "E25.52.3", {"position": v(15.79, 6.12) * mm});
            skPoint(sketch, "E25.52.4", {"position": v(15.5, 6.84) * mm});
            skArc(sketch, "E25.52.5", {"start": v(15.96, 7.08) * mm, "mid": v(15.88, 7.27) * mm, "end": v(15.8, 7.47) * mm});
            skArc(sketch, "E25.52.6", {"start": v(15.06, 6.5) * mm, "mid": v(15.48, 6.83) * mm, "end": v(15.96, 7.08) * mm});
            skPoint(sketch, "E25.52.7", {"position": v(15.25, 6.04) * mm});
            skArc(sketch, "E25.52.8", {"start": v(15.25, 6.04) * mm, "mid": v(15.78, 6.12) * mm, "end": v(16.3, 6.28) * mm});
            skArc(sketch, "E25.52.9", {"start": v(16.3, 6.28) * mm, "mid": v(16.37, 6.09) * mm, "end": v(16.45, 5.89) * mm});
            skArc(sketch, "E25.52.10", {"start": v(15.16, 6.28) * mm, "mid": v(15.2, 6.16) * mm, "end": v(15.25, 6.04) * mm});
            skArc(sketch, "E25.52.11", {"start": v(15.16, 6.28) * mm, "mid": v(15.1, 6.4) * mm, "end": v(15.06, 6.5) * mm});
            skPoint(sketch, "E25.53.0", {"position": v(15.6, 7.85) * mm});
            skPoint(sketch, "E25.53.1", {"position": v(15.2, 8.6) * mm});
            skPoint(sketch, "E25.53.2", {"position": v(14.35, 7.95) * mm});
            skPoint(sketch, "E25.53.3", {"position": v(15.11, 7.64) * mm});
            skPoint(sketch, "E25.53.4", {"position": v(14.75, 8.32) * mm});
            skArc(sketch, "E25.53.5", {"start": v(15.2, 8.6) * mm, "mid": v(15.1, 8.8) * mm, "end": v(14.99, 8.98) * mm});
            skArc(sketch, "E25.53.6", {"start": v(14.35, 7.95) * mm, "mid": v(14.74, 8.32) * mm, "end": v(15.2, 8.6) * mm});
            skPoint(sketch, "E25.53.7", {"position": v(14.58, 7.51) * mm});
            skArc(sketch, "E25.53.8", {"start": v(14.58, 7.51) * mm, "mid": v(15.1, 7.63) * mm, "end": v(15.6, 7.85) * mm});
            skArc(sketch, "E25.53.9", {"start": v(15.6, 7.85) * mm, "mid": v(15.7, 7.66) * mm, "end": v(15.8, 7.47) * mm});
            skArc(sketch, "E25.53.10", {"start": v(14.47, 7.73) * mm, "mid": v(14.53, 7.62) * mm, "end": v(14.58, 7.51) * mm});
            skArc(sketch, "E25.53.11", {"start": v(14.47, 7.73) * mm, "mid": v(14.4, 7.84) * mm, "end": v(14.35, 7.95) * mm});
            skPoint(sketch, "E25.54.0", {"position": v(14.75, 9.34) * mm});
            skPoint(sketch, "E25.54.1", {"position": v(14.28, 10.06) * mm});
            skPoint(sketch, "E25.54.2", {"position": v(13.5, 9.32) * mm});
            skPoint(sketch, "E25.54.3", {"position": v(14.3, 9.08) * mm});
            skPoint(sketch, "E25.54.4", {"position": v(13.86, 9.73) * mm});
            skArc(sketch, "E25.54.5", {"start": v(14.28, 10.06) * mm, "mid": v(14.16, 10.23) * mm, "end": v(14.03, 10.4) * mm});
            skArc(sketch, "E25.54.6", {"start": v(13.5, 9.32) * mm, "mid": v(13.85, 9.72) * mm, "end": v(14.28, 10.06) * mm});
            skPoint(sketch, "E25.54.7", {"position": v(13.78, 8.9) * mm});
            skArc(sketch, "E25.54.8", {"start": v(13.78, 8.9) * mm, "mid": v(14.29, 9.08) * mm, "end": v(14.75, 9.34) * mm});
            skArc(sketch, "E25.54.9", {"start": v(14.75, 9.34) * mm, "mid": v(14.87, 9.16) * mm, "end": v(14.99, 8.98) * mm});
            skArc(sketch, "E25.54.10", {"start": v(13.64, 9.11) * mm, "mid": v(13.7, 9) * mm, "end": v(13.78, 8.9) * mm});
            skArc(sketch, "E25.54.11", {"start": v(13.64, 9.11) * mm, "mid": v(13.57, 9.22) * mm, "end": v(13.5, 9.32) * mm});
            skPoint(sketch, "E25.55.0", {"position": v(13.77, 10.74) * mm});
            skPoint(sketch, "E25.55.1", {"position": v(13.22, 11.4) * mm});
            skPoint(sketch, "E25.55.2", {"position": v(12.52, 10.6) * mm});
            skPoint(sketch, "E25.55.3", {"position": v(13.33, 10.44) * mm});
            skPoint(sketch, "E25.55.4", {"position": v(12.84, 11.04) * mm});
            skArc(sketch, "E25.55.5", {"start": v(13.22, 11.4) * mm, "mid": v(13.09, 11.57) * mm, "end": v(12.95, 11.73) * mm});
            skArc(sketch, "E25.55.6", {"start": v(12.52, 10.6) * mm, "mid": v(12.83, 11.04) * mm, "end": v(13.22, 11.4) * mm});
            skPoint(sketch, "E25.55.7", {"position": v(12.84, 10.21) * mm});
            skArc(sketch, "E25.55.8", {"start": v(12.84, 10.21) * mm, "mid": v(13.33, 10.43) * mm, "end": v(13.77, 10.74) * mm});
            skArc(sketch, "E25.55.9", {"start": v(13.77, 10.74) * mm, "mid": v(13.9, 10.58) * mm, "end": v(14.03, 10.4) * mm});
            skArc(sketch, "E25.55.10", {"start": v(12.68, 10.4) * mm, "mid": v(12.76, 10.3) * mm, "end": v(12.84, 10.21) * mm});
            skArc(sketch, "E25.55.11", {"start": v(12.68, 10.4) * mm, "mid": v(12.6, 10.5) * mm, "end": v(12.52, 10.6) * mm});
            skPoint(sketch, "E25.56.0", {"position": v(12.65, 12.04) * mm});
            skPoint(sketch, "E25.56.1", {"position": v(12.04, 12.65) * mm});
            skPoint(sketch, "E25.56.2", {"position": v(11.42, 11.78) * mm});
            skPoint(sketch, "E25.56.3", {"position": v(12.25, 11.7) * mm});
            skPoint(sketch, "E25.56.4", {"position": v(11.7, 12.25) * mm});
            skArc(sketch, "E25.56.5", {"start": v(12.04, 12.65) * mm, "mid": v(11.89, 12.8) * mm, "end": v(11.73, 12.95) * mm});
            skArc(sketch, "E25.56.6", {"start": v(11.42, 11.78) * mm, "mid": v(11.7, 12.24) * mm, "end": v(12.04, 12.65) * mm});
            skPoint(sketch, "E25.56.7", {"position": v(11.78, 11.42) * mm});
            skArc(sketch, "E25.56.8", {"start": v(11.78, 11.42) * mm, "mid": v(12.24, 11.7) * mm, "end": v(12.65, 12.04) * mm});
            skArc(sketch, "E25.56.9", {"start": v(12.65, 12.04) * mm, "mid": v(12.8, 11.89) * mm, "end": v(12.95, 11.73) * mm});
            skArc(sketch, "E25.56.10", {"start": v(11.6, 11.6) * mm, "mid": v(11.69, 11.51) * mm, "end": v(11.78, 11.42) * mm});
            skArc(sketch, "E25.56.11", {"start": v(11.6, 11.6) * mm, "mid": v(11.51, 11.69) * mm, "end": v(11.42, 11.78) * mm});
            skPoint(sketch, "E25.57.0", {"position": v(11.4, 13.22) * mm});
            skPoint(sketch, "E25.57.1", {"position": v(10.74, 13.77) * mm});
            skPoint(sketch, "E25.57.2", {"position": v(10.21, 12.84) * mm});
            skPoint(sketch, "E25.57.3", {"position": v(11.04, 12.84) * mm});
            skPoint(sketch, "E25.57.4", {"position": v(10.44, 13.33) * mm});
            skArc(sketch, "E25.57.5", {"start": v(10.74, 13.77) * mm, "mid": v(10.58, 13.9) * mm, "end": v(10.4, 14.03) * mm});
            skArc(sketch, "E25.57.6", {"start": v(10.21, 12.84) * mm, "mid": v(10.43, 13.33) * mm, "end": v(10.74, 13.77) * mm});
            skPoint(sketch, "E25.57.7", {"position": v(10.6, 12.52) * mm});
            skArc(sketch, "E25.57.8", {"start": v(10.6, 12.52) * mm, "mid": v(11.04, 12.83) * mm, "end": v(11.4, 13.22) * mm});
            skArc(sketch, "E25.57.9", {"start": v(11.4, 13.22) * mm, "mid": v(11.57, 13.09) * mm, "end": v(11.73, 12.95) * mm});
            skArc(sketch, "E25.57.10", {"start": v(10.4, 12.68) * mm, "mid": v(10.5, 12.6) * mm, "end": v(10.6, 12.52) * mm});
            skArc(sketch, "E25.57.11", {"start": v(10.4, 12.68) * mm, "mid": v(10.3, 12.76) * mm, "end": v(10.21, 12.84) * mm});
            skPoint(sketch, "E25.58.0", {"position": v(10.06, 14.28) * mm});
            skPoint(sketch, "E25.58.1", {"position": v(9.34, 14.75) * mm});
            skPoint(sketch, "E25.58.2", {"position": v(8.9, 13.78) * mm});
            skPoint(sketch, "E25.58.3", {"position": v(9.73, 13.86) * mm});
            skPoint(sketch, "E25.58.4", {"position": v(9.08, 14.3) * mm});
            skArc(sketch, "E25.58.5", {"start": v(9.34, 14.75) * mm, "mid": v(9.16, 14.87) * mm, "end": v(8.98, 14.99) * mm});
            skArc(sketch, "E25.58.6", {"start": v(8.9, 13.78) * mm, "mid": v(9.08, 14.29) * mm, "end": v(9.34, 14.75) * mm});
            skPoint(sketch, "E25.58.7", {"position": v(9.32, 13.5) * mm});
            skArc(sketch, "E25.58.8", {"start": v(9.32, 13.5) * mm, "mid": v(9.72, 13.85) * mm, "end": v(10.06, 14.28) * mm});
            skArc(sketch, "E25.58.9", {"start": v(10.06, 14.28) * mm, "mid": v(10.23, 14.16) * mm, "end": v(10.4, 14.03) * mm});
            skArc(sketch, "E25.58.10", {"start": v(9.11, 13.64) * mm, "mid": v(9.22, 13.57) * mm, "end": v(9.32, 13.5) * mm});
            skArc(sketch, "E25.58.11", {"start": v(9.11, 13.64) * mm, "mid": v(9, 13.7) * mm, "end": v(8.9, 13.78) * mm});
            skPoint(sketch, "E25.59.0", {"position": v(8.6, 15.2) * mm});
            skPoint(sketch, "E25.59.1", {"position": v(7.85, 15.6) * mm});
            skPoint(sketch, "E25.59.2", {"position": v(7.51, 14.58) * mm});
            skPoint(sketch, "E25.59.3", {"position": v(8.32, 14.75) * mm});
            skPoint(sketch, "E25.59.4", {"position": v(7.64, 15.11) * mm});
            skArc(sketch, "E25.59.5", {"start": v(7.85, 15.6) * mm, "mid": v(7.66, 15.7) * mm, "end": v(7.47, 15.8) * mm});
            skArc(sketch, "E25.59.6", {"start": v(7.51, 14.58) * mm, "mid": v(7.63, 15.1) * mm, "end": v(7.85, 15.6) * mm});
            skPoint(sketch, "E25.59.7", {"position": v(7.95, 14.35) * mm});
            skArc(sketch, "E25.59.8", {"start": v(7.95, 14.35) * mm, "mid": v(8.32, 14.74) * mm, "end": v(8.6, 15.2) * mm});
            skArc(sketch, "E25.59.9", {"start": v(8.6, 15.2) * mm, "mid": v(8.8, 15.1) * mm, "end": v(8.98, 14.99) * mm});
            skArc(sketch, "E25.59.10", {"start": v(7.73, 14.47) * mm, "mid": v(7.84, 14.4) * mm, "end": v(7.95, 14.35) * mm});
            skArc(sketch, "E25.59.11", {"start": v(7.73, 14.47) * mm, "mid": v(7.62, 14.53) * mm, "end": v(7.51, 14.58) * mm});
            skPoint(sketch, "E25.60.0", {"position": v(7.08, 15.96) * mm});
            skPoint(sketch, "E25.60.1", {"position": v(6.28, 16.3) * mm});
            skPoint(sketch, "E25.60.2", {"position": v(6.04, 15.25) * mm});
            skPoint(sketch, "E25.60.3", {"position": v(6.84, 15.5) * mm});
            skPoint(sketch, "E25.60.4", {"position": v(6.12, 15.79) * mm});
            skArc(sketch, "E25.60.5", {"start": v(6.28, 16.3) * mm, "mid": v(6.09, 16.37) * mm, "end": v(5.89, 16.45) * mm});
            skArc(sketch, "E25.60.6", {"start": v(6.04, 15.25) * mm, "mid": v(6.12, 15.78) * mm, "end": v(6.28, 16.3) * mm});
            skPoint(sketch, "E25.60.7", {"position": v(6.5, 15.06) * mm});
            skArc(sketch, "E25.60.8", {"start": v(6.5, 15.06) * mm, "mid": v(6.83, 15.48) * mm, "end": v(7.08, 15.96) * mm});
            skArc(sketch, "E25.60.9", {"start": v(7.08, 15.96) * mm, "mid": v(7.27, 15.88) * mm, "end": v(7.47, 15.8) * mm});
            skArc(sketch, "E25.60.10", {"start": v(6.28, 15.16) * mm, "mid": v(6.4, 15.1) * mm, "end": v(6.5, 15.06) * mm});
            skArc(sketch, "E25.60.11", {"start": v(6.28, 15.16) * mm, "mid": v(6.16, 15.2) * mm, "end": v(6.04, 15.25) * mm});
            skPoint(sketch, "E25.61.0", {"position": v(5.48, 16.58) * mm});
            skPoint(sketch, "E25.61.1", {"position": v(4.66, 16.83) * mm});
            skPoint(sketch, "E25.61.2", {"position": v(4.52, 15.77) * mm});
            skPoint(sketch, "E25.61.3", {"position": v(5.29, 16.09) * mm});
            skPoint(sketch, "E25.61.4", {"position": v(4.54, 16.31) * mm});
            skArc(sketch, "E25.61.5", {"start": v(4.66, 16.83) * mm, "mid": v(4.45, 16.9) * mm, "end": v(4.25, 16.95) * mm});
            skArc(sketch, "E25.61.6", {"start": v(4.52, 15.77) * mm, "mid": v(4.54, 16.3) * mm, "end": v(4.66, 16.83) * mm});
            skPoint(sketch, "E25.61.7", {"position": v(5, 15.62) * mm});
            skArc(sketch, "E25.61.8", {"start": v(5, 15.62) * mm, "mid": v(5.28, 16.08) * mm, "end": v(5.48, 16.58) * mm});
            skArc(sketch, "E25.61.9", {"start": v(5.48, 16.58) * mm, "mid": v(5.68, 16.52) * mm, "end": v(5.89, 16.45) * mm});
            skArc(sketch, "E25.61.10", {"start": v(4.76, 15.7) * mm, "mid": v(4.88, 15.66) * mm, "end": v(5, 15.62) * mm});
            skArc(sketch, "E25.61.11", {"start": v(4.76, 15.7) * mm, "mid": v(4.64, 15.73) * mm, "end": v(4.52, 15.77) * mm});
            skPoint(sketch, "E25.62.0", {"position": v(3.83, 17.04) * mm});
            skPoint(sketch, "E25.62.1", {"position": v(2.99, 17.2) * mm});
            skPoint(sketch, "E25.62.2", {"position": v(2.95, 16.14) * mm});
            skPoint(sketch, "E25.62.3", {"position": v(3.68, 16.53) * mm});
            skPoint(sketch, "E25.62.4", {"position": v(2.92, 16.68) * mm});
            skArc(sketch, "E25.62.5", {"start": v(2.99, 17.2) * mm, "mid": v(2.78, 17.25) * mm, "end": v(2.56, 17.28) * mm});
            skArc(sketch, "E25.62.6", {"start": v(2.95, 16.14) * mm, "mid": v(2.92, 16.67) * mm, "end": v(2.99, 17.2) * mm});
            skPoint(sketch, "E25.62.7", {"position": v(3.45, 16.04) * mm});
            skArc(sketch, "E25.62.8", {"start": v(3.45, 16.04) * mm, "mid": v(3.68, 16.52) * mm, "end": v(3.83, 17.04) * mm});
            skArc(sketch, "E25.62.9", {"start": v(3.83, 17.04) * mm, "mid": v(4.04, 17) * mm, "end": v(4.25, 16.95) * mm});
            skArc(sketch, "E25.62.10", {"start": v(3.2, 16.09) * mm, "mid": v(3.32, 16.06) * mm, "end": v(3.45, 16.04) * mm});
            skArc(sketch, "E25.62.11", {"start": v(3.2, 16.09) * mm, "mid": v(3.08, 16.11) * mm, "end": v(2.95, 16.14) * mm});
            skPoint(sketch, "E25.63.0", {"position": v(2.14, 17.33) * mm});
            skPoint(sketch, "E25.63.1", {"position": v(1.28, 17.42) * mm});
            skPoint(sketch, "E25.63.2", {"position": v(1.36, 16.35) * mm});
            skPoint(sketch, "E25.63.3", {"position": v(2.05, 16.8) * mm});
            skPoint(sketch, "E25.63.4", {"position": v(1.27, 16.89) * mm});
            skArc(sketch, "E25.63.5", {"start": v(1.28, 17.42) * mm, "mid": v(1.07, 17.43) * mm, "end": v(0.86, 17.45) * mm});
            skArc(sketch, "E25.63.6", {"start": v(1.36, 16.35) * mm, "mid": v(1.27, 16.88) * mm, "end": v(1.28, 17.42) * mm});
            skPoint(sketch, "E25.63.7", {"position": v(1.86, 16.3) * mm});
            skArc(sketch, "E25.63.8", {"start": v(1.86, 16.3) * mm, "mid": v(2.05, 16.8) * mm, "end": v(2.14, 17.33) * mm});
            skArc(sketch, "E25.63.9", {"start": v(2.14, 17.33) * mm, "mid": v(2.35, 17.3) * mm, "end": v(2.56, 17.28) * mm});
            skArc(sketch, "E25.63.10", {"start": v(1.6, 16.33) * mm, "mid": v(1.73, 16.31) * mm, "end": v(1.86, 16.3) * mm});
            skArc(sketch, "E25.63.11", {"start": v(1.6, 16.33) * mm, "mid": v(1.48, 16.34) * mm, "end": v(1.36, 16.35) * mm});
            skLineSegment(sketch, "E26", {"start": v(0, 0) * mm, "end": v(0, 18.23) * mm});
            skArc(sketch, "E27", {"start": v(-1.28, 17.42) * mm, "mid": v(-0.86, 17.44) * mm, "end": v(-0.43, 17.46) * mm});
            skArc(sketch, "E28.1.0", {"start": v(-2.99, 17.2) * mm, "mid": v(-2.56, 17.27) * mm, "end": v(-2.14, 17.33) * mm});
            skArc(sketch, "E28.2.0", {"start": v(-4.66, 16.83) * mm, "mid": v(-4.24, 16.94) * mm, "end": v(-3.83, 17.04) * mm});
            skArc(sketch, "E28.3.0", {"start": v(-6.28, 16.3) * mm, "mid": v(-5.88, 16.44) * mm, "end": v(-5.48, 16.58) * mm});
            skArc(sketch, "E28.4.0", {"start": v(-7.85, 15.6) * mm, "mid": v(-7.47, 15.79) * mm, "end": v(-7.08, 15.96) * mm});
            skArc(sketch, "E28.5.0", {"start": v(-9.34, 14.75) * mm, "mid": v(-8.98, 14.98) * mm, "end": v(-8.6, 15.2) * mm});
            skArc(sketch, "E28.6.0", {"start": v(-10.74, 13.77) * mm, "mid": v(-10.4, 14.03) * mm, "end": v(-10.06, 14.28) * mm});
            skArc(sketch, "E28.7.0", {"start": v(-12.04, 12.65) * mm, "mid": v(-11.73, 12.94) * mm, "end": v(-11.4, 13.22) * mm});
            skArc(sketch, "E28.8.0", {"start": v(-13.22, 11.4) * mm, "mid": v(-12.94, 11.73) * mm, "end": v(-12.65, 12.04) * mm});
            skArc(sketch, "E28.9.0", {"start": v(-14.28, 10.06) * mm, "mid": v(-14.03, 10.4) * mm, "end": v(-13.77, 10.74) * mm});
            skArc(sketch, "E28.10.0", {"start": v(-15.2, 8.6) * mm, "mid": v(-14.98, 8.98) * mm, "end": v(-14.75, 9.34) * mm});
            skArc(sketch, "E28.11.0", {"start": v(-15.96, 7.08) * mm, "mid": v(-15.79, 7.47) * mm, "end": v(-15.6, 7.85) * mm});
            skArc(sketch, "E28.12.0", {"start": v(-16.58, 5.48) * mm, "mid": v(-16.44, 5.88) * mm, "end": v(-16.3, 6.28) * mm});
            skArc(sketch, "E28.13.0", {"start": v(-17.04, 3.83) * mm, "mid": v(-16.94, 4.24) * mm, "end": v(-16.83, 4.66) * mm});
            skArc(sketch, "E28.14.0", {"start": v(-17.33, 2.14) * mm, "mid": v(-17.27, 2.56) * mm, "end": v(-17.2, 2.99) * mm});
            skArc(sketch, "E28.15.0", {"start": v(-17.46, 0.43) * mm, "mid": v(-17.44, 0.86) * mm, "end": v(-17.42, 1.28) * mm});
            skArc(sketch, "E28.16.0", {"start": v(-17.42, -1.28) * mm, "mid": v(-17.44, -0.86) * mm, "end": v(-17.46, -0.43) * mm});
            skArc(sketch, "E28.17.0", {"start": v(-17.2, -2.99) * mm, "mid": v(-17.27, -2.56) * mm, "end": v(-17.33, -2.14) * mm});
            skArc(sketch, "E28.18.0", {"start": v(-16.83, -4.66) * mm, "mid": v(-16.94, -4.24) * mm, "end": v(-17.04, -3.83) * mm});
            skArc(sketch, "E28.19.0", {"start": v(-16.3, -6.28) * mm, "mid": v(-16.44, -5.88) * mm, "end": v(-16.58, -5.48) * mm});
            skArc(sketch, "E28.20.0", {"start": v(-15.6, -7.85) * mm, "mid": v(-15.79, -7.47) * mm, "end": v(-15.96, -7.08) * mm});
            skArc(sketch, "E28.21.0", {"start": v(-14.75, -9.34) * mm, "mid": v(-14.98, -8.98) * mm, "end": v(-15.2, -8.6) * mm});
            skArc(sketch, "E28.22.0", {"start": v(-13.77, -10.74) * mm, "mid": v(-14.03, -10.4) * mm, "end": v(-14.28, -10.06) * mm});
            skArc(sketch, "E28.23.0", {"start": v(-12.65, -12.04) * mm, "mid": v(-12.94, -11.73) * mm, "end": v(-13.22, -11.4) * mm});
            skArc(sketch, "E28.24.0", {"start": v(-11.4, -13.22) * mm, "mid": v(-11.73, -12.94) * mm, "end": v(-12.04, -12.65) * mm});
            skArc(sketch, "E28.25.0", {"start": v(-10.06, -14.28) * mm, "mid": v(-10.4, -14.03) * mm, "end": v(-10.74, -13.77) * mm});
            skArc(sketch, "E28.26.0", {"start": v(-8.6, -15.2) * mm, "mid": v(-8.98, -14.98) * mm, "end": v(-9.34, -14.75) * mm});
            skArc(sketch, "E28.27.0", {"start": v(-7.08, -15.96) * mm, "mid": v(-7.47, -15.79) * mm, "end": v(-7.85, -15.6) * mm});
            skArc(sketch, "E28.28.0", {"start": v(-5.48, -16.58) * mm, "mid": v(-5.88, -16.44) * mm, "end": v(-6.28, -16.3) * mm});
            skArc(sketch, "E28.29.0", {"start": v(-3.83, -17.04) * mm, "mid": v(-4.24, -16.94) * mm, "end": v(-4.66, -16.83) * mm});
            skArc(sketch, "E28.30.0", {"start": v(-2.14, -17.33) * mm, "mid": v(-2.56, -17.27) * mm, "end": v(-2.99, -17.2) * mm});
            skArc(sketch, "E28.31.0", {"start": v(-0.43, -17.46) * mm, "mid": v(-0.86, -17.44) * mm, "end": v(-1.28, -17.42) * mm});
            skArc(sketch, "E28.32.0", {"start": v(1.28, -17.42) * mm, "mid": v(0.86, -17.44) * mm, "end": v(0.43, -17.46) * mm});
            skArc(sketch, "E28.33.0", {"start": v(2.99, -17.2) * mm, "mid": v(2.56, -17.27) * mm, "end": v(2.14, -17.33) * mm});
            skArc(sketch, "E28.34.0", {"start": v(4.66, -16.83) * mm, "mid": v(4.24, -16.94) * mm, "end": v(3.83, -17.04) * mm});
            skArc(sketch, "E28.35.0", {"start": v(6.28, -16.3) * mm, "mid": v(5.88, -16.44) * mm, "end": v(5.48, -16.58) * mm});
            skArc(sketch, "E28.36.0", {"start": v(7.85, -15.6) * mm, "mid": v(7.47, -15.79) * mm, "end": v(7.08, -15.96) * mm});
            skArc(sketch, "E28.37.0", {"start": v(9.34, -14.75) * mm, "mid": v(8.98, -14.98) * mm, "end": v(8.6, -15.2) * mm});
            skArc(sketch, "E28.38.0", {"start": v(10.74, -13.77) * mm, "mid": v(10.4, -14.03) * mm, "end": v(10.06, -14.28) * mm});
            skArc(sketch, "E28.39.0", {"start": v(12.04, -12.65) * mm, "mid": v(11.73, -12.94) * mm, "end": v(11.4, -13.22) * mm});
            skArc(sketch, "E28.40.0", {"start": v(13.22, -11.4) * mm, "mid": v(12.94, -11.73) * mm, "end": v(12.65, -12.04) * mm});
            skArc(sketch, "E28.41.0", {"start": v(14.28, -10.06) * mm, "mid": v(14.03, -10.4) * mm, "end": v(13.77, -10.74) * mm});
            skArc(sketch, "E28.42.0", {"start": v(15.2, -8.6) * mm, "mid": v(14.98, -8.98) * mm, "end": v(14.75, -9.34) * mm});
            skArc(sketch, "E28.43.0", {"start": v(15.96, -7.08) * mm, "mid": v(15.79, -7.47) * mm, "end": v(15.6, -7.85) * mm});
            skArc(sketch, "E28.44.0", {"start": v(16.58, -5.48) * mm, "mid": v(16.44, -5.88) * mm, "end": v(16.3, -6.28) * mm});
            skArc(sketch, "E28.45.0", {"start": v(17.04, -3.83) * mm, "mid": v(16.94, -4.24) * mm, "end": v(16.83, -4.66) * mm});
            skArc(sketch, "E28.46.0", {"start": v(17.33, -2.14) * mm, "mid": v(17.27, -2.56) * mm, "end": v(17.2, -2.99) * mm});
            skArc(sketch, "E28.47.0", {"start": v(17.46, -0.43) * mm, "mid": v(17.44, -0.86) * mm, "end": v(17.42, -1.28) * mm});
            skArc(sketch, "E28.48.0", {"start": v(17.42, 1.28) * mm, "mid": v(17.44, 0.86) * mm, "end": v(17.46, 0.43) * mm});
            skArc(sketch, "E28.49.0", {"start": v(17.2, 2.99) * mm, "mid": v(17.27, 2.56) * mm, "end": v(17.33, 2.14) * mm});
            skArc(sketch, "E28.50.0", {"start": v(16.83, 4.66) * mm, "mid": v(16.94, 4.24) * mm, "end": v(17.04, 3.83) * mm});
            skArc(sketch, "E28.51.0", {"start": v(16.3, 6.28) * mm, "mid": v(16.44, 5.88) * mm, "end": v(16.58, 5.48) * mm});
            skArc(sketch, "E28.52.0", {"start": v(15.6, 7.85) * mm, "mid": v(15.79, 7.47) * mm, "end": v(15.96, 7.08) * mm});
            skArc(sketch, "E28.53.0", {"start": v(14.75, 9.34) * mm, "mid": v(14.98, 8.98) * mm, "end": v(15.2, 8.6) * mm});
            skArc(sketch, "E28.54.0", {"start": v(13.77, 10.74) * mm, "mid": v(14.03, 10.4) * mm, "end": v(14.28, 10.06) * mm});
            skArc(sketch, "E28.55.0", {"start": v(12.65, 12.04) * mm, "mid": v(12.94, 11.73) * mm, "end": v(13.22, 11.4) * mm});
            skArc(sketch, "E28.56.0", {"start": v(11.4, 13.22) * mm, "mid": v(11.73, 12.94) * mm, "end": v(12.04, 12.65) * mm});
            skArc(sketch, "E28.57.0", {"start": v(10.06, 14.28) * mm, "mid": v(10.4, 14.03) * mm, "end": v(10.74, 13.77) * mm});
            skArc(sketch, "E28.58.0", {"start": v(8.6, 15.2) * mm, "mid": v(8.98, 14.98) * mm, "end": v(9.34, 14.75) * mm});
            skArc(sketch, "E28.59.0", {"start": v(7.08, 15.96) * mm, "mid": v(7.47, 15.79) * mm, "end": v(7.85, 15.6) * mm});
            skArc(sketch, "E28.60.0", {"start": v(5.48, 16.58) * mm, "mid": v(5.88, 16.44) * mm, "end": v(6.28, 16.3) * mm});
            skArc(sketch, "E28.61.0", {"start": v(3.83, 17.04) * mm, "mid": v(4.24, 16.94) * mm, "end": v(4.66, 16.83) * mm});
            skArc(sketch, "E28.62.0", {"start": v(2.14, 17.33) * mm, "mid": v(2.56, 17.27) * mm, "end": v(2.99, 17.2) * mm});
            skArc(sketch, "E28.63.0", {"start": v(0.43, 17.46) * mm, "mid": v(0.86, 17.44) * mm, "end": v(1.28, 17.42) * mm});
            skSolve(sketch);
        }
        {
            var Q0;
            Q0=makeQuery(id+"F0.imprint","IMPRINT",FACE,{"disambiguationData":[TD([[makeQuery(id+"F0.imprint","IMPRINT",EDGE,{"derivedFrom":sQuery(id+"F0.wireOp",EDGE,"E6")}),1.0]])]});
            extrude(context, id + "F1", {"entities" : qUnion([Q0]), "depth" : .1 * mm, "offsetDistance" : 25.4 * mm});
        }
    });
